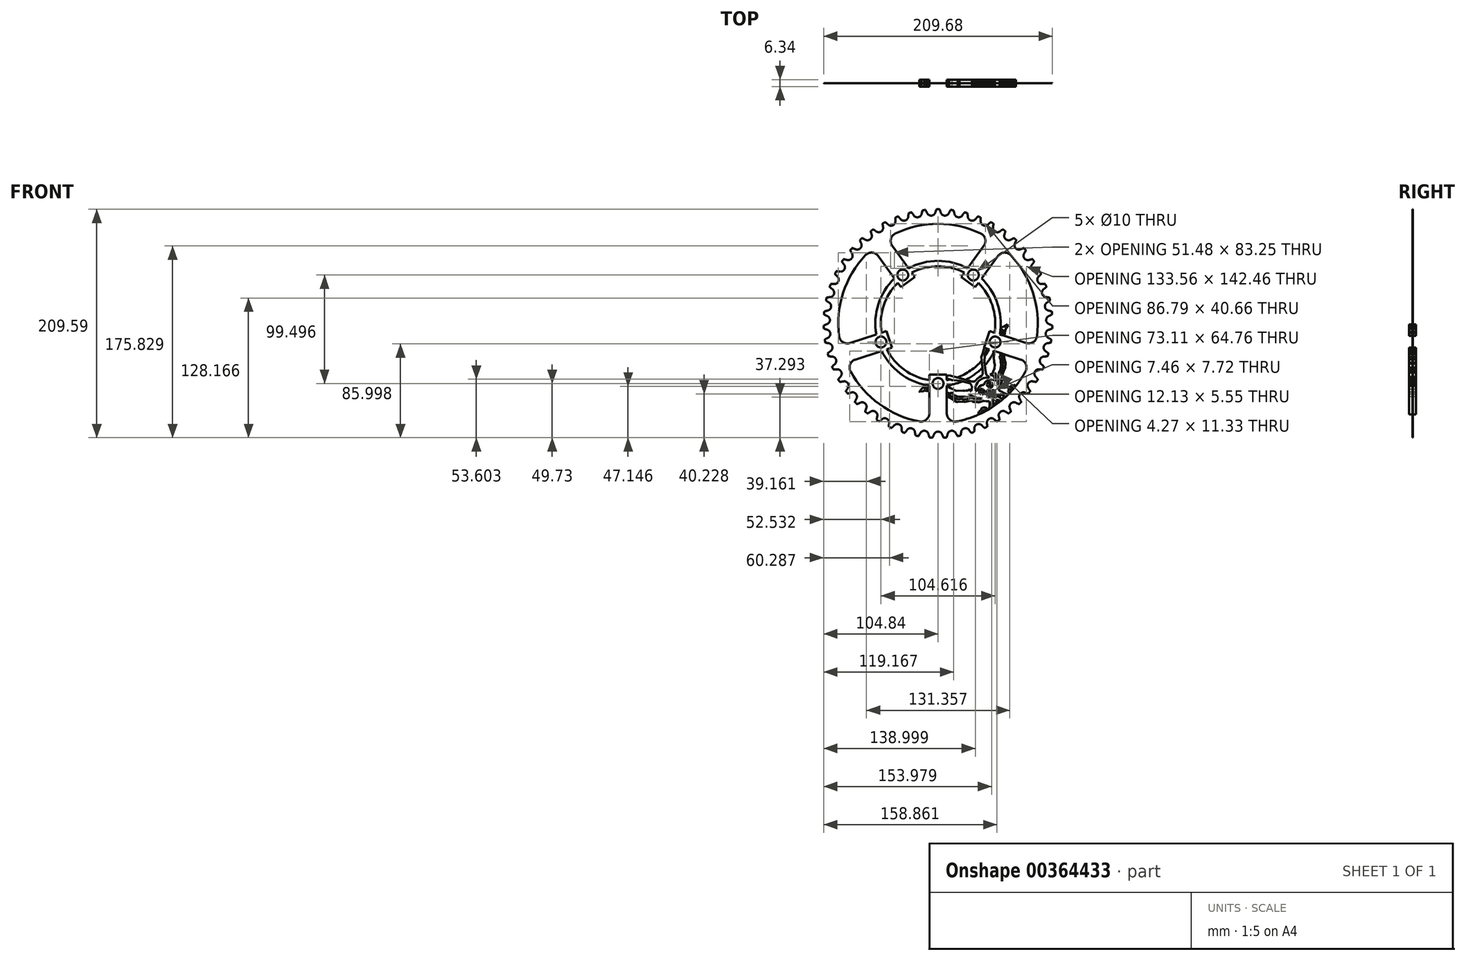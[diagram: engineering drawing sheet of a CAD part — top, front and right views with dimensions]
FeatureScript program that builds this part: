
annotation { "Feature Type Name" : "Feature", "Feature Type Description" : "" }
export const myFeature = defineFeature(function(context is Context, id is Id, definition is map)
    precondition{}
    {
        {
            var Q0;
            Q0=qCreatedBy(makeId("Front.planeOp"),FACE);
            var sketch = newSketch(context, id + "F0", { "sketchPlane" : qUnion([Q0])});
            skLineSegment(sketch, "E0", {"start": v(0, 0) * mm, "end": v(-6.35, 102.95) * mm, "construction": true});
            skLineSegment(sketch, "E1", {"start": v(0, 0) * mm, "end": v(6.35, 102.95) * mm, "construction": true});
            skArc(sketch, "E2", {"start": v(-6.1, 99) * mm, "mid": v(-3.93, 99.81) * mm, "end": v(-2.58, 101.71) * mm, "construction": true});
            skArc(sketch, "E3", {"start": v(-1.4, 104.85) * mm, "mid": v(-2, 103.3) * mm, "end": v(-2.55, 101.74) * mm});
            skLineSegment(sketch, "E4", {"start": v(-6.35, 102.95) * mm, "end": v(-2.58, 101.71) * mm, "construction": true});
            skCircle(sketch, "E5", {"center": v(0, 0) * mm, "radius": 103.19 * mm, "construction": true});
            skArc(sketch, "E6", {"start": v(1.4, 104.85) * mm, "mid": v(0, 104.86) * mm, "end": v(-1.4, 104.85) * mm});
            skLineSegment(sketch, "E7", {"start": v(0, 0) * mm, "end": v(0, 116.9) * mm, "construction": true});
            skArc(sketch, "E8", {"start": v(-6.1, 99) * mm, "mid": v(-3.9, 99.82) * mm, "end": v(-2.55, 101.74) * mm});
            skArc(sketch, "E9", {"start": v(2.58, 101.71) * mm, "mid": v(3.93, 99.81) * mm, "end": v(6.1, 99) * mm, "construction": true});
            skArc(sketch, "E10", {"start": v(2.55, 101.74) * mm, "mid": v(3.9, 99.82) * mm, "end": v(6.1, 99) * mm});
            skArc(sketch, "E11", {"start": v(2.56, 101.7) * mm, "mid": v(2, 103.29) * mm, "end": v(1.4, 104.85) * mm});
            skLineSegment(sketch, "E12", {"start": v(6.35, 102.95) * mm, "end": v(2.56, 101.7) * mm, "construction": true});
            skArc(sketch, "E13.1.0", {"start": v(-18.22, 97.5) * mm, "mid": v(-16.14, 98.58) * mm, "end": v(-15.03, 100.65) * mm});
            skArc(sketch, "E13.1.1", {"start": v(-14.27, 103.88) * mm, "mid": v(-14.68, 102.27) * mm, "end": v(-15.03, 100.65) * mm});
            skArc(sketch, "E13.1.2", {"start": v(-11.5, 104.22) * mm, "mid": v(-12.89, 104.06) * mm, "end": v(-14.27, 103.88) * mm});
            skArc(sketch, "E13.1.3", {"start": v(-9.96, 101.25) * mm, "mid": v(-10.7, 102.75) * mm, "end": v(-11.5, 104.22) * mm});
            skArc(sketch, "E13.1.4", {"start": v(-9.98, 101.28) * mm, "mid": v(-8.4, 99.54) * mm, "end": v(-6.1, 99) * mm});
            skArc(sketch, "E13.2.0", {"start": v(-30.07, 94.51) * mm, "mid": v(-28.13, 95.85) * mm, "end": v(-27.28, 98.04) * mm});
            skArc(sketch, "E13.2.1", {"start": v(-26.93, 101.34) * mm, "mid": v(-27.14, 99.7) * mm, "end": v(-27.28, 98.04) * mm});
            skArc(sketch, "E13.2.2", {"start": v(-24.22, 102.02) * mm, "mid": v(-25.58, 101.69) * mm, "end": v(-26.93, 101.34) * mm});
            skArc(sketch, "E13.2.3", {"start": v(-22.33, 99.26) * mm, "mid": v(-23.25, 100.66) * mm, "end": v(-24.22, 102.02) * mm});
            skArc(sketch, "E13.2.4", {"start": v(-22.35, 99.29) * mm, "mid": v(-20.56, 97.76) * mm, "end": v(-18.22, 97.5) * mm});
            skArc(sketch, "E13.3.0", {"start": v(-41.45, 90.1) * mm, "mid": v(-39.7, 91.67) * mm, "end": v(-39.13, 93.95) * mm});
            skArc(sketch, "E13.3.1", {"start": v(-39.18, 97.26) * mm, "mid": v(-39.18, 95.6) * mm, "end": v(-39.13, 93.95) * mm});
            skArc(sketch, "E13.3.2", {"start": v(-36.57, 98.27) * mm, "mid": v(-37.88, 97.78) * mm, "end": v(-39.18, 97.26) * mm});
            skArc(sketch, "E13.3.3", {"start": v(-34.36, 95.76) * mm, "mid": v(-35.44, 97.04) * mm, "end": v(-36.57, 98.27) * mm});
            skArc(sketch, "E13.3.4", {"start": v(-34.38, 95.79) * mm, "mid": v(-32.42, 94.49) * mm, "end": v(-30.07, 94.51) * mm});
            skArc(sketch, "E13.4.0", {"start": v(-52.21, 84.33) * mm, "mid": v(-50.66, 86.1) * mm, "end": v(-50.37, 88.43) * mm});
            skArc(sketch, "E13.4.1", {"start": v(-50.83, 91.71) * mm, "mid": v(-50.63, 90.06) * mm, "end": v(-50.37, 88.43) * mm});
            skArc(sketch, "E13.4.2", {"start": v(-48.37, 93.03) * mm, "mid": v(-49.6, 92.38) * mm, "end": v(-50.83, 91.71) * mm});
            skArc(sketch, "E13.4.3", {"start": v(-45.86, 90.81) * mm, "mid": v(-47.1, 91.94) * mm, "end": v(-48.37, 93.03) * mm});
            skArc(sketch, "E13.4.4", {"start": v(-45.89, 90.84) * mm, "mid": v(-43.78, 89.79) * mm, "end": v(-41.45, 90.1) * mm});
            skArc(sketch, "E13.5.0", {"start": v(-62.18, 77.27) * mm, "mid": v(-60.86, 79.22) * mm, "end": v(-60.86, 81.57) * mm});
            skArc(sketch, "E13.5.1", {"start": v(-61.72, 84.77) * mm, "mid": v(-61.32, 83.16) * mm, "end": v(-60.86, 81.57) * mm});
            skArc(sketch, "E13.5.2", {"start": v(-59.44, 86.38) * mm, "mid": v(-60.58, 85.58) * mm, "end": v(-61.72, 84.77) * mm});
            skArc(sketch, "E13.5.3", {"start": v(-56.68, 84.49) * mm, "mid": v(-58.04, 85.46) * mm, "end": v(-59.44, 86.38) * mm});
            skArc(sketch, "E13.5.4", {"start": v(-56.7, 84.5) * mm, "mid": v(-54.49, 83.73) * mm, "end": v(-52.21, 84.33) * mm});
            skArc(sketch, "E13.6.0", {"start": v(-71.2, 69.04) * mm, "mid": v(-70.13, 71.14) * mm, "end": v(-70.42, 73.47) * mm});
            skArc(sketch, "E13.6.1", {"start": v(-71.67, 76.54) * mm, "mid": v(-71.07, 75) * mm, "end": v(-70.42, 73.47) * mm});
            skArc(sketch, "E13.6.2", {"start": v(-69.6, 78.42) * mm, "mid": v(-70.64, 77.49) * mm, "end": v(-71.67, 76.54) * mm});
            skArc(sketch, "E13.6.3", {"start": v(-66.63, 76.88) * mm, "mid": v(-68.1, 77.68) * mm, "end": v(-69.6, 78.42) * mm});
            skArc(sketch, "E13.6.4", {"start": v(-66.66, 76.9) * mm, "mid": v(-64.36, 76.4) * mm, "end": v(-62.18, 77.27) * mm});
            skArc(sketch, "E13.7.0", {"start": v(-79.15, 59.77) * mm, "mid": v(-78.34, 61.98) * mm, "end": v(-78.92, 64.26) * mm});
            skArc(sketch, "E13.7.1", {"start": v(-80.53, 67.15) * mm, "mid": v(-79.75, 65.7) * mm, "end": v(-78.92, 64.26) * mm});
            skArc(sketch, "E13.7.2", {"start": v(-78.71, 69.28) * mm, "mid": v(-79.63, 68.22) * mm, "end": v(-80.53, 67.15) * mm});
            skArc(sketch, "E13.7.3", {"start": v(-75.57, 68.11) * mm, "mid": v(-77.13, 68.72) * mm, "end": v(-78.71, 69.28) * mm});
            skArc(sketch, "E13.7.4", {"start": v(-75.6, 68.13) * mm, "mid": v(-73.26, 67.9) * mm, "end": v(-71.2, 69.04) * mm});
            skArc(sketch, "E13.8.0", {"start": v(-85.9, 49.6) * mm, "mid": v(-85.37, 51.88) * mm, "end": v(-86.21, 54.07) * mm});
            skArc(sketch, "E13.8.1", {"start": v(-88.17, 56.75) * mm, "mid": v(-87.22, 55.4) * mm, "end": v(-86.21, 54.07) * mm});
            skArc(sketch, "E13.8.2", {"start": v(-86.63, 59.08) * mm, "mid": v(-87.4, 57.92) * mm, "end": v(-88.17, 56.75) * mm});
            skArc(sketch, "E13.8.3", {"start": v(-83.37, 58.3) * mm, "mid": v(-85, 58.72) * mm, "end": v(-86.63, 59.08) * mm});
            skArc(sketch, "E13.8.4", {"start": v(-83.4, 58.32) * mm, "mid": v(-81.05, 58.4) * mm, "end": v(-79.15, 59.77) * mm});
            skArc(sketch, "E13.9.0", {"start": v(-91.34, 38.66) * mm, "mid": v(-91.1, 41) * mm, "end": v(-92.2, 43.07) * mm});
            skArc(sketch, "E13.9.1", {"start": v(-94.48, 45.48) * mm, "mid": v(-93.36, 44.26) * mm, "end": v(-92.2, 43.07) * mm});
            skArc(sketch, "E13.9.2", {"start": v(-93.23, 47.99) * mm, "mid": v(-93.86, 46.74) * mm, "end": v(-94.48, 45.48) * mm});
            skArc(sketch, "E13.9.3", {"start": v(-89.9, 47.62) * mm, "mid": v(-91.56, 47.83) * mm, "end": v(-93.23, 47.99) * mm});
            skArc(sketch, "E13.9.4", {"start": v(-89.94, 47.63) * mm, "mid": v(-87.61, 47.99) * mm, "end": v(-85.9, 49.6) * mm});
            skArc(sketch, "E13.10.0", {"start": v(-95.4, 27.14) * mm, "mid": v(-95.44, 29.5) * mm, "end": v(-96.8, 31.41) * mm});
            skArc(sketch, "E13.10.1", {"start": v(-99.35, 33.53) * mm, "mid": v(-98.1, 32.45) * mm, "end": v(-96.8, 31.41) * mm});
            skArc(sketch, "E13.10.2", {"start": v(-98.42, 36.16) * mm, "mid": v(-98.9, 34.85) * mm, "end": v(-99.35, 33.53) * mm});
            skArc(sketch, "E13.10.3", {"start": v(-95.07, 36.21) * mm, "mid": v(-96.75, 36.22) * mm, "end": v(-98.42, 36.16) * mm});
            skArc(sketch, "E13.10.4", {"start": v(-95.1, 36.21) * mm, "mid": v(-92.85, 36.86) * mm, "end": v(-91.34, 38.66) * mm});
            skArc(sketch, "E13.11.0", {"start": v(-98, 15.21) * mm, "mid": v(-98.34, 17.54) * mm, "end": v(-99.93, 19.28) * mm});
            skArc(sketch, "E13.11.1", {"start": v(-102.72, 21.07) * mm, "mid": v(-101.34, 20.15) * mm, "end": v(-99.93, 19.28) * mm});
            skArc(sketch, "E13.11.2", {"start": v(-102.12, 23.8) * mm, "mid": v(-102.43, 22.43) * mm, "end": v(-102.72, 21.07) * mm});
            skArc(sketch, "E13.11.3", {"start": v(-98.8, 24.26) * mm, "mid": v(-100.47, 24.05) * mm, "end": v(-102.12, 23.8) * mm});
            skArc(sketch, "E13.11.4", {"start": v(-98.84, 24.25) * mm, "mid": v(-96.67, 25.17) * mm, "end": v(-95.4, 27.14) * mm});
            skArc(sketch, "E13.12.0", {"start": v(-99.13, 3.05) * mm, "mid": v(-99.75, 5.32) * mm, "end": v(-101.54, 6.85) * mm});
            skArc(sketch, "E13.12.1", {"start": v(-104.53, 8.28) * mm, "mid": v(-103.05, 7.54) * mm, "end": v(-101.54, 6.85) * mm});
            skArc(sketch, "E13.12.2", {"start": v(-104.27, 11.07) * mm, "mid": v(-104.4, 9.67) * mm, "end": v(-104.53, 8.28) * mm});
            skArc(sketch, "E13.12.3", {"start": v(-101.03, 11.93) * mm, "mid": v(-102.66, 11.53) * mm, "end": v(-104.27, 11.07) * mm});
            skArc(sketch, "E13.12.4", {"start": v(-101.07, 11.92) * mm, "mid": v(-99.03, 13.1) * mm, "end": v(-98, 15.21) * mm});
            skArc(sketch, "E13.13.0", {"start": v(-98.76, -9.15) * mm, "mid": v(-99.65, -6.98) * mm, "end": v(-101.61, -5.68) * mm});
            skArc(sketch, "E13.13.1", {"start": v(-104.75, -4.63) * mm, "mid": v(-103.2, -5.18) * mm, "end": v(-101.61, -5.68) * mm});
            skArc(sketch, "E13.13.2", {"start": v(-104.84, -1.83) * mm, "mid": v(-104.8, -3.23) * mm, "end": v(-104.75, -4.63) * mm});
            skArc(sketch, "E13.13.3", {"start": v(-101.74, -0.58) * mm, "mid": v(-103.3, -1.18) * mm, "end": v(-104.84, -1.83) * mm});
            skArc(sketch, "E13.13.4", {"start": v(-101.77, -0.59) * mm, "mid": v(-99.9, 0.83) * mm, "end": v(-99.13, 3.05) * mm});
            skArc(sketch, "E13.14.0", {"start": v(-96.88, -21.22) * mm, "mid": v(-98.04, -19.17) * mm, "end": v(-100.14, -18.12) * mm});
            skArc(sketch, "E13.14.1", {"start": v(-103.4, -17.46) * mm, "mid": v(-101.77, -17.82) * mm, "end": v(-100.14, -18.12) * mm});
            skArc(sketch, "E13.14.2", {"start": v(-103.82, -14.7) * mm, "mid": v(-103.62, -16.08) * mm, "end": v(-103.4, -17.46) * mm});
            skArc(sketch, "E13.14.3", {"start": v(-100.9, -13.07) * mm, "mid": v(-102.37, -13.86) * mm, "end": v(-103.82, -14.7) * mm});
            skArc(sketch, "E13.14.4", {"start": v(-100.92, -13.09) * mm, "mid": v(-99.24, -11.45) * mm, "end": v(-98.76, -9.15) * mm});
            skArc(sketch, "E13.15.0", {"start": v(-93.54, -32.96) * mm, "mid": v(-94.94, -31.07) * mm, "end": v(-97.16, -30.3) * mm});
            skArc(sketch, "E13.15.1", {"start": v(-100.46, -30.04) * mm, "mid": v(-98.81, -30.2) * mm, "end": v(-97.16, -30.3) * mm});
            skArc(sketch, "E13.15.2", {"start": v(-101.23, -27.35) * mm, "mid": v(-100.85, -28.7) * mm, "end": v(-100.46, -30.04) * mm});
            skArc(sketch, "E13.15.3", {"start": v(-98.52, -25.37) * mm, "mid": v(-99.9, -26.34) * mm, "end": v(-101.23, -27.35) * mm});
            skArc(sketch, "E13.15.4", {"start": v(-98.55, -25.4) * mm, "mid": v(-97.08, -23.56) * mm, "end": v(-96.88, -21.22) * mm});
            skArc(sketch, "E13.16.0", {"start": v(-88.78, -44.2) * mm, "mid": v(-90.4, -42.5) * mm, "end": v(-92.7, -42) * mm});
            skArc(sketch, "E13.16.1", {"start": v(-96, -42.15) * mm, "mid": v(-94.35, -42.1) * mm, "end": v(-92.7, -42) * mm});
            skArc(sketch, "E13.16.2", {"start": v(-97.1, -39.58) * mm, "mid": v(-96.56, -40.87) * mm, "end": v(-96, -42.15) * mm});
            skArc(sketch, "E13.16.3", {"start": v(-94.66, -37.29) * mm, "mid": v(-95.9, -38.41) * mm, "end": v(-97.1, -39.58) * mm});
            skArc(sketch, "E13.16.4", {"start": v(-94.68, -37.31) * mm, "mid": v(-93.45, -35.31) * mm, "end": v(-93.54, -32.96) * mm});
            skArc(sketch, "E13.17.0", {"start": v(-82.68, -54.78) * mm, "mid": v(-84.5, -53.3) * mm, "end": v(-86.83, -53.07) * mm});
            skArc(sketch, "E13.17.1", {"start": v(-90.1, -53.63) * mm, "mid": v(-88.46, -53.38) * mm, "end": v(-86.83, -53.07) * mm});
            skArc(sketch, "E13.17.2", {"start": v(-91.5, -51.21) * mm, "mid": v(-90.8, -52.43) * mm, "end": v(-90.1, -53.63) * mm});
            skArc(sketch, "E13.17.3", {"start": v(-89.36, -48.64) * mm, "mid": v(-90.45, -49.9) * mm, "end": v(-91.5, -51.21) * mm});
            skArc(sketch, "E13.17.4", {"start": v(-89.38, -48.66) * mm, "mid": v(-88.4, -46.53) * mm, "end": v(-88.78, -44.2) * mm});
            skArc(sketch, "E13.18.0", {"start": v(-75.32, -64.53) * mm, "mid": v(-77.3, -63.27) * mm, "end": v(-79.65, -63.34) * mm});
            skArc(sketch, "E13.18.1", {"start": v(-82.83, -64.3) * mm, "mid": v(-81.23, -63.85) * mm, "end": v(-79.65, -63.34) * mm});
            skArc(sketch, "E13.18.2", {"start": v(-84.51, -62.07) * mm, "mid": v(-83.68, -63.2) * mm, "end": v(-82.83, -64.3) * mm});
            skArc(sketch, "E13.18.3", {"start": v(-82.7, -59.25) * mm, "mid": v(-83.63, -60.64) * mm, "end": v(-84.51, -62.07) * mm});
            skArc(sketch, "E13.18.4", {"start": v(-82.72, -59.28) * mm, "mid": v(-82.01, -57.04) * mm, "end": v(-82.68, -54.78) * mm});
            skArc(sketch, "E13.19.0", {"start": v(-66.82, -73.3) * mm, "mid": v(-68.94, -72.3) * mm, "end": v(-71.27, -72.65) * mm});
            skArc(sketch, "E13.19.1", {"start": v(-74.3, -74) * mm, "mid": v(-72.77, -73.35) * mm, "end": v(-71.27, -72.65) * mm});
            skArc(sketch, "E13.19.2", {"start": v(-76.24, -71.98) * mm, "mid": v(-75.28, -73) * mm, "end": v(-74.3, -74) * mm});
            skArc(sketch, "E13.19.3", {"start": v(-74.8, -68.96) * mm, "mid": v(-75.55, -70.46) * mm, "end": v(-76.24, -71.98) * mm});
            skArc(sketch, "E13.19.4", {"start": v(-74.81, -69) * mm, "mid": v(-74.38, -66.68) * mm, "end": v(-75.32, -64.53) * mm});
            skArc(sketch, "E13.20.0", {"start": v(-57.3, -80.95) * mm, "mid": v(-59.54, -80.22) * mm, "end": v(-61.8, -80.86) * mm});
            skArc(sketch, "E13.20.1", {"start": v(-64.64, -82.56) * mm, "mid": v(-63.2, -81.73) * mm, "end": v(-61.8, -80.86) * mm});
            skArc(sketch, "E13.20.2", {"start": v(-66.82, -80.8) * mm, "mid": v(-65.74, -81.7) * mm, "end": v(-64.64, -82.56) * mm});
            skArc(sketch, "E13.20.3", {"start": v(-65.75, -77.63) * mm, "mid": v(-66.31, -79.21) * mm, "end": v(-66.82, -80.8) * mm});
            skArc(sketch, "E13.20.4", {"start": v(-65.76, -77.66) * mm, "mid": v(-65.62, -75.32) * mm, "end": v(-66.82, -73.3) * mm});
            skArc(sketch, "E13.21.0", {"start": v(-46.92, -87.38) * mm, "mid": v(-49.23, -86.92) * mm, "end": v(-51.4, -87.84) * mm});
            skArc(sketch, "E13.21.1", {"start": v(-54, -89.88) * mm, "mid": v(-52.68, -88.88) * mm, "end": v(-51.4, -87.84) * mm});
            skArc(sketch, "E13.21.2", {"start": v(-56.38, -88.4) * mm, "mid": v(-55.2, -89.15) * mm, "end": v(-54, -89.88) * mm});
            skArc(sketch, "E13.21.3", {"start": v(-55.71, -85.12) * mm, "mid": v(-56.08, -86.76) * mm, "end": v(-56.38, -88.4) * mm});
            skArc(sketch, "E13.21.4", {"start": v(-55.72, -85.16) * mm, "mid": v(-55.87, -82.81) * mm, "end": v(-57.3, -80.95) * mm});
            skArc(sketch, "E13.22.0", {"start": v(-35.83, -92.48) * mm, "mid": v(-38.17, -92.31) * mm, "end": v(-40.2, -93.49) * mm});
            skArc(sketch, "E13.22.1", {"start": v(-42.55, -95.83) * mm, "mid": v(-41.36, -94.68) * mm, "end": v(-40.2, -93.49) * mm});
            skArc(sketch, "E13.22.2", {"start": v(-45.1, -94.67) * mm, "mid": v(-43.83, -95.26) * mm, "end": v(-42.55, -95.83) * mm});
            skArc(sketch, "E13.22.3", {"start": v(-44.83, -91.33) * mm, "mid": v(-45, -93) * mm, "end": v(-45.1, -94.67) * mm});
            skArc(sketch, "E13.22.4", {"start": v(-44.84, -91.36) * mm, "mid": v(-45.27, -89.05) * mm, "end": v(-46.92, -87.38) * mm});
            skArc(sketch, "E13.23.0", {"start": v(-24.2, -96.19) * mm, "mid": v(-26.54, -96.3) * mm, "end": v(-28.42, -97.72) * mm});
            skArc(sketch, "E13.23.1", {"start": v(-30.45, -100.34) * mm, "mid": v(-29.41, -99.05) * mm, "end": v(-28.42, -97.72) * mm});
            skArc(sketch, "E13.23.2", {"start": v(-33.12, -99.49) * mm, "mid": v(-31.79, -99.92) * mm, "end": v(-30.45, -100.34) * mm});
            skArc(sketch, "E13.23.3", {"start": v(-33.27, -96.14) * mm, "mid": v(-33.22, -97.82) * mm, "end": v(-33.12, -99.49) * mm});
            skArc(sketch, "E13.23.4", {"start": v(-33.27, -96.18) * mm, "mid": v(-33.98, -93.94) * mm, "end": v(-35.83, -92.48) * mm});
            skArc(sketch, "E13.24.0", {"start": v(-12.19, -98.43) * mm, "mid": v(-14.5, -98.84) * mm, "end": v(-16.2, -100.47) * mm});
            skArc(sketch, "E13.24.1", {"start": v(-17.9, -103.32) * mm, "mid": v(-17.02, -101.91) * mm, "end": v(-16.2, -100.47) * mm});
            skArc(sketch, "E13.24.2", {"start": v(-20.64, -102.8) * mm, "mid": v(-19.27, -103.07) * mm, "end": v(-17.9, -103.32) * mm});
            skArc(sketch, "E13.24.3", {"start": v(-21.2, -99.5) * mm, "mid": v(-20.95, -101.16) * mm, "end": v(-20.64, -102.8) * mm});
            skArc(sketch, "E13.24.4", {"start": v(-21.2, -99.54) * mm, "mid": v(-22.18, -97.4) * mm, "end": v(-24.2, -96.19) * mm});
            skArc(sketch, "E13.25.0", {"start": v(0, -99.18) * mm, "mid": v(-2.25, -99.87) * mm, "end": v(-3.72, -101.7) * mm});
            skArc(sketch, "E13.25.1", {"start": v(-5.06, -104.73) * mm, "mid": v(-4.36, -103.23) * mm, "end": v(-3.72, -101.7) * mm});
            skArc(sketch, "E13.25.2", {"start": v(-7.85, -104.56) * mm, "mid": v(-6.46, -104.66) * mm, "end": v(-5.06, -104.73) * mm});
            skArc(sketch, "E13.25.3", {"start": v(-8.81, -101.35) * mm, "mid": v(-8.36, -102.97) * mm, "end": v(-7.85, -104.56) * mm});
            skArc(sketch, "E13.25.4", {"start": v(-8.8, -101.39) * mm, "mid": v(-10.04, -99.39) * mm, "end": v(-12.19, -98.43) * mm});
            skArc(sketch, "E13.26.0", {"start": v(12.19, -98.43) * mm, "mid": v(10.04, -99.39) * mm, "end": v(8.8, -101.39) * mm});
            skArc(sketch, "E13.26.1", {"start": v(7.85, -104.56) * mm, "mid": v(8.35, -102.98) * mm, "end": v(8.8, -101.39) * mm});
            skArc(sketch, "E13.26.2", {"start": v(5.06, -104.73) * mm, "mid": v(6.46, -104.66) * mm, "end": v(7.85, -104.56) * mm});
            skArc(sketch, "E13.26.3", {"start": v(3.7, -101.67) * mm, "mid": v(4.36, -103.21) * mm, "end": v(5.06, -104.73) * mm});
            skArc(sketch, "E13.26.4", {"start": v(3.72, -101.7) * mm, "mid": v(2.25, -99.87) * mm, "end": v(0, -99.18) * mm});
            skArc(sketch, "E13.27.0", {"start": v(24.2, -96.19) * mm, "mid": v(22.18, -97.4) * mm, "end": v(21.2, -99.54) * mm});
            skArc(sketch, "E13.27.1", {"start": v(20.64, -102.8) * mm, "mid": v(20.95, -101.18) * mm, "end": v(21.2, -99.54) * mm});
            skArc(sketch, "E13.27.2", {"start": v(17.9, -103.32) * mm, "mid": v(19.27, -103.07) * mm, "end": v(20.64, -102.8) * mm});
            skArc(sketch, "E13.27.3", {"start": v(16.17, -100.44) * mm, "mid": v(17, -101.9) * mm, "end": v(17.9, -103.32) * mm});
            skArc(sketch, "E13.27.4", {"start": v(16.2, -100.47) * mm, "mid": v(14.5, -98.84) * mm, "end": v(12.19, -98.43) * mm});
            skArc(sketch, "E13.28.0", {"start": v(35.83, -92.48) * mm, "mid": v(33.98, -93.94) * mm, "end": v(33.27, -96.18) * mm});
            skArc(sketch, "E13.28.1", {"start": v(33.12, -99.49) * mm, "mid": v(33.22, -97.83) * mm, "end": v(33.27, -96.18) * mm});
            skArc(sketch, "E13.28.2", {"start": v(30.45, -100.34) * mm, "mid": v(31.79, -99.92) * mm, "end": v(33.12, -99.49) * mm});
            skArc(sketch, "E13.28.3", {"start": v(28.4, -97.7) * mm, "mid": v(29.4, -99.03) * mm, "end": v(30.45, -100.34) * mm});
            skArc(sketch, "E13.28.4", {"start": v(28.42, -97.72) * mm, "mid": v(26.54, -96.3) * mm, "end": v(24.2, -96.19) * mm});
            skArc(sketch, "E13.29.0", {"start": v(46.92, -87.38) * mm, "mid": v(45.27, -89.05) * mm, "end": v(44.84, -91.36) * mm});
            skArc(sketch, "E13.29.1", {"start": v(45.1, -94.67) * mm, "mid": v(45, -93.01) * mm, "end": v(44.84, -91.36) * mm});
            skArc(sketch, "E13.29.2", {"start": v(42.55, -95.83) * mm, "mid": v(43.83, -95.26) * mm, "end": v(45.1, -94.67) * mm});
            skArc(sketch, "E13.29.3", {"start": v(40.19, -93.46) * mm, "mid": v(41.35, -94.67) * mm, "end": v(42.55, -95.83) * mm});
            skArc(sketch, "E13.29.4", {"start": v(40.2, -93.49) * mm, "mid": v(38.17, -92.31) * mm, "end": v(35.83, -92.48) * mm});
            skArc(sketch, "E13.30.0", {"start": v(57.3, -80.95) * mm, "mid": v(55.87, -82.81) * mm, "end": v(55.72, -85.16) * mm});
            skArc(sketch, "E13.30.1", {"start": v(56.38, -88.4) * mm, "mid": v(56.08, -86.78) * mm, "end": v(55.72, -85.16) * mm});
            skArc(sketch, "E13.30.2", {"start": v(54, -89.88) * mm, "mid": v(55.2, -89.15) * mm, "end": v(56.38, -88.4) * mm});
            skArc(sketch, "E13.30.3", {"start": v(51.37, -87.82) * mm, "mid": v(52.67, -88.87) * mm, "end": v(54, -89.88) * mm});
            skArc(sketch, "E13.30.4", {"start": v(51.4, -87.84) * mm, "mid": v(49.23, -86.92) * mm, "end": v(46.92, -87.38) * mm});
            skArc(sketch, "E13.31.0", {"start": v(66.82, -73.3) * mm, "mid": v(65.62, -75.32) * mm, "end": v(65.76, -77.66) * mm});
            skArc(sketch, "E13.31.1", {"start": v(66.82, -80.8) * mm, "mid": v(66.32, -79.23) * mm, "end": v(65.76, -77.66) * mm});
            skArc(sketch, "E13.31.2", {"start": v(64.64, -82.56) * mm, "mid": v(65.74, -81.7) * mm, "end": v(66.82, -80.8) * mm});
            skArc(sketch, "E13.31.3", {"start": v(61.77, -80.84) * mm, "mid": v(63.2, -81.72) * mm, "end": v(64.64, -82.56) * mm});
            skArc(sketch, "E13.31.4", {"start": v(61.8, -80.86) * mm, "mid": v(59.54, -80.22) * mm, "end": v(57.3, -80.95) * mm});
            skArc(sketch, "E13.32.0", {"start": v(75.32, -64.53) * mm, "mid": v(74.38, -66.68) * mm, "end": v(74.81, -69) * mm});
            skArc(sketch, "E13.32.1", {"start": v(76.24, -71.98) * mm, "mid": v(75.55, -70.48) * mm, "end": v(74.81, -69) * mm});
            skArc(sketch, "E13.32.2", {"start": v(74.3, -74) * mm, "mid": v(75.28, -73) * mm, "end": v(76.24, -71.98) * mm});
            skArc(sketch, "E13.32.3", {"start": v(71.23, -72.64) * mm, "mid": v(72.75, -73.34) * mm, "end": v(74.3, -74) * mm});
            skArc(sketch, "E13.32.4", {"start": v(71.27, -72.65) * mm, "mid": v(68.94, -72.3) * mm, "end": v(66.82, -73.3) * mm});
            skArc(sketch, "E13.33.0", {"start": v(82.68, -54.78) * mm, "mid": v(82.01, -57.04) * mm, "end": v(82.72, -59.28) * mm});
            skArc(sketch, "E13.33.1", {"start": v(84.51, -62.07) * mm, "mid": v(83.64, -60.66) * mm, "end": v(82.72, -59.28) * mm});
            skArc(sketch, "E13.33.2", {"start": v(82.83, -64.3) * mm, "mid": v(83.68, -63.2) * mm, "end": v(84.51, -62.07) * mm});
            skArc(sketch, "E13.33.3", {"start": v(79.62, -63.33) * mm, "mid": v(81.22, -63.84) * mm, "end": v(82.83, -64.3) * mm});
            skArc(sketch, "E13.33.4", {"start": v(79.65, -63.34) * mm, "mid": v(77.3, -63.27) * mm, "end": v(75.32, -64.53) * mm});
            skArc(sketch, "E13.34.0", {"start": v(88.78, -44.2) * mm, "mid": v(88.4, -46.53) * mm, "end": v(89.38, -48.66) * mm});
            skArc(sketch, "E13.34.1", {"start": v(91.5, -51.21) * mm, "mid": v(90.46, -49.92) * mm, "end": v(89.38, -48.66) * mm});
            skArc(sketch, "E13.34.2", {"start": v(90.1, -53.63) * mm, "mid": v(90.8, -52.43) * mm, "end": v(91.5, -51.21) * mm});
            skArc(sketch, "E13.34.3", {"start": v(86.8, -53.07) * mm, "mid": v(88.45, -53.38) * mm, "end": v(90.1, -53.63) * mm});
            skArc(sketch, "E13.34.4", {"start": v(86.83, -53.07) * mm, "mid": v(84.5, -53.3) * mm, "end": v(82.68, -54.78) * mm});
            skArc(sketch, "E13.35.0", {"start": v(93.54, -32.96) * mm, "mid": v(93.45, -35.31) * mm, "end": v(94.68, -37.31) * mm});
            skArc(sketch, "E13.35.1", {"start": v(97.1, -39.58) * mm, "mid": v(95.91, -38.42) * mm, "end": v(94.68, -37.31) * mm});
            skArc(sketch, "E13.35.2", {"start": v(96, -42.15) * mm, "mid": v(96.56, -40.87) * mm, "end": v(97.1, -39.58) * mm});
            skArc(sketch, "E13.35.3", {"start": v(92.66, -42) * mm, "mid": v(94.34, -42.1) * mm, "end": v(96, -42.15) * mm});
            skArc(sketch, "E13.35.4", {"start": v(92.7, -42) * mm, "mid": v(90.4, -42.5) * mm, "end": v(88.78, -44.2) * mm});
            skArc(sketch, "E13.36.0", {"start": v(96.88, -21.22) * mm, "mid": v(97.08, -23.56) * mm, "end": v(98.55, -25.4) * mm});
            skArc(sketch, "E13.36.1", {"start": v(101.23, -27.35) * mm, "mid": v(99.9, -26.35) * mm, "end": v(98.55, -25.4) * mm});
            skArc(sketch, "E13.36.2", {"start": v(100.46, -30.04) * mm, "mid": v(100.85, -28.7) * mm, "end": v(101.23, -27.35) * mm});
            skArc(sketch, "E13.36.3", {"start": v(97.12, -30.3) * mm, "mid": v(98.8, -30.2) * mm, "end": v(100.46, -30.04) * mm});
            skArc(sketch, "E13.36.4", {"start": v(97.16, -30.3) * mm, "mid": v(94.94, -31.07) * mm, "end": v(93.54, -32.96) * mm});
            skArc(sketch, "E13.37.0", {"start": v(98.76, -9.15) * mm, "mid": v(99.24, -11.45) * mm, "end": v(100.92, -13.09) * mm});
            skArc(sketch, "E13.37.1", {"start": v(103.82, -14.7) * mm, "mid": v(102.39, -13.87) * mm, "end": v(100.92, -13.09) * mm});
            skArc(sketch, "E13.37.2", {"start": v(103.4, -17.46) * mm, "mid": v(103.62, -16.08) * mm, "end": v(103.82, -14.7) * mm});
            skArc(sketch, "E13.37.3", {"start": v(100.1, -18.13) * mm, "mid": v(101.76, -17.82) * mm, "end": v(103.4, -17.46) * mm});
            skArc(sketch, "E13.37.4", {"start": v(100.14, -18.12) * mm, "mid": v(98.04, -19.17) * mm, "end": v(96.88, -21.22) * mm});
            skArc(sketch, "E13.38.0", {"start": v(99.13, 3.05) * mm, "mid": v(99.9, 0.83) * mm, "end": v(101.77, -0.59) * mm});
            skArc(sketch, "E13.38.1", {"start": v(104.84, -1.83) * mm, "mid": v(103.31, -1.18) * mm, "end": v(101.77, -0.59) * mm});
            skArc(sketch, "E13.38.2", {"start": v(104.75, -4.63) * mm, "mid": v(104.8, -3.23) * mm, "end": v(104.84, -1.83) * mm});
            skArc(sketch, "E13.38.3", {"start": v(101.58, -5.69) * mm, "mid": v(103.18, -5.18) * mm, "end": v(104.75, -4.63) * mm});
            skArc(sketch, "E13.38.4", {"start": v(101.61, -5.68) * mm, "mid": v(99.65, -6.98) * mm, "end": v(98.76, -9.15) * mm});
            skArc(sketch, "E13.39.0", {"start": v(98, 15.21) * mm, "mid": v(99.03, 13.1) * mm, "end": v(101.07, 11.92) * mm});
            skArc(sketch, "E13.39.1", {"start": v(104.27, 11.07) * mm, "mid": v(102.68, 11.52) * mm, "end": v(101.07, 11.92) * mm});
            skArc(sketch, "E13.39.2", {"start": v(104.53, 8.28) * mm, "mid": v(104.4, 9.67) * mm, "end": v(104.27, 11.07) * mm});
            skArc(sketch, "E13.39.3", {"start": v(101.5, 6.84) * mm, "mid": v(103.03, 7.53) * mm, "end": v(104.53, 8.28) * mm});
            skArc(sketch, "E13.39.4", {"start": v(101.54, 6.85) * mm, "mid": v(99.75, 5.32) * mm, "end": v(99.13, 3.05) * mm});
            skArc(sketch, "E13.40.0", {"start": v(95.4, 27.14) * mm, "mid": v(96.67, 25.17) * mm, "end": v(98.84, 24.25) * mm});
            skArc(sketch, "E13.40.1", {"start": v(102.12, 23.8) * mm, "mid": v(100.48, 24.05) * mm, "end": v(98.84, 24.25) * mm});
            skArc(sketch, "E13.40.2", {"start": v(102.72, 21.07) * mm, "mid": v(102.43, 22.43) * mm, "end": v(102.12, 23.8) * mm});
            skArc(sketch, "E13.40.3", {"start": v(99.9, 19.26) * mm, "mid": v(101.32, 20.14) * mm, "end": v(102.72, 21.07) * mm});
            skArc(sketch, "E13.40.4", {"start": v(99.93, 19.28) * mm, "mid": v(98.34, 17.54) * mm, "end": v(98, 15.21) * mm});
            skArc(sketch, "E13.41.0", {"start": v(91.34, 38.66) * mm, "mid": v(92.85, 36.86) * mm, "end": v(95.1, 36.21) * mm});
            skArc(sketch, "E13.41.1", {"start": v(98.42, 36.16) * mm, "mid": v(96.77, 36.22) * mm, "end": v(95.1, 36.21) * mm});
            skArc(sketch, "E13.41.2", {"start": v(99.35, 33.53) * mm, "mid": v(98.9, 34.85) * mm, "end": v(98.42, 36.16) * mm});
            skArc(sketch, "E13.41.3", {"start": v(96.77, 31.4) * mm, "mid": v(98.08, 32.44) * mm, "end": v(99.35, 33.53) * mm});
            skArc(sketch, "E13.41.4", {"start": v(96.8, 31.41) * mm, "mid": v(95.44, 29.5) * mm, "end": v(95.4, 27.14) * mm});
            skArc(sketch, "E13.42.0", {"start": v(85.9, 49.6) * mm, "mid": v(87.61, 47.99) * mm, "end": v(89.94, 47.63) * mm});
            skArc(sketch, "E13.42.1", {"start": v(93.23, 47.99) * mm, "mid": v(91.58, 47.83) * mm, "end": v(89.94, 47.63) * mm});
            skArc(sketch, "E13.42.2", {"start": v(94.48, 45.48) * mm, "mid": v(93.86, 46.74) * mm, "end": v(93.23, 47.99) * mm});
            skArc(sketch, "E13.42.3", {"start": v(92.18, 43.04) * mm, "mid": v(93.35, 44.24) * mm, "end": v(94.48, 45.48) * mm});
            skArc(sketch, "E13.42.4", {"start": v(92.2, 43.07) * mm, "mid": v(91.1, 41) * mm, "end": v(91.34, 38.66) * mm});
            skArc(sketch, "E13.43.0", {"start": v(79.15, 59.77) * mm, "mid": v(81.05, 58.4) * mm, "end": v(83.4, 58.32) * mm});
            skArc(sketch, "E13.43.1", {"start": v(86.63, 59.08) * mm, "mid": v(85, 58.73) * mm, "end": v(83.4, 58.32) * mm});
            skArc(sketch, "E13.43.2", {"start": v(88.17, 56.75) * mm, "mid": v(87.4, 57.92) * mm, "end": v(86.63, 59.08) * mm});
            skArc(sketch, "E13.43.3", {"start": v(86.2, 54.05) * mm, "mid": v(87.2, 55.38) * mm, "end": v(88.17, 56.75) * mm});
            skArc(sketch, "E13.43.4", {"start": v(86.21, 54.07) * mm, "mid": v(85.37, 51.88) * mm, "end": v(85.9, 49.6) * mm});
            skArc(sketch, "E14.2.44.0", {"start": v(71.2, 69.04) * mm, "mid": v(73.26, 67.9) * mm, "end": v(75.6, 68.13) * mm});
            skArc(sketch, "E14.4.44.0", {"start": v(78.71, 69.28) * mm, "mid": v(77.15, 68.73) * mm, "end": v(75.6, 68.13) * mm});
            skArc(sketch, "E14.8.44.0", {"start": v(80.53, 67.15) * mm, "mid": v(79.63, 68.22) * mm, "end": v(78.71, 69.28) * mm});
            skArc(sketch, "E14.12.44.0", {"start": v(78.9, 64.23) * mm, "mid": v(79.74, 65.68) * mm, "end": v(80.53, 67.15) * mm});
            skArc(sketch, "E14.16.44.0", {"start": v(78.92, 64.26) * mm, "mid": v(78.34, 61.98) * mm, "end": v(79.15, 59.77) * mm});
            skArc(sketch, "E14.2.45.0", {"start": v(62.18, 77.27) * mm, "mid": v(64.36, 76.4) * mm, "end": v(66.66, 76.9) * mm});
            skArc(sketch, "E14.4.45.0", {"start": v(69.6, 78.42) * mm, "mid": v(68.12, 77.69) * mm, "end": v(66.66, 76.9) * mm});
            skArc(sketch, "E14.8.45.0", {"start": v(71.67, 76.54) * mm, "mid": v(70.64, 77.49) * mm, "end": v(69.6, 78.42) * mm});
            skArc(sketch, "E14.12.45.0", {"start": v(70.4, 73.44) * mm, "mid": v(71.06, 74.98) * mm, "end": v(71.67, 76.54) * mm});
            skArc(sketch, "E14.16.45.0", {"start": v(70.42, 73.47) * mm, "mid": v(70.13, 71.14) * mm, "end": v(71.2, 69.04) * mm});
            skArc(sketch, "E14.2.46.0", {"start": v(52.21, 84.33) * mm, "mid": v(54.49, 83.73) * mm, "end": v(56.7, 84.5) * mm});
            skArc(sketch, "E14.4.46.0", {"start": v(59.44, 86.38) * mm, "mid": v(58.05, 85.47) * mm, "end": v(56.7, 84.5) * mm});
            skArc(sketch, "E14.8.46.0", {"start": v(61.72, 84.77) * mm, "mid": v(60.58, 85.58) * mm, "end": v(59.44, 86.38) * mm});
            skArc(sketch, "E14.12.46.0", {"start": v(60.85, 81.53) * mm, "mid": v(61.31, 83.14) * mm, "end": v(61.72, 84.77) * mm});
            skArc(sketch, "E14.16.46.0", {"start": v(60.86, 81.57) * mm, "mid": v(60.86, 79.22) * mm, "end": v(62.18, 77.27) * mm});
            skArc(sketch, "E14.2.47.0", {"start": v(41.45, 90.1) * mm, "mid": v(43.78, 89.79) * mm, "end": v(45.89, 90.84) * mm});
            skArc(sketch, "E14.4.47.0", {"start": v(48.37, 93.03) * mm, "mid": v(47.11, 91.96) * mm, "end": v(45.89, 90.84) * mm});
            skArc(sketch, "E14.8.47.0", {"start": v(50.83, 91.71) * mm, "mid": v(49.6, 92.38) * mm, "end": v(48.37, 93.03) * mm});
            skArc(sketch, "E14.12.47.0", {"start": v(50.37, 88.4) * mm, "mid": v(50.63, 90.05) * mm, "end": v(50.83, 91.71) * mm});
            skArc(sketch, "E14.16.47.0", {"start": v(50.37, 88.43) * mm, "mid": v(50.66, 86.1) * mm, "end": v(52.21, 84.33) * mm});
            skArc(sketch, "E14.2.48.0", {"start": v(30.07, 94.51) * mm, "mid": v(32.42, 94.49) * mm, "end": v(34.38, 95.79) * mm});
            skArc(sketch, "E14.4.48.0", {"start": v(36.57, 98.27) * mm, "mid": v(35.45, 97.05) * mm, "end": v(34.38, 95.79) * mm});
            skArc(sketch, "E14.8.48.0", {"start": v(39.18, 97.26) * mm, "mid": v(37.88, 97.78) * mm, "end": v(36.57, 98.27) * mm});
            skArc(sketch, "E14.12.48.0", {"start": v(39.12, 93.91) * mm, "mid": v(39.18, 95.59) * mm, "end": v(39.18, 97.26) * mm});
            skArc(sketch, "E14.16.48.0", {"start": v(39.13, 93.95) * mm, "mid": v(39.7, 91.67) * mm, "end": v(41.45, 90.1) * mm});
            skArc(sketch, "E14.2.49.0", {"start": v(18.22, 97.5) * mm, "mid": v(20.56, 97.76) * mm, "end": v(22.35, 99.29) * mm});
            skArc(sketch, "E14.4.49.0", {"start": v(24.22, 102.02) * mm, "mid": v(23.26, 100.67) * mm, "end": v(22.35, 99.29) * mm});
            skArc(sketch, "E14.8.49.0", {"start": v(26.93, 101.34) * mm, "mid": v(25.58, 101.69) * mm, "end": v(24.22, 102.02) * mm});
            skArc(sketch, "E14.12.49.0", {"start": v(27.29, 98) * mm, "mid": v(27.14, 99.68) * mm, "end": v(26.93, 101.34) * mm});
            skArc(sketch, "E14.16.49.0", {"start": v(27.28, 98.04) * mm, "mid": v(28.13, 95.85) * mm, "end": v(30.07, 94.51) * mm});
            skArc(sketch, "E14.2.50.0", {"start": v(6.1, 99) * mm, "mid": v(8.4, 99.54) * mm, "end": v(9.98, 101.28) * mm});
            skArc(sketch, "E14.4.50.0", {"start": v(11.5, 104.22) * mm, "mid": v(10.71, 102.76) * mm, "end": v(9.98, 101.28) * mm});
            skArc(sketch, "E14.8.50.0", {"start": v(14.27, 103.88) * mm, "mid": v(12.89, 104.06) * mm, "end": v(11.5, 104.22) * mm});
            skArc(sketch, "E14.12.50.0", {"start": v(15.04, 100.62) * mm, "mid": v(14.68, 102.26) * mm, "end": v(14.27, 103.88) * mm});
            skArc(sketch, "E14.16.50.0", {"start": v(15.03, 100.65) * mm, "mid": v(16.14, 98.58) * mm, "end": v(18.22, 97.5) * mm});
            skCircle(sketch, "E15", {"center": v(0, 0) * mm, "radius": 55 * mm, "construction": true});
            skCircle(sketch, "E16", {"center": v(0, -55) * mm, "radius": 5 * mm});
            skCircle(sketch, "E17", {"center": v(0, 0) * mm, "radius": 91.43 * mm});
            skLineSegment(sketch, "E18.bottom", {"start": v(-8, -47) * mm, "end": v(8, -47) * mm});
            skLineSegment(sketch, "E18.left", {"start": v(-8, -47) * mm, "end": v(-8, -82.38) * mm});
            skLineSegment(sketch, "E18.right", {"start": v(8, -47) * mm, "end": v(8, -82.38) * mm});
            skArc(sketch, "E19", {"start": v(-17, -89.84) * mm, "mid": v(-10.75, -88.22) * mm, "end": v(-8, -82.38) * mm});
            skArc(sketch, "E20", {"start": v(8, -82.38) * mm, "mid": v(10.75, -88.22) * mm, "end": v(17, -89.84) * mm});
            skArc(sketch, "E21.1.0", {"start": v(80.19, -43.92) * mm, "mid": v(80.59, -37.48) * mm, "end": v(75.88, -33.07) * mm});
            skLineSegment(sketch, "E21.1.1", {"start": v(42.23, -22.13) * mm, "end": v(75.88, -33.07) * mm});
            skLineSegment(sketch, "E21.1.2", {"start": v(42.23, -22.13) * mm, "end": v(47.17, -6.92) * mm});
            skCircle(sketch, "E21.1.3", {"center": v(52.3, -17) * mm, "radius": 5 * mm});
            skLineSegment(sketch, "E21.1.4", {"start": v(47.17, -6.92) * mm, "end": v(80.82, -17.85) * mm});
            skArc(sketch, "E21.1.5", {"start": v(80.82, -17.85) * mm, "mid": v(87.23, -17.04) * mm, "end": v(90.7, -11.6) * mm});
            skArc(sketch, "E21.2.0", {"start": v(66.55, 62.7) * mm, "mid": v(60.55, 65.06) * mm, "end": v(54.9, 61.95) * mm});
            skLineSegment(sketch, "E21.2.1", {"start": v(34.1, 33.32) * mm, "end": v(54.9, 61.95) * mm});
            skLineSegment(sketch, "E21.2.2", {"start": v(34.1, 33.32) * mm, "end": v(21.15, 42.73) * mm});
            skCircle(sketch, "E21.2.3", {"center": v(32.33, 44.5) * mm, "radius": 5 * mm});
            skLineSegment(sketch, "E21.2.4", {"start": v(21.15, 42.73) * mm, "end": v(41.95, 71.35) * mm});
            skArc(sketch, "E21.2.5", {"start": v(41.95, 71.35) * mm, "mid": v(43.16, 77.7) * mm, "end": v(39.06, 82.67) * mm});
            skArc(sketch, "E21.3.0", {"start": v(-39.06, 82.67) * mm, "mid": v(-43.16, 77.7) * mm, "end": v(-41.95, 71.35) * mm});
            skLineSegment(sketch, "E21.3.1", {"start": v(-21.15, 42.73) * mm, "end": v(-41.95, 71.35) * mm});
            skLineSegment(sketch, "E21.3.2", {"start": v(-21.15, 42.73) * mm, "end": v(-34.1, 33.32) * mm});
            skCircle(sketch, "E21.3.3", {"center": v(-32.33, 44.5) * mm, "radius": 5 * mm});
            skLineSegment(sketch, "E21.3.4", {"start": v(-34.1, 33.32) * mm, "end": v(-54.9, 61.95) * mm});
            skArc(sketch, "E21.3.5", {"start": v(-54.9, 61.95) * mm, "mid": v(-60.55, 65.06) * mm, "end": v(-66.55, 62.7) * mm});
            skArc(sketch, "E21.4.0", {"start": v(-90.7, -11.6) * mm, "mid": v(-87.23, -17.04) * mm, "end": v(-80.82, -17.85) * mm});
            skLineSegment(sketch, "E21.4.1", {"start": v(-47.17, -6.92) * mm, "end": v(-80.82, -17.85) * mm});
            skLineSegment(sketch, "E21.4.2", {"start": v(-47.17, -6.92) * mm, "end": v(-42.23, -22.13) * mm});
            skCircle(sketch, "E21.4.3", {"center": v(-52.3, -17) * mm, "radius": 5 * mm});
            skLineSegment(sketch, "E21.4.4", {"start": v(-42.23, -22.13) * mm, "end": v(-75.88, -33.07) * mm});
            skArc(sketch, "E21.4.5", {"start": v(-75.88, -33.07) * mm, "mid": v(-80.59, -37.48) * mm, "end": v(-80.19, -43.92) * mm});
            skCircle(sketch, "E22", {"center": v(0, 0) * mm, "radius": 95.24 * mm});
            skArc(sketch, "E23", {"start": v(-48.46, -20.2) * mm, "mid": v(-30.86, -42.47) * mm, "end": v(-4.23, -52.33) * mm});
            skArc(sketch, "E24", {"start": v(-53.16, -21.92) * mm, "mid": v(-33.8, -46.52) * mm, "end": v(-4.42, -57.33) * mm});
            skArc(sketch, "E25.trimOffspring", {"start": v(51.07, -12.15) * mm, "mid": v(49.93, 16.22) * mm, "end": v(34.18, 39.85) * mm});
            skArc(sketch, "E26.trimOffspring", {"start": v(55.9, -13.5) * mm, "mid": v(54.69, 17.77) * mm, "end": v(37.28, 43.78) * mm});
            skArc(sketch, "E27.trimOffspring", {"start": v(-34.18, 39.85) * mm, "mid": v(-49.93, 16.22) * mm, "end": v(-51.07, -12.15) * mm});
            skArc(sketch, "E28.trimOffspring", {"start": v(-37.28, 43.78) * mm, "mid": v(-54.69, 17.77) * mm, "end": v(-55.9, -13.5) * mm});
            skArc(sketch, "E29.trimOffspring", {"start": v(27.34, 44.82) * mm, "mid": v(0, 52.5) * mm, "end": v(-27.34, 44.82) * mm});
            skArc(sketch, "E30.trimOffspring", {"start": v(30.12, 48.98) * mm, "mid": v(0, 57.5) * mm, "end": v(-30.12, 48.98) * mm});
            skArc(sketch, "E31.MirrorCS", {"start": v(48.46, -20.2) * mm, "mid": v(30.86, -42.47) * mm, "end": v(4.23, -52.33) * mm});
            skArc(sketch, "E32.MirrorCS", {"start": v(53.16, -21.92) * mm, "mid": v(33.8, -46.52) * mm, "end": v(4.42, -57.33) * mm});
            skSolve(sketch);
        }
        {
            var Q0;
            Q0=qCreatedBy(makeId("Front.planeOp"),FACE);
            var sketch = newSketch(context, id + "F1", { "sketchPlane" : qUnion([Q0])});
            skLineSegment(sketch, "E33", {"start": v(57.82, -72.41) * mm, "end": v(57.1, -72.98) * mm});
            skLineSegment(sketch, "E34", {"start": v(57.1, -72.98) * mm, "end": v(56.82, -73.15) * mm});
            skLineSegment(sketch, "E35", {"start": v(56.82, -73.15) * mm, "end": v(55.3, -74.24) * mm});
            skLineSegment(sketch, "E36", {"start": v(55.3, -74.24) * mm, "end": v(51.03, -77.37) * mm});
            skLineSegment(sketch, "E37", {"start": v(51.03, -77.37) * mm, "end": v(47.94, -79.39) * mm});
            skLineSegment(sketch, "E38", {"start": v(47.94, -79.39) * mm, "end": v(45.18, -80.98) * mm});
            skLineSegment(sketch, "E39", {"start": v(45.18, -80.98) * mm, "end": v(43.93, -81.67) * mm});
            skLineSegment(sketch, "E40", {"start": v(43.93, -81.67) * mm, "end": v(37.46, -84.65) * mm});
            skLineSegment(sketch, "E41", {"start": v(37.46, -84.65) * mm, "end": v(37.31, -84.68) * mm});
            skLineSegment(sketch, "E42", {"start": v(37.31, -84.68) * mm, "end": v(37.22, -84.06) * mm});
            skLineSegment(sketch, "E43", {"start": v(37.22, -84.06) * mm, "end": v(37.17, -81.72) * mm});
            skLineSegment(sketch, "E44", {"start": v(37.17, -81.72) * mm, "end": v(37.2, -81.52) * mm});
            skLineSegment(sketch, "E45", {"start": v(37.2, -81.52) * mm, "end": v(37.6, -80.93) * mm});
            skLineSegment(sketch, "E46", {"start": v(37.6, -80.93) * mm, "end": v(38.14, -80.6) * mm});
            skLineSegment(sketch, "E47", {"start": v(38.14, -80.6) * mm, "end": v(38.52, -80.24) * mm});
            skLineSegment(sketch, "E48", {"start": v(38.52, -80.24) * mm, "end": v(38.64, -79.82) * mm});
            skLineSegment(sketch, "E49", {"start": v(38.64, -79.82) * mm, "end": v(39.24, -79.1) * mm});
            skLineSegment(sketch, "E50", {"start": v(39.24, -79.1) * mm, "end": v(39.65, -78.59) * mm});
            skLineSegment(sketch, "E51", {"start": v(39.65, -78.59) * mm, "end": v(39.9, -77.63) * mm});
            skLineSegment(sketch, "E52", {"start": v(39.9, -77.63) * mm, "end": v(40.2, -77.36) * mm});
            skLineSegment(sketch, "E53", {"start": v(40.2, -77.36) * mm, "end": v(41.06, -77.25) * mm});
            skLineSegment(sketch, "E54", {"start": v(41.06, -77.25) * mm, "end": v(42.05, -77.04) * mm});
            skLineSegment(sketch, "E55", {"start": v(42.05, -77.04) * mm, "end": v(42.24, -76.97) * mm});
            skLineSegment(sketch, "E56", {"start": v(42.24, -76.97) * mm, "end": v(42.84, -76.94) * mm});
            skLineSegment(sketch, "E57", {"start": v(42.84, -76.94) * mm, "end": v(43.95, -77.21) * mm});
            skLineSegment(sketch, "E58", {"start": v(43.95, -77.21) * mm, "end": v(44.46, -77.53) * mm});
            skLineSegment(sketch, "E59", {"start": v(44.46, -77.53) * mm, "end": v(44.82, -77.93) * mm});
            skLineSegment(sketch, "E60", {"start": v(44.82, -77.93) * mm, "end": v(45.54, -78.86) * mm});
            skLineSegment(sketch, "E61", {"start": v(45.54, -78.86) * mm, "end": v(46.52, -78.37) * mm});
            skLineSegment(sketch, "E62", {"start": v(46.52, -78.37) * mm, "end": v(46.74, -78.2) * mm});
            skLineSegment(sketch, "E63", {"start": v(46.74, -78.2) * mm, "end": v(46.9, -77.93) * mm});
            skLineSegment(sketch, "E64", {"start": v(46.9, -77.93) * mm, "end": v(47.35, -73.44) * mm});
            skLineSegment(sketch, "E65", {"start": v(47.35, -73.44) * mm, "end": v(47.35, -72.02) * mm});
            skLineSegment(sketch, "E66", {"start": v(47.35, -72.02) * mm, "end": v(46.95, -71.35) * mm});
            skLineSegment(sketch, "E67", {"start": v(46.95, -71.35) * mm, "end": v(46.52, -71.24) * mm});
            skLineSegment(sketch, "E68", {"start": v(46.52, -71.24) * mm, "end": v(44.69, -71.36) * mm});
            skLineSegment(sketch, "E69", {"start": v(44.69, -71.36) * mm, "end": v(44.05, -71.32) * mm});
            skLineSegment(sketch, "E70", {"start": v(44.05, -71.32) * mm, "end": v(41.97, -70.97) * mm});
            skLineSegment(sketch, "E71", {"start": v(41.97, -70.97) * mm, "end": v(41.39, -70.97) * mm});
            skLineSegment(sketch, "E72", {"start": v(41.39, -70.97) * mm, "end": v(40.6, -71.24) * mm});
            skLineSegment(sketch, "E73", {"start": v(40.6, -71.24) * mm, "end": v(38.73, -71.92) * mm});
            skLineSegment(sketch, "E74", {"start": v(38.73, -71.92) * mm, "end": v(37.54, -72.26) * mm});
            skLineSegment(sketch, "E75", {"start": v(37.54, -72.26) * mm, "end": v(36.48, -72.45) * mm});
            skLineSegment(sketch, "E76", {"start": v(36.48, -72.45) * mm, "end": v(36.26, -72.4) * mm});
            skLineSegment(sketch, "E77", {"start": v(36.26, -72.4) * mm, "end": v(35.07, -72.03) * mm});
            skLineSegment(sketch, "E78", {"start": v(35.07, -72.03) * mm, "end": v(34.7, -71.97) * mm});
            skLineSegment(sketch, "E79", {"start": v(34.7, -71.97) * mm, "end": v(32.84, -71.95) * mm});
            skLineSegment(sketch, "E80", {"start": v(32.84, -71.95) * mm, "end": v(31.85, -71.75) * mm});
            skLineSegment(sketch, "E81", {"start": v(31.85, -71.75) * mm, "end": v(31.45, -71.25) * mm});
            skLineSegment(sketch, "E82", {"start": v(31.45, -71.25) * mm, "end": v(31.35, -70.68) * mm});
            skLineSegment(sketch, "E83", {"start": v(31.35, -70.68) * mm, "end": v(30.99, -70.74) * mm});
            skLineSegment(sketch, "E84", {"start": v(30.99, -70.74) * mm, "end": v(27.61, -71.27) * mm});
            skLineSegment(sketch, "E85", {"start": v(27.61, -71.27) * mm, "end": v(24.56, -72.04) * mm});
            skLineSegment(sketch, "E86", {"start": v(24.56, -72.04) * mm, "end": v(22.22, -71.68) * mm});
            skLineSegment(sketch, "E87", {"start": v(22.22, -71.68) * mm, "end": v(18, -72.08) * mm});
            skLineSegment(sketch, "E88", {"start": v(18, -72.08) * mm, "end": v(17.08, -71.9) * mm});
            skLineSegment(sketch, "E89", {"start": v(17.08, -71.9) * mm, "end": v(11.63, -68.46) * mm});
            skLineSegment(sketch, "E90", {"start": v(11.63, -68.46) * mm, "end": v(10.84, -68.17) * mm});
            skLineSegment(sketch, "E91", {"start": v(10.84, -68.17) * mm, "end": v(8, -66.78) * mm});
            skLineSegment(sketch, "E92", {"start": v(8, -66.78) * mm, "end": v(5.1, -65.42) * mm});
            skLineSegment(sketch, "E93", {"start": v(5.1, -65.42) * mm, "end": v(3.84, -64.95) * mm});
            skLineSegment(sketch, "E94", {"start": v(3.84, -64.95) * mm, "end": v(-1.7, -63.65) * mm});
            skLineSegment(sketch, "E95", {"start": v(-1.7, -63.65) * mm, "end": v(-8.1, -62.28) * mm});
            skLineSegment(sketch, "E96", {"start": v(-8.1, -62.28) * mm, "end": v(-8.97, -62) * mm});
            skLineSegment(sketch, "E97", {"start": v(-8.97, -62) * mm, "end": v(-11.16, -61.68) * mm});
            skLineSegment(sketch, "E98", {"start": v(-11.16, -61.68) * mm, "end": v(-12.2, -61.45) * mm});
            skLineSegment(sketch, "E99", {"start": v(-12.2, -61.45) * mm, "end": v(-14.72, -62.34) * mm});
            skLineSegment(sketch, "E100", {"start": v(-14.72, -62.34) * mm, "end": v(-15.44, -62.18) * mm});
            skLineSegment(sketch, "E101", {"start": v(-15.44, -62.18) * mm, "end": v(-15.69, -62.04) * mm});
            skLineSegment(sketch, "E102", {"start": v(-15.69, -62.04) * mm, "end": v(-15.85, -62.02) * mm});
            skLineSegment(sketch, "E103", {"start": v(-15.85, -62.02) * mm, "end": v(-16.88, -62.53) * mm});
            skLineSegment(sketch, "E104", {"start": v(-16.88, -62.53) * mm, "end": v(-16.96, -62.62) * mm});
            skLineSegment(sketch, "E105", {"start": v(-16.96, -62.62) * mm, "end": v(-17, -62.58) * mm});
            skLineSegment(sketch, "E106", {"start": v(-17, -62.58) * mm, "end": v(-16.83, -62.29) * mm});
            skLineSegment(sketch, "E107", {"start": v(-16.83, -62.29) * mm, "end": v(-16.75, -62.24) * mm});
            skLineSegment(sketch, "E108", {"start": v(-16.75, -62.24) * mm, "end": v(-16.2, -61.5) * mm});
            skLineSegment(sketch, "E109", {"start": v(-16.2, -61.5) * mm, "end": v(-15.2, -60.22) * mm});
            skLineSegment(sketch, "E110", {"start": v(-15.2, -60.22) * mm, "end": v(-12.64, -57.35) * mm});
            skLineSegment(sketch, "E111", {"start": v(-12.64, -57.35) * mm, "end": v(-10.53, -56.04) * mm});
            skLineSegment(sketch, "E112", {"start": v(-10.53, -56.04) * mm, "end": v(-7.63, -53.51) * mm});
            skLineSegment(sketch, "E113", {"start": v(-7.63, -53.51) * mm, "end": v(-7.06, -53.09) * mm});
            skLineSegment(sketch, "E114", {"start": v(-7.06, -53.09) * mm, "end": v(-3.19, -50.63) * mm});
            skLineSegment(sketch, "E115", {"start": v(-3.19, -50.63) * mm, "end": v(-0.72, -49.52) * mm});
            skLineSegment(sketch, "E116", {"start": v(-0.72, -49.52) * mm, "end": v(-0.18, -49.41) * mm});
            skLineSegment(sketch, "E117", {"start": v(-0.18, -49.41) * mm, "end": v(5.14, -48.5) * mm});
            skLineSegment(sketch, "E118", {"start": v(5.14, -48.5) * mm, "end": v(6.07, -48.37) * mm});
            skLineSegment(sketch, "E119", {"start": v(6.07, -48.37) * mm, "end": v(9.2, -47.74) * mm});
            skLineSegment(sketch, "E120", {"start": v(9.2, -47.74) * mm, "end": v(10.26, -47.6) * mm});
            skLineSegment(sketch, "E121", {"start": v(10.26, -47.6) * mm, "end": v(18.53, -49.67) * mm});
            skLineSegment(sketch, "E122", {"start": v(18.53, -49.67) * mm, "end": v(19.62, -49.9) * mm});
            skLineSegment(sketch, "E123", {"start": v(19.62, -49.9) * mm, "end": v(31.04, -53.18) * mm});
            skLineSegment(sketch, "E124", {"start": v(31.04, -53.18) * mm, "end": v(31.78, -53.36) * mm});
            skLineSegment(sketch, "E125", {"start": v(31.78, -53.36) * mm, "end": v(32.93, -53.16) * mm});
            skLineSegment(sketch, "E126", {"start": v(32.93, -53.16) * mm, "end": v(33.67, -52.83) * mm});
            skLineSegment(sketch, "E127", {"start": v(33.67, -52.83) * mm, "end": v(33.87, -52.68) * mm});
            skLineSegment(sketch, "E128", {"start": v(33.87, -52.68) * mm, "end": v(34.75, -51.98) * mm});
            skLineSegment(sketch, "E129", {"start": v(34.75, -51.98) * mm, "end": v(35.91, -50.67) * mm});
            skLineSegment(sketch, "E130", {"start": v(35.91, -50.67) * mm, "end": v(36.76, -49.95) * mm});
            skLineSegment(sketch, "E131", {"start": v(36.76, -49.95) * mm, "end": v(38.15, -49.16) * mm});
            skLineSegment(sketch, "E132", {"start": v(38.15, -49.16) * mm, "end": v(39.57, -48.25) * mm});
            skLineSegment(sketch, "E133", {"start": v(39.57, -48.25) * mm, "end": v(40.04, -47.8) * mm});
            skLineSegment(sketch, "E134", {"start": v(40.04, -47.8) * mm, "end": v(40.92, -46.46) * mm});
            skLineSegment(sketch, "E135", {"start": v(40.92, -46.46) * mm, "end": v(41.04, -46.18) * mm});
            skLineSegment(sketch, "E136", {"start": v(41.04, -46.18) * mm, "end": v(41.1, -45.9) * mm});
            skLineSegment(sketch, "E137", {"start": v(41.1, -45.9) * mm, "end": v(40.89, -43.37) * mm});
            skLineSegment(sketch, "E138", {"start": v(40.89, -43.37) * mm, "end": v(39.64, -30.68) * mm});
            skLineSegment(sketch, "E139", {"start": v(39.64, -30.68) * mm, "end": v(40.87, -27.5) * mm});
            skLineSegment(sketch, "E140", {"start": v(40.87, -27.5) * mm, "end": v(41.53, -25.06) * mm});
            skLineSegment(sketch, "E141", {"start": v(41.53, -25.06) * mm, "end": v(41.79, -24.1) * mm});
            skLineSegment(sketch, "E142", {"start": v(41.79, -24.1) * mm, "end": v(42.35, -22.6) * mm});
            skLineSegment(sketch, "E143", {"start": v(42.35, -22.6) * mm, "end": v(43.14, -20.72) * mm});
            skLineSegment(sketch, "E144", {"start": v(43.14, -20.72) * mm, "end": v(44.15, -17.54) * mm});
            skLineSegment(sketch, "E145", {"start": v(44.15, -17.54) * mm, "end": v(45.03, -15.94) * mm});
            skLineSegment(sketch, "E146", {"start": v(45.03, -15.94) * mm, "end": v(45.9, -14.58) * mm});
            skLineSegment(sketch, "E147", {"start": v(45.9, -14.58) * mm, "end": v(47.26, -12.52) * mm});
            skLineSegment(sketch, "E148", {"start": v(47.26, -12.52) * mm, "end": v(49.6, -9.18) * mm});
            skLineSegment(sketch, "E149", {"start": v(49.6, -9.18) * mm, "end": v(50.18, -8.57) * mm});
            skLineSegment(sketch, "E150", {"start": v(50.18, -8.57) * mm, "end": v(52.14, -7.13) * mm});
            skLineSegment(sketch, "E151", {"start": v(52.14, -7.13) * mm, "end": v(53.5, -6.38) * mm});
            skLineSegment(sketch, "E152", {"start": v(53.5, -6.38) * mm, "end": v(55.47, -4.86) * mm});
            skLineSegment(sketch, "E153", {"start": v(55.47, -4.86) * mm, "end": v(58.26, -3.5) * mm});
            skLineSegment(sketch, "E154", {"start": v(58.26, -3.5) * mm, "end": v(60.56, -2.6) * mm});
            skLineSegment(sketch, "E155", {"start": v(60.56, -2.6) * mm, "end": v(62.2, -1.88) * mm});
            skLineSegment(sketch, "E156", {"start": v(62.2, -1.88) * mm, "end": v(63.9, -0.84) * mm});
            skLineSegment(sketch, "E157", {"start": v(63.9, -0.84) * mm, "end": v(63.92, -0.94) * mm});
            skLineSegment(sketch, "E158", {"start": v(63.92, -0.94) * mm, "end": v(63.7, -2.37) * mm});
            skLineSegment(sketch, "E159", {"start": v(63.7, -2.37) * mm, "end": v(63.66, -2.53) * mm});
            skLineSegment(sketch, "E160", {"start": v(63.66, -2.53) * mm, "end": v(64, -3.4) * mm});
            skLineSegment(sketch, "E161", {"start": v(64, -3.4) * mm, "end": v(64.02, -3.48) * mm});
            skLineSegment(sketch, "E162", {"start": v(64.02, -3.48) * mm, "end": v(63.9, -3.49) * mm});
            skLineSegment(sketch, "E163", {"start": v(63.9, -3.49) * mm, "end": v(62.78, -3.72) * mm});
            skLineSegment(sketch, "E164", {"start": v(62.78, -3.72) * mm, "end": v(62.58, -3.79) * mm});
            skLineSegment(sketch, "E165", {"start": v(62.58, -3.79) * mm, "end": v(62.17, -4.69) * mm});
            skLineSegment(sketch, "E166", {"start": v(62.17, -4.69) * mm, "end": v(61.42, -7.83) * mm});
            skLineSegment(sketch, "E167", {"start": v(61.42, -7.83) * mm, "end": v(61.33, -8.3) * mm});
            skLineSegment(sketch, "E168", {"start": v(61.33, -8.3) * mm, "end": v(60.88, -12.13) * mm});
            skLineSegment(sketch, "E169", {"start": v(60.88, -12.13) * mm, "end": v(60.6, -13.68) * mm});
            skLineSegment(sketch, "E170", {"start": v(60.6, -13.68) * mm, "end": v(59.7, -17.6) * mm});
            skLineSegment(sketch, "E171", {"start": v(59.7, -17.6) * mm, "end": v(59.6, -18.08) * mm});
            skLineSegment(sketch, "E172", {"start": v(59.6, -18.08) * mm, "end": v(59.56, -19.12) * mm});
            skLineSegment(sketch, "E173", {"start": v(59.56, -19.12) * mm, "end": v(60.7, -30.73) * mm});
            skLineSegment(sketch, "E174", {"start": v(60.7, -30.73) * mm, "end": v(60.8, -32.79) * mm});
            skLineSegment(sketch, "E175", {"start": v(60.8, -32.79) * mm, "end": v(61.87, -36.06) * mm});
            skLineSegment(sketch, "E176", {"start": v(61.87, -36.06) * mm, "end": v(61.97, -36.86) * mm});
            skLineSegment(sketch, "E177", {"start": v(61.97, -36.86) * mm, "end": v(61.57, -40.64) * mm});
            skLineSegment(sketch, "E178", {"start": v(61.57, -40.64) * mm, "end": v(61.33, -41.41) * mm});
            skLineSegment(sketch, "E179", {"start": v(61.33, -41.41) * mm, "end": v(60.23, -43.48) * mm});
            skLineSegment(sketch, "E180", {"start": v(60.23, -43.48) * mm, "end": v(59.56, -45.1) * mm});
            skLineSegment(sketch, "E181", {"start": v(59.56, -45.1) * mm, "end": v(58.27, -49.26) * mm});
            skLineSegment(sketch, "E182", {"start": v(58.27, -49.26) * mm, "end": v(58.35, -49.89) * mm});
            skLineSegment(sketch, "E183", {"start": v(58.35, -49.89) * mm, "end": v(58.52, -50.2) * mm});
            skLineSegment(sketch, "E184", {"start": v(58.52, -50.2) * mm, "end": v(58.51, -51.48) * mm});
            skLineSegment(sketch, "E185", {"start": v(58.51, -51.48) * mm, "end": v(58.34, -52) * mm});
            skLineSegment(sketch, "E186", {"start": v(58.34, -52) * mm, "end": v(58.42, -52.63) * mm});
            skLineSegment(sketch, "E187", {"start": v(58.42, -52.63) * mm, "end": v(58.4, -53.06) * mm});
            skLineSegment(sketch, "E188", {"start": v(58.4, -53.06) * mm, "end": v(57.77, -55.26) * mm});
            skLineSegment(sketch, "E189", {"start": v(57.77, -55.26) * mm, "end": v(57.61, -55.6) * mm});
            skLineSegment(sketch, "E190", {"start": v(57.61, -55.6) * mm, "end": v(56.9, -56.66) * mm});
            skLineSegment(sketch, "E191", {"start": v(56.9, -56.66) * mm, "end": v(55.95, -58.63) * mm});
            skLineSegment(sketch, "E192", {"start": v(55.95, -58.63) * mm, "end": v(55.87, -59.15) * mm});
            skLineSegment(sketch, "E193", {"start": v(55.87, -59.15) * mm, "end": v(55.93, -60.62) * mm});
            skLineSegment(sketch, "E194", {"start": v(55.93, -60.62) * mm, "end": v(56.24, -61.49) * mm});
            skLineSegment(sketch, "E195", {"start": v(56.24, -61.49) * mm, "end": v(56.27, -61.53) * mm});
            skLineSegment(sketch, "E196", {"start": v(56.27, -61.53) * mm, "end": v(56.64, -61.83) * mm});
            skLineSegment(sketch, "E197", {"start": v(56.64, -61.83) * mm, "end": v(58.03, -62.51) * mm});
            skLineSegment(sketch, "E198", {"start": v(58.03, -62.51) * mm, "end": v(60.36, -63.7) * mm});
            skLineSegment(sketch, "E199", {"start": v(60.36, -63.7) * mm, "end": v(63.5, -64.83) * mm});
            skLineSegment(sketch, "E200", {"start": v(63.5, -64.83) * mm, "end": v(63.75, -64.75) * mm});
            skLineSegment(sketch, "E201", {"start": v(63.75, -64.75) * mm, "end": v(65.07, -63.59) * mm});
            skLineSegment(sketch, "E202", {"start": v(65.07, -63.59) * mm, "end": v(65.21, -63.43) * mm});
            skLineSegment(sketch, "E203", {"start": v(65.21, -63.43) * mm, "end": v(64.94, -63.26) * mm});
            skLineSegment(sketch, "E204", {"start": v(64.94, -63.26) * mm, "end": v(64.57, -62.83) * mm});
            skLineSegment(sketch, "E205", {"start": v(64.57, -62.83) * mm, "end": v(64.32, -62.3) * mm});
            skLineSegment(sketch, "E206", {"start": v(64.32, -62.3) * mm, "end": v(64.26, -61.58) * mm});
            skLineSegment(sketch, "E207", {"start": v(64.26, -61.58) * mm, "end": v(64.5, -61.29) * mm});
            skLineSegment(sketch, "E208", {"start": v(64.5, -61.29) * mm, "end": v(64.91, -60.61) * mm});
            skLineSegment(sketch, "E209", {"start": v(64.91, -60.61) * mm, "end": v(64.9, -60.46) * mm});
            skLineSegment(sketch, "E210", {"start": v(64.9, -60.46) * mm, "end": v(64.81, -59.44) * mm});
            skLineSegment(sketch, "E211", {"start": v(64.81, -59.44) * mm, "end": v(64.83, -59.2) * mm});
            skLineSegment(sketch, "E212", {"start": v(64.83, -59.2) * mm, "end": v(65.1, -58.61) * mm});
            skLineSegment(sketch, "E213", {"start": v(65.1, -58.61) * mm, "end": v(65.4, -58.37) * mm});
            skLineSegment(sketch, "E214", {"start": v(65.4, -58.37) * mm, "end": v(66.28, -58.1) * mm});
            skLineSegment(sketch, "E215", {"start": v(66.28, -58.1) * mm, "end": v(66.63, -57.98) * mm});
            skLineSegment(sketch, "E216", {"start": v(66.63, -57.98) * mm, "end": v(66.64, -57.78) * mm});
            skLineSegment(sketch, "E217", {"start": v(66.64, -57.78) * mm, "end": v(66.7, -57.25) * mm});
            skLineSegment(sketch, "E218", {"start": v(66.7, -57.25) * mm, "end": v(67.08, -56.86) * mm});
            skLineSegment(sketch, "E219", {"start": v(67.08, -56.86) * mm, "end": v(67.19, -56.76) * mm});
            skLineSegment(sketch, "E220", {"start": v(67.19, -56.76) * mm, "end": v(67.75, -56.53) * mm});
            skLineSegment(sketch, "E221", {"start": v(67.75, -56.53) * mm, "end": v(68.14, -56.53) * mm});
            skLineSegment(sketch, "E222", {"start": v(68.14, -56.53) * mm, "end": v(68.58, -56.6) * mm});
            skLineSegment(sketch, "E223", {"start": v(68.58, -56.6) * mm, "end": v(69.37, -56.9) * mm});
            skLineSegment(sketch, "E224", {"start": v(69.37, -56.9) * mm, "end": v(69.54, -56.52) * mm});
            skLineSegment(sketch, "E225", {"start": v(69.54, -56.52) * mm, "end": v(70.13, -56.48) * mm});
            skLineSegment(sketch, "E226", {"start": v(70.13, -56.48) * mm, "end": v(70.33, -56.5) * mm});
            skLineSegment(sketch, "E227", {"start": v(70.33, -56.5) * mm, "end": v(71.32, -57.02) * mm});
            skLineSegment(sketch, "E228", {"start": v(71.32, -57.02) * mm, "end": v(72.28, -57.64) * mm});
            skLineSegment(sketch, "E229", {"start": v(72.28, -57.64) * mm, "end": v(72.6, -57.86) * mm});
            skLineSegment(sketch, "E230", {"start": v(72.6, -57.86) * mm, "end": v(72.49, -58.02) * mm});
            skLineSegment(sketch, "E231", {"start": v(72.49, -58.02) * mm, "end": v(70.01, -60.82) * mm});
            skLineSegment(sketch, "E232", {"start": v(70.01, -60.82) * mm, "end": v(66.6, -64.7) * mm});
            skLineSegment(sketch, "E233", {"start": v(66.6, -64.7) * mm, "end": v(65.73, -65.66) * mm});
            skLineSegment(sketch, "E234", {"start": v(65.73, -65.66) * mm, "end": v(62.5, -68.4) * mm});
            skLineSegment(sketch, "E235", {"start": v(62.5, -68.4) * mm, "end": v(58.67, -71.64) * mm});
            skLineSegment(sketch, "E236", {"start": v(58.67, -71.64) * mm, "end": v(57.82, -72.41) * mm});
            skLineSegment(sketch, "E237", {"start": v(35.69, -61.97) * mm, "end": v(36.07, -60.95) * mm});
            skLineSegment(sketch, "E238", {"start": v(36.07, -60.95) * mm, "end": v(37.04, -58.68) * mm});
            skLineSegment(sketch, "E239", {"start": v(37.04, -58.68) * mm, "end": v(38.06, -57.6) * mm});
            skLineSegment(sketch, "E240", {"start": v(38.06, -57.6) * mm, "end": v(39.7, -56.59) * mm});
            skLineSegment(sketch, "E241", {"start": v(39.7, -56.59) * mm, "end": v(40.66, -56.37) * mm});
            skLineSegment(sketch, "E242", {"start": v(40.66, -56.37) * mm, "end": v(41.85, -56.44) * mm});
            skLineSegment(sketch, "E243", {"start": v(41.85, -56.44) * mm, "end": v(41.9, -56.36) * mm});
            skLineSegment(sketch, "E244", {"start": v(41.9, -56.36) * mm, "end": v(42.55, -54.81) * mm});
            skLineSegment(sketch, "E245", {"start": v(42.55, -54.81) * mm, "end": v(43.12, -53.92) * mm});
            skLineSegment(sketch, "E246", {"start": v(43.12, -53.92) * mm, "end": v(43.9, -53.25) * mm});
            skLineSegment(sketch, "E247", {"start": v(43.9, -53.25) * mm, "end": v(44.54, -52.8) * mm});
            skLineSegment(sketch, "E248", {"start": v(44.54, -52.8) * mm, "end": v(45.47, -52.28) * mm});
            skLineSegment(sketch, "E249", {"start": v(45.47, -52.28) * mm, "end": v(46.99, -51.62) * mm});
            skLineSegment(sketch, "E250", {"start": v(46.99, -51.62) * mm, "end": v(48.17, -51.33) * mm});
            skLineSegment(sketch, "E251", {"start": v(48.17, -51.33) * mm, "end": v(49, -51.34) * mm});
            skLineSegment(sketch, "E252", {"start": v(49, -51.34) * mm, "end": v(50.35, -51.74) * mm});
            skLineSegment(sketch, "E253", {"start": v(50.35, -51.74) * mm, "end": v(51.1, -52.06) * mm});
            skLineSegment(sketch, "E254", {"start": v(51.1, -52.06) * mm, "end": v(52.08, -52.64) * mm});
            skLineSegment(sketch, "E255", {"start": v(52.08, -52.64) * mm, "end": v(52.38, -52.8) * mm});
            skLineSegment(sketch, "E256", {"start": v(52.38, -52.8) * mm, "end": v(52.29, -52.28) * mm});
            skLineSegment(sketch, "E257", {"start": v(52.29, -52.28) * mm, "end": v(51.39, -48.7) * mm});
            skLineSegment(sketch, "E258", {"start": v(51.39, -48.7) * mm, "end": v(50.83, -48.06) * mm});
            skLineSegment(sketch, "E259", {"start": v(50.83, -48.06) * mm, "end": v(47.95, -46.9) * mm});
            skLineSegment(sketch, "E260", {"start": v(47.95, -46.9) * mm, "end": v(47.55, -46.72) * mm});
            skLineSegment(sketch, "E261", {"start": v(47.55, -46.72) * mm, "end": v(49, -46.11) * mm});
            skLineSegment(sketch, "E262", {"start": v(49, -46.11) * mm, "end": v(50.26, -45.93) * mm});
            skLineSegment(sketch, "E263", {"start": v(50.26, -45.93) * mm, "end": v(50.28, -45.64) * mm});
            skLineSegment(sketch, "E264", {"start": v(50.28, -45.64) * mm, "end": v(50.36, -44.19) * mm});
            skLineSegment(sketch, "E265", {"start": v(50.36, -44.19) * mm, "end": v(50.65, -43.33) * mm});
            skLineSegment(sketch, "E266", {"start": v(50.65, -43.33) * mm, "end": v(51.45, -42.12) * mm});
            skLineSegment(sketch, "E267", {"start": v(51.45, -42.12) * mm, "end": v(51.8, -41.2) * mm});
            skLineSegment(sketch, "E268", {"start": v(51.8, -41.2) * mm, "end": v(52.22, -38.07) * mm});
            skLineSegment(sketch, "E269", {"start": v(52.22, -38.07) * mm, "end": v(51.49, -35.09) * mm});
            skLineSegment(sketch, "E270", {"start": v(51.49, -35.09) * mm, "end": v(50.82, -26.55) * mm});
            skLineSegment(sketch, "E271", {"start": v(50.82, -26.55) * mm, "end": v(50.6, -24.38) * mm});
            skLineSegment(sketch, "E272", {"start": v(50.6, -24.38) * mm, "end": v(50.14, -22.02) * mm});
            skLineSegment(sketch, "E273", {"start": v(50.14, -22.02) * mm, "end": v(50.14, -21.5) * mm});
            skLineSegment(sketch, "E274", {"start": v(52.65, -12) * mm, "end": v(52.82, -11.6) * mm});
            skLineSegment(sketch, "E275", {"start": v(52.82, -11.6) * mm, "end": v(53.1, -11.07) * mm});
            skLineSegment(sketch, "E276", {"start": v(53.1, -11.07) * mm, "end": v(54.92, -8.4) * mm});
            skLineSegment(sketch, "E277", {"start": v(54.92, -8.4) * mm, "end": v(55.8, -7.44) * mm});
            skLineSegment(sketch, "E278", {"start": v(55.8, -7.44) * mm, "end": v(58.59, -5.18) * mm});
            skLineSegment(sketch, "E279", {"start": v(58.59, -5.18) * mm, "end": v(58.8, -4.98) * mm});
            skLineSegment(sketch, "E280", {"start": v(58.8, -4.98) * mm, "end": v(58.77, -4.93) * mm});
            skLineSegment(sketch, "E281", {"start": v(58.77, -4.93) * mm, "end": v(58.33, -5.1) * mm});
            skLineSegment(sketch, "E282", {"start": v(58.33, -5.1) * mm, "end": v(56.25, -6) * mm});
            skLineSegment(sketch, "E283", {"start": v(56.25, -6) * mm, "end": v(52.72, -8.4) * mm});
            skLineSegment(sketch, "E284", {"start": v(52.72, -8.4) * mm, "end": v(52.05, -9) * mm});
            skLineSegment(sketch, "E285", {"start": v(52.05, -9) * mm, "end": v(49.49, -12.87) * mm});
            skLineSegment(sketch, "E286", {"start": v(47.03, -16.59) * mm, "end": v(46.6, -17.32) * mm});
            skLineSegment(sketch, "E287", {"start": v(46.6, -17.32) * mm, "end": v(42.87, -28.6) * mm});
            skLineSegment(sketch, "E288", {"start": v(42.87, -28.6) * mm, "end": v(42.74, -29.15) * mm});
            skLineSegment(sketch, "E289", {"start": v(42.74, -29.15) * mm, "end": v(42.43, -34.98) * mm});
            skLineSegment(sketch, "E290", {"start": v(42.43, -34.98) * mm, "end": v(43.64, -43.22) * mm});
            skLineSegment(sketch, "E291", {"start": v(43.64, -43.22) * mm, "end": v(43.8, -44.15) * mm});
            skLineSegment(sketch, "E292", {"start": v(43.8, -44.15) * mm, "end": v(43.88, -45.68) * mm});
            skLineSegment(sketch, "E293", {"start": v(43.88, -45.68) * mm, "end": v(44, -46.38) * mm});
            skLineSegment(sketch, "E294", {"start": v(44, -46.38) * mm, "end": v(44.97, -48.17) * mm});
            skLineSegment(sketch, "E295", {"start": v(44.97, -48.17) * mm, "end": v(45.7, -48.54) * mm});
            skLineSegment(sketch, "E296", {"start": v(45.7, -48.54) * mm, "end": v(46.13, -48.57) * mm});
            skLineSegment(sketch, "E297", {"start": v(46.13, -48.57) * mm, "end": v(46.75, -48.78) * mm});
            skLineSegment(sketch, "E298", {"start": v(46.75, -48.78) * mm, "end": v(46.84, -49.59) * mm});
            skLineSegment(sketch, "E299", {"start": v(46.84, -49.59) * mm, "end": v(46.12, -49.62) * mm});
            skLineSegment(sketch, "E300", {"start": v(46.12, -49.62) * mm, "end": v(44.13, -49.55) * mm});
            skLineSegment(sketch, "E301", {"start": v(44.13, -49.55) * mm, "end": v(43.85, -49.57) * mm});
            skLineSegment(sketch, "E302", {"start": v(43.85, -49.57) * mm, "end": v(41.74, -50.1) * mm});
            skLineSegment(sketch, "E303", {"start": v(41.74, -50.1) * mm, "end": v(40.38, -50.67) * mm});
            skLineSegment(sketch, "E304", {"start": v(40.38, -50.67) * mm, "end": v(38.26, -51.85) * mm});
            skLineSegment(sketch, "E305", {"start": v(38.26, -51.85) * mm, "end": v(37.94, -52.1) * mm});
            skLineSegment(sketch, "E306", {"start": v(37.94, -52.1) * mm, "end": v(37.24, -52.86) * mm});
            skLineSegment(sketch, "E307", {"start": v(37.24, -52.86) * mm, "end": v(36.27, -54.07) * mm});
            skLineSegment(sketch, "E308", {"start": v(36.27, -54.07) * mm, "end": v(35.24, -55.8) * mm});
            skLineSegment(sketch, "E309", {"start": v(35.24, -55.8) * mm, "end": v(34.94, -56.44) * mm});
            skLineSegment(sketch, "E310", {"start": v(34.94, -56.44) * mm, "end": v(34.39, -58) * mm});
            skLineSegment(sketch, "E311", {"start": v(34.39, -58) * mm, "end": v(34.28, -58.8) * mm});
            skLineSegment(sketch, "E312", {"start": v(34.28, -58.8) * mm, "end": v(34.51, -61.42) * mm});
            skLineSegment(sketch, "E313", {"start": v(34.51, -61.42) * mm, "end": v(34.55, -61.73) * mm});
            skLineSegment(sketch, "E314", {"start": v(34.55, -61.73) * mm, "end": v(35.69, -61.97) * mm});
            skLineSegment(sketch, "E315", {"start": v(-13.15, -59.87) * mm, "end": v(-13.12, -59.91) * mm});
            skLineSegment(sketch, "E316", {"start": v(-13.12, -59.91) * mm, "end": v(-12.87, -59.8) * mm});
            skLineSegment(sketch, "E317", {"start": v(-12.87, -59.8) * mm, "end": v(-8.54, -57.57) * mm});
            skLineSegment(sketch, "E318", {"start": v(-8.54, -57.57) * mm, "end": v(-7.57, -57.25) * mm});
            skLineSegment(sketch, "E319", {"start": v(-7.57, -57.25) * mm, "end": v(-6.32, -57.04) * mm});
            skLineSegment(sketch, "E320", {"start": v(-6.32, -57.04) * mm, "end": v(-6, -56.95) * mm});
            skLineSegment(sketch, "E321", {"start": v(-6, -56.95) * mm, "end": v(-5.02, -56.37) * mm});
            skLineSegment(sketch, "E322", {"start": v(-5.02, -56.37) * mm, "end": v(-4.84, -56.26) * mm});
            skLineSegment(sketch, "E323", {"start": v(4.87, -56.15) * mm, "end": v(6.18, -56.67) * mm});
            skLineSegment(sketch, "E324", {"start": v(6.18, -56.67) * mm, "end": v(6.52, -56.79) * mm});
            skLineSegment(sketch, "E325", {"start": v(6.52, -56.79) * mm, "end": v(9.7, -58.4) * mm});
            skLineSegment(sketch, "E326", {"start": v(9.7, -58.4) * mm, "end": v(11.43, -59.1) * mm});
            skLineSegment(sketch, "E327", {"start": v(11.43, -59.1) * mm, "end": v(12.83, -59.75) * mm});
            skLineSegment(sketch, "E328", {"start": v(12.83, -59.75) * mm, "end": v(13.88, -60.27) * mm});
            skLineSegment(sketch, "E329", {"start": v(13.88, -60.27) * mm, "end": v(15.9, -61.42) * mm});
            skLineSegment(sketch, "E330", {"start": v(15.9, -61.42) * mm, "end": v(16.72, -61.64) * mm});
            skLineSegment(sketch, "E331", {"start": v(16.72, -61.64) * mm, "end": v(23.14, -61.55) * mm});
            skLineSegment(sketch, "E332", {"start": v(23.14, -61.55) * mm, "end": v(23.92, -61.63) * mm});
            skLineSegment(sketch, "E333", {"start": v(23.92, -61.63) * mm, "end": v(25.65, -61.56) * mm});
            skLineSegment(sketch, "E334", {"start": v(25.65, -61.56) * mm, "end": v(27.48, -61.39) * mm});
            skLineSegment(sketch, "E335", {"start": v(27.48, -61.39) * mm, "end": v(27.92, -61.17) * mm});
            skLineSegment(sketch, "E336", {"start": v(27.92, -61.17) * mm, "end": v(28.5, -60.52) * mm});
            skLineSegment(sketch, "E337", {"start": v(28.5, -60.52) * mm, "end": v(29, -59.97) * mm});
            skLineSegment(sketch, "E338", {"start": v(29, -59.97) * mm, "end": v(29.28, -60.44) * mm});
            skLineSegment(sketch, "E339", {"start": v(29.28, -60.44) * mm, "end": v(29.35, -61.23) * mm});
            skLineSegment(sketch, "E340", {"start": v(29.35, -61.23) * mm, "end": v(29.6, -61.95) * mm});
            skLineSegment(sketch, "E341", {"start": v(29.6, -61.95) * mm, "end": v(30.07, -61.98) * mm});
            skLineSegment(sketch, "E342", {"start": v(30.07, -61.98) * mm, "end": v(30.66, -60.93) * mm});
            skLineSegment(sketch, "E343", {"start": v(30.66, -60.93) * mm, "end": v(30.72, -60.71) * mm});
            skLineSegment(sketch, "E344", {"start": v(30.72, -60.71) * mm, "end": v(31.18, -57.79) * mm});
            skLineSegment(sketch, "E345", {"start": v(31.18, -57.79) * mm, "end": v(31.17, -57.57) * mm});
            skLineSegment(sketch, "E346", {"start": v(31.17, -57.57) * mm, "end": v(30.6, -56.6) * mm});
            skLineSegment(sketch, "E347", {"start": v(30.6, -56.6) * mm, "end": v(30.52, -56.5) * mm});
            skLineSegment(sketch, "E348", {"start": v(30.52, -56.5) * mm, "end": v(29.82, -55.4) * mm});
            skLineSegment(sketch, "E349", {"start": v(29.82, -55.4) * mm, "end": v(29.23, -54.76) * mm});
            skLineSegment(sketch, "E350", {"start": v(29.23, -54.76) * mm, "end": v(20.24, -52.7) * mm});
            skLineSegment(sketch, "E351", {"start": v(20.24, -52.7) * mm, "end": v(19.24, -52.44) * mm});
            skLineSegment(sketch, "E352", {"start": v(19.24, -52.44) * mm, "end": v(17.59, -52.33) * mm});
            skLineSegment(sketch, "E353", {"start": v(17.59, -52.33) * mm, "end": v(13.44, -51.84) * mm});
            skLineSegment(sketch, "E354", {"start": v(13.44, -51.84) * mm, "end": v(13.11, -51.8) * mm});
            skLineSegment(sketch, "E355", {"start": v(13.11, -51.8) * mm, "end": v(7.32, -50.01) * mm});
            skLineSegment(sketch, "E356", {"start": v(7.32, -50.01) * mm, "end": v(6.48, -50.12) * mm});
            skLineSegment(sketch, "E357", {"start": v(6.48, -50.12) * mm, "end": v(3.67, -50.72) * mm});
            skLineSegment(sketch, "E358", {"start": v(3.67, -50.72) * mm, "end": v(2.74, -50.82) * mm});
            skLineSegment(sketch, "E359", {"start": v(-4.88, -53.92) * mm, "end": v(-4.9, -53.94) * mm});
            skLineSegment(sketch, "E360", {"start": v(-4.9, -53.94) * mm, "end": v(-7.2, -55.67) * mm});
            skLineSegment(sketch, "E361", {"start": v(-7.2, -55.67) * mm, "end": v(-12.82, -59.56) * mm});
            skLineSegment(sketch, "E362", {"start": v(-12.82, -59.56) * mm, "end": v(-13.15, -59.87) * mm});
            skLineSegment(sketch, "E363", {"start": v(57.09, -31.17) * mm, "end": v(57.08, -31.56) * mm});
            skLineSegment(sketch, "E364", {"start": v(57.08, -31.56) * mm, "end": v(57.88, -38.14) * mm});
            skLineSegment(sketch, "E365", {"start": v(57.88, -38.14) * mm, "end": v(57.88, -38.92) * mm});
            skLineSegment(sketch, "E366", {"start": v(57.88, -38.92) * mm, "end": v(57.1, -42.3) * mm});
            skLineSegment(sketch, "E367", {"start": v(57.1, -42.3) * mm, "end": v(56.73, -43.1) * mm});
            skLineSegment(sketch, "E368", {"start": v(56.73, -43.1) * mm, "end": v(56.12, -43.92) * mm});
            skLineSegment(sketch, "E369", {"start": v(56.12, -43.92) * mm, "end": v(55.9, -44.43) * mm});
            skLineSegment(sketch, "E370", {"start": v(55.9, -44.43) * mm, "end": v(55.78, -45.95) * mm});
            skLineSegment(sketch, "E371", {"start": v(55.78, -45.95) * mm, "end": v(55.9, -46.5) * mm});
            skLineSegment(sketch, "E372", {"start": v(55.9, -46.5) * mm, "end": v(56.58, -47.3) * mm});
            skLineSegment(sketch, "E373", {"start": v(56.58, -47.3) * mm, "end": v(57, -46.7) * mm});
            skLineSegment(sketch, "E374", {"start": v(57, -46.7) * mm, "end": v(57.59, -44.83) * mm});
            skLineSegment(sketch, "E375", {"start": v(57.59, -44.83) * mm, "end": v(58.33, -43.27) * mm});
            skLineSegment(sketch, "E376", {"start": v(58.33, -43.27) * mm, "end": v(58.75, -42.34) * mm});
            skLineSegment(sketch, "E377", {"start": v(58.75, -42.34) * mm, "end": v(59.37, -40.62) * mm});
            skLineSegment(sketch, "E378", {"start": v(59.37, -40.62) * mm, "end": v(59.45, -40.27) * mm});
            skLineSegment(sketch, "E379", {"start": v(59.45, -40.27) * mm, "end": v(59.84, -37.5) * mm});
            skLineSegment(sketch, "E380", {"start": v(59.84, -37.5) * mm, "end": v(59.73, -36.29) * mm});
            skLineSegment(sketch, "E381", {"start": v(59.73, -36.29) * mm, "end": v(58.85, -31.3) * mm});
            skLineSegment(sketch, "E382", {"start": v(58.85, -31.3) * mm, "end": v(58.65, -27.96) * mm});
            skLineSegment(sketch, "E383", {"start": v(58.65, -27.96) * mm, "end": v(57.8, -20.2) * mm});
            skLineSegment(sketch, "E384", {"start": v(57.8, -20.2) * mm, "end": v(57.78, -19.38) * mm});
            skLineSegment(sketch, "E385", {"start": v(57.78, -19.38) * mm, "end": v(59.59, -8.12) * mm});
            skLineSegment(sketch, "E386", {"start": v(59.59, -8.12) * mm, "end": v(59.72, -7.5) * mm});
            skLineSegment(sketch, "E387", {"start": v(59.72, -7.5) * mm, "end": v(60.1, -6.02) * mm});
            skLineSegment(sketch, "E388", {"start": v(60.1, -6.02) * mm, "end": v(60.12, -5.63) * mm});
            skLineSegment(sketch, "E389", {"start": v(60.12, -5.63) * mm, "end": v(60.01, -5.79) * mm});
            skLineSegment(sketch, "E390", {"start": v(60.01, -5.79) * mm, "end": v(59.14, -8) * mm});
            skLineSegment(sketch, "E391", {"start": v(59.14, -8) * mm, "end": v(58.73, -9.18) * mm});
            skLineSegment(sketch, "E392", {"start": v(58.73, -9.18) * mm, "end": v(58.48, -9.74) * mm});
            skLineSegment(sketch, "E393", {"start": v(58.48, -9.74) * mm, "end": v(58.06, -11.13) * mm});
            skLineSegment(sketch, "E394", {"start": v(58.06, -11.13) * mm, "end": v(57.83, -12.04) * mm});
            skLineSegment(sketch, "E395", {"start": v(57.83, -12.04) * mm, "end": v(56.72, -14.64) * mm});
            skLineSegment(sketch, "E396", {"start": v(56.34, -19.95) * mm, "end": v(56.34, -20.29) * mm});
            skLineSegment(sketch, "E397", {"start": v(56.34, -20.29) * mm, "end": v(56.25, -21.58) * mm});
            skLineSegment(sketch, "E398", {"start": v(56.25, -21.58) * mm, "end": v(56.37, -24.08) * mm});
            skLineSegment(sketch, "E399", {"start": v(56.37, -24.08) * mm, "end": v(56.5, -24.9) * mm});
            skLineSegment(sketch, "E400", {"start": v(56.5, -24.9) * mm, "end": v(57.02, -27.7) * mm});
            skLineSegment(sketch, "E401", {"start": v(57.02, -27.7) * mm, "end": v(57.07, -28.28) * mm});
            skLineSegment(sketch, "E402", {"start": v(57.07, -28.28) * mm, "end": v(57, -29.77) * mm});
            skLineSegment(sketch, "E403", {"start": v(57, -29.77) * mm, "end": v(56.66, -30.3) * mm});
            skLineSegment(sketch, "E404", {"start": v(56.66, -30.3) * mm, "end": v(55.86, -30.93) * mm});
            skLineSegment(sketch, "E405", {"start": v(55.86, -30.93) * mm, "end": v(57.09, -31.17) * mm});
            skLineSegment(sketch, "E406", {"start": v(29.23, -68.98) * mm, "end": v(29.08, -68.83) * mm});
            skLineSegment(sketch, "E407", {"start": v(29.08, -68.83) * mm, "end": v(27.93, -67.8) * mm});
            skLineSegment(sketch, "E408", {"start": v(27.93, -67.8) * mm, "end": v(27.32, -67.5) * mm});
            skLineSegment(sketch, "E409", {"start": v(27.32, -67.5) * mm, "end": v(24.97, -67.2) * mm});
            skLineSegment(sketch, "E410", {"start": v(24.97, -67.2) * mm, "end": v(24.16, -67.16) * mm});
            skLineSegment(sketch, "E411", {"start": v(24.16, -67.16) * mm, "end": v(23.83, -67.11) * mm});
            skLineSegment(sketch, "E412", {"start": v(23.83, -67.11) * mm, "end": v(19.12, -67.32) * mm});
            skLineSegment(sketch, "E413", {"start": v(19.12, -67.32) * mm, "end": v(18.37, -67.2) * mm});
            skLineSegment(sketch, "E414", {"start": v(18.37, -67.2) * mm, "end": v(17.4, -67) * mm});
            skLineSegment(sketch, "E415", {"start": v(17.4, -67) * mm, "end": v(14.07, -65.37) * mm});
            skLineSegment(sketch, "E416", {"start": v(14.07, -65.37) * mm, "end": v(13.55, -64.99) * mm});
            skLineSegment(sketch, "E417", {"start": v(13.55, -64.99) * mm, "end": v(12.76, -62.87) * mm});
            skLineSegment(sketch, "E418", {"start": v(12.76, -62.87) * mm, "end": v(12.68, -62.63) * mm});
            skLineSegment(sketch, "E419", {"start": v(12.68, -62.63) * mm, "end": v(12.03, -64.56) * mm});
            skLineSegment(sketch, "E420", {"start": v(12.03, -64.56) * mm, "end": v(11.88, -64.54) * mm});
            skLineSegment(sketch, "E421", {"start": v(11.88, -64.54) * mm, "end": v(10.64, -64.15) * mm});
            skLineSegment(sketch, "E422", {"start": v(10.64, -64.15) * mm, "end": v(8.5, -63.26) * mm});
            skLineSegment(sketch, "E423", {"start": v(8.5, -63.26) * mm, "end": v(6.72, -62.57) * mm});
            skLineSegment(sketch, "E424", {"start": v(6.72, -62.57) * mm, "end": v(3.41, -61.65) * mm});
            skLineSegment(sketch, "E425", {"start": v(3.41, -61.65) * mm, "end": v(1.26, -61.02) * mm});
            skLineSegment(sketch, "E426", {"start": v(1.26, -61.02) * mm, "end": v(-3.78, -59.17) * mm});
            skLineSegment(sketch, "E427", {"start": v(-3.78, -59.17) * mm, "end": v(-4.71, -59.05) * mm});
            skLineSegment(sketch, "E428", {"start": v(-4.71, -59.05) * mm, "end": v(-6.38, -59.68) * mm});
            skLineSegment(sketch, "E429", {"start": v(-6.38, -59.68) * mm, "end": v(-7.34, -59.77) * mm});
            skLineSegment(sketch, "E430", {"start": v(-7.34, -59.77) * mm, "end": v(-10.5, -59.65) * mm});
            skLineSegment(sketch, "E431", {"start": v(-10.5, -59.65) * mm, "end": v(-10.95, -59.73) * mm});
            skLineSegment(sketch, "E432", {"start": v(-10.95, -59.73) * mm, "end": v(-9.47, -60.08) * mm});
            skLineSegment(sketch, "E433", {"start": v(-9.47, -60.08) * mm, "end": v(-4.7, -60.78) * mm});
            skLineSegment(sketch, "E434", {"start": v(-4.7, -60.78) * mm, "end": v(1.18, -62.5) * mm});
            skLineSegment(sketch, "E435", {"start": v(1.18, -62.5) * mm, "end": v(4.74, -63.68) * mm});
            skLineSegment(sketch, "E436", {"start": v(4.74, -63.68) * mm, "end": v(6.37, -64.17) * mm});
            skLineSegment(sketch, "E437", {"start": v(6.37, -64.17) * mm, "end": v(8.59, -64.93) * mm});
            skLineSegment(sketch, "E438", {"start": v(8.59, -64.93) * mm, "end": v(10.65, -65.94) * mm});
            skLineSegment(sketch, "E439", {"start": v(10.65, -65.94) * mm, "end": v(11.73, -66.45) * mm});
            skLineSegment(sketch, "E440", {"start": v(11.73, -66.45) * mm, "end": v(15, -68.1) * mm});
            skLineSegment(sketch, "E441", {"start": v(15, -68.1) * mm, "end": v(18.58, -69.79) * mm});
            skLineSegment(sketch, "E442", {"start": v(18.58, -69.79) * mm, "end": v(21.32, -69.15) * mm});
            skLineSegment(sketch, "E443", {"start": v(21.32, -69.15) * mm, "end": v(23.04, -69.6) * mm});
            skLineSegment(sketch, "E444", {"start": v(23.04, -69.6) * mm, "end": v(24.38, -69.77) * mm});
            skLineSegment(sketch, "E445", {"start": v(24.38, -69.77) * mm, "end": v(28.77, -69.02) * mm});
            skLineSegment(sketch, "E446", {"start": v(28.77, -69.02) * mm, "end": v(29.23, -68.98) * mm});
            skLineSegment(sketch, "E447", {"start": v(49.2, -63) * mm, "end": v(48.73, -63.06) * mm});
            skLineSegment(sketch, "E448", {"start": v(48.73, -63.06) * mm, "end": v(48.1, -63.26) * mm});
            skLineSegment(sketch, "E449", {"start": v(48.1, -63.26) * mm, "end": v(47.52, -63.81) * mm});
            skLineSegment(sketch, "E450", {"start": v(47.52, -63.81) * mm, "end": v(47.07, -64.5) * mm});
            skLineSegment(sketch, "E451", {"start": v(47.07, -64.5) * mm, "end": v(46.77, -65.28) * mm});
            skLineSegment(sketch, "E452", {"start": v(46.77, -65.28) * mm, "end": v(46.72, -65.38) * mm});
            skLineSegment(sketch, "E453", {"start": v(46.72, -65.38) * mm, "end": v(46.2, -65.22) * mm});
            skLineSegment(sketch, "E454", {"start": v(46.2, -65.22) * mm, "end": v(45.4, -66.31) * mm});
            skLineSegment(sketch, "E455", {"start": v(45.4, -66.31) * mm, "end": v(45.42, -66.72) * mm});
            skLineSegment(sketch, "E456", {"start": v(45.42, -66.72) * mm, "end": v(46.43, -68.09) * mm});
            skLineSegment(sketch, "E457", {"start": v(46.43, -68.09) * mm, "end": v(46.7, -68.36) * mm});
            skLineSegment(sketch, "E458", {"start": v(46.7, -68.36) * mm, "end": v(46.8, -68.23) * mm});
            skLineSegment(sketch, "E459", {"start": v(46.8, -68.23) * mm, "end": v(47.74, -66.97) * mm});
            skLineSegment(sketch, "E460", {"start": v(47.74, -66.97) * mm, "end": v(47.89, -66.74) * mm});
            skLineSegment(sketch, "E461", {"start": v(47.89, -66.74) * mm, "end": v(48.14, -66.28) * mm});
            skLineSegment(sketch, "E462", {"start": v(48.14, -66.28) * mm, "end": v(48.62, -66.54) * mm});
            skLineSegment(sketch, "E463", {"start": v(48.62, -66.54) * mm, "end": v(49.09, -66.49) * mm});
            skLineSegment(sketch, "E464", {"start": v(49.09, -66.49) * mm, "end": v(49.57, -65.97) * mm});
            skLineSegment(sketch, "E465", {"start": v(49.57, -65.97) * mm, "end": v(50.47, -64.74) * mm});
            skLineSegment(sketch, "E466", {"start": v(50.47, -64.74) * mm, "end": v(50.65, -64.32) * mm});
            skLineSegment(sketch, "E467", {"start": v(50.65, -64.32) * mm, "end": v(50.78, -63.69) * mm});
            skLineSegment(sketch, "E468", {"start": v(50.78, -63.69) * mm, "end": v(51.41, -63.86) * mm});
            skLineSegment(sketch, "E469", {"start": v(51.41, -63.86) * mm, "end": v(51.7, -63.7) * mm});
            skLineSegment(sketch, "E470", {"start": v(51.7, -63.7) * mm, "end": v(52.38, -63) * mm});
            skLineSegment(sketch, "E471", {"start": v(52.38, -63) * mm, "end": v(52.87, -62.5) * mm});
            skLineSegment(sketch, "E472", {"start": v(52.87, -62.5) * mm, "end": v(51.53, -61.54) * mm});
            skLineSegment(sketch, "E473", {"start": v(51.53, -61.54) * mm, "end": v(50.28, -60.64) * mm});
            skLineSegment(sketch, "E474", {"start": v(50.28, -60.64) * mm, "end": v(49.58, -61.52) * mm});
            skLineSegment(sketch, "E475", {"start": v(49.58, -61.52) * mm, "end": v(48.87, -62.43) * mm});
            skLineSegment(sketch, "E476", {"start": v(48.87, -62.43) * mm, "end": v(49.2, -63) * mm});
            skLineSegment(sketch, "E477", {"start": v(28.1, -65.24) * mm, "end": v(29.02, -66.19) * mm});
            skLineSegment(sketch, "E478", {"start": v(29.02, -66.19) * mm, "end": v(30.23, -67.13) * mm});
            skLineSegment(sketch, "E479", {"start": v(30.23, -67.13) * mm, "end": v(30.48, -67.37) * mm});
            skLineSegment(sketch, "E480", {"start": v(30.48, -67.37) * mm, "end": v(30.85, -67.92) * mm});
            skLineSegment(sketch, "E481", {"start": v(30.85, -67.92) * mm, "end": v(31.2, -68.17) * mm});
            skLineSegment(sketch, "E482", {"start": v(31.2, -68.17) * mm, "end": v(32.42, -68.55) * mm});
            skLineSegment(sketch, "E483", {"start": v(32.42, -68.55) * mm, "end": v(32.58, -68.63) * mm});
            skLineSegment(sketch, "E484", {"start": v(32.58, -68.63) * mm, "end": v(33.4, -69.46) * mm});
            skLineSegment(sketch, "E485", {"start": v(33.4, -69.46) * mm, "end": v(33.89, -69.9) * mm});
            skLineSegment(sketch, "E486", {"start": v(33.89, -69.9) * mm, "end": v(34.22, -69.99) * mm});
            skLineSegment(sketch, "E487", {"start": v(34.22, -69.99) * mm, "end": v(36.13, -69.93) * mm});
            skLineSegment(sketch, "E488", {"start": v(36.13, -69.93) * mm, "end": v(36.45, -69.96) * mm});
            skLineSegment(sketch, "E489", {"start": v(36.45, -69.96) * mm, "end": v(37.36, -70.21) * mm});
            skLineSegment(sketch, "E490", {"start": v(37.36, -70.21) * mm, "end": v(37.82, -70.18) * mm});
            skLineSegment(sketch, "E491", {"start": v(37.82, -70.18) * mm, "end": v(39.08, -69.92) * mm});
            skLineSegment(sketch, "E492", {"start": v(39.08, -69.92) * mm, "end": v(40.07, -69.74) * mm});
            skLineSegment(sketch, "E493", {"start": v(40.07, -69.74) * mm, "end": v(40.22, -69.64) * mm});
            skLineSegment(sketch, "E494", {"start": v(40.22, -69.64) * mm, "end": v(39.99, -69.48) * mm});
            skLineSegment(sketch, "E495", {"start": v(39.99, -69.48) * mm, "end": v(38.35, -68.5) * mm});
            skLineSegment(sketch, "E496", {"start": v(38.35, -68.5) * mm, "end": v(37.69, -68.25) * mm});
            skLineSegment(sketch, "E497", {"start": v(37.69, -68.25) * mm, "end": v(33.43, -67.44) * mm});
            skLineSegment(sketch, "E498", {"start": v(33.43, -67.44) * mm, "end": v(33.1, -67.33) * mm});
            skLineSegment(sketch, "E499", {"start": v(33.1, -67.33) * mm, "end": v(30.7, -66.22) * mm});
            skLineSegment(sketch, "E500", {"start": v(30.7, -66.22) * mm, "end": v(30.43, -66.06) * mm});
            skLineSegment(sketch, "E501", {"start": v(30.43, -66.06) * mm, "end": v(28.8, -64.88) * mm});
            skLineSegment(sketch, "E502", {"start": v(28.8, -64.88) * mm, "end": v(28.48, -64.66) * mm});
            skLineSegment(sketch, "E503", {"start": v(28.48, -64.66) * mm, "end": v(28.1, -65.24) * mm});
            skLineSegment(sketch, "E504", {"start": v(56.02, -53.95) * mm, "end": v(55.72, -53.32) * mm});
            skLineSegment(sketch, "E505", {"start": v(55.72, -53.32) * mm, "end": v(55.72, -52.92) * mm});
            skLineSegment(sketch, "E506", {"start": v(55.72, -52.92) * mm, "end": v(56.16, -51.67) * mm});
            skLineSegment(sketch, "E507", {"start": v(56.16, -51.67) * mm, "end": v(56.12, -51.37) * mm});
            skLineSegment(sketch, "E508", {"start": v(56.12, -51.37) * mm, "end": v(55.86, -50.53) * mm});
            skLineSegment(sketch, "E509", {"start": v(55.86, -50.53) * mm, "end": v(55.43, -49.6) * mm});
            skLineSegment(sketch, "E510", {"start": v(55.43, -49.6) * mm, "end": v(55.18, -49.25) * mm});
            skLineSegment(sketch, "E511", {"start": v(55.18, -49.25) * mm, "end": v(54.55, -48) * mm});
            skLineSegment(sketch, "E512", {"start": v(54.55, -48) * mm, "end": v(54.07, -47.39) * mm});
            skLineSegment(sketch, "E513", {"start": v(54.07, -47.39) * mm, "end": v(53.28, -46.46) * mm});
            skLineSegment(sketch, "E514", {"start": v(53.28, -46.46) * mm, "end": v(53.01, -46.09) * mm});
            skLineSegment(sketch, "E515", {"start": v(53.01, -46.09) * mm, "end": v(52.85, -45.93) * mm});
            skLineSegment(sketch, "E516", {"start": v(52.85, -45.93) * mm, "end": v(51.88, -45.46) * mm});
            skLineSegment(sketch, "E517", {"start": v(51.88, -45.46) * mm, "end": v(52, -45.85) * mm});
            skLineSegment(sketch, "E518", {"start": v(52, -45.85) * mm, "end": v(52.62, -47.66) * mm});
            skLineSegment(sketch, "E519", {"start": v(52.62, -47.66) * mm, "end": v(53.53, -50.78) * mm});
            skLineSegment(sketch, "E520", {"start": v(53.53, -50.78) * mm, "end": v(54.17, -54.52) * mm});
            skLineSegment(sketch, "E521", {"start": v(54.17, -54.52) * mm, "end": v(54.27, -54.89) * mm});
            skLineSegment(sketch, "E522", {"start": v(54.27, -54.89) * mm, "end": v(54.9, -56.58) * mm});
            skLineSegment(sketch, "E523", {"start": v(54.9, -56.58) * mm, "end": v(55, -56.8) * mm});
            skLineSegment(sketch, "E524", {"start": v(55, -56.8) * mm, "end": v(56.02, -53.95) * mm});
            skLineSegment(sketch, "E525", {"start": v(56.77, -64.5) * mm, "end": v(56.77, -64.86) * mm});
            skLineSegment(sketch, "E526", {"start": v(56.77, -64.86) * mm, "end": v(56.81, -66.13) * mm});
            skLineSegment(sketch, "E527", {"start": v(56.81, -66.13) * mm, "end": v(56.73, -66.91) * mm});
            skLineSegment(sketch, "E528", {"start": v(56.73, -66.91) * mm, "end": v(56.44, -68.1) * mm});
            skLineSegment(sketch, "E529", {"start": v(56.44, -68.1) * mm, "end": v(56.37, -68.45) * mm});
            skLineSegment(sketch, "E530", {"start": v(56.37, -68.45) * mm, "end": v(56.46, -68.47) * mm});
            skLineSegment(sketch, "E531", {"start": v(56.46, -68.47) * mm, "end": v(58.88, -68.63) * mm});
            skLineSegment(sketch, "E532", {"start": v(58.88, -68.63) * mm, "end": v(59.18, -68.53) * mm});
            skLineSegment(sketch, "E533", {"start": v(59.18, -68.53) * mm, "end": v(61.07, -66.98) * mm});
            skLineSegment(sketch, "E534", {"start": v(61.07, -66.98) * mm, "end": v(61.22, -66.84) * mm});
            skLineSegment(sketch, "E535", {"start": v(61.22, -66.84) * mm, "end": v(61.16, -66.78) * mm});
            skLineSegment(sketch, "E536", {"start": v(61.16, -66.78) * mm, "end": v(56.77, -64.5) * mm});
            skLineSegment(sketch, "E537", {"start": v(44.45, -56.2) * mm, "end": v(45.16, -57.17) * mm});
            skLineSegment(sketch, "E538", {"start": v(45.16, -57.17) * mm, "end": v(46.1, -58.02) * mm});
            skLineSegment(sketch, "E539", {"start": v(46.1, -58.02) * mm, "end": v(46.82, -58.43) * mm});
            skLineSegment(sketch, "E540", {"start": v(46.82, -58.43) * mm, "end": v(46.25, -57.34) * mm});
            skLineSegment(sketch, "E541", {"start": v(46.25, -57.34) * mm, "end": v(46.67, -57.25) * mm});
            skLineSegment(sketch, "E542", {"start": v(46.67, -57.25) * mm, "end": v(46.9, -57.16) * mm});
            skLineSegment(sketch, "E543", {"start": v(46.9, -57.16) * mm, "end": v(47.3, -56.8) * mm});
            skLineSegment(sketch, "E544", {"start": v(47.3, -56.8) * mm, "end": v(47.41, -56.52) * mm});
            skLineSegment(sketch, "E545", {"start": v(47.41, -56.52) * mm, "end": v(47.36, -55.88) * mm});
            skLineSegment(sketch, "E546", {"start": v(47.36, -55.88) * mm, "end": v(47.14, -55.48) * mm});
            skLineSegment(sketch, "E547", {"start": v(47.14, -55.48) * mm, "end": v(46.6, -55.04) * mm});
            skLineSegment(sketch, "E548", {"start": v(46.6, -55.04) * mm, "end": v(47.55, -54.1) * mm});
            skLineSegment(sketch, "E549", {"start": v(47.55, -54.1) * mm, "end": v(47.85, -53.55) * mm});
            skLineSegment(sketch, "E550", {"start": v(47.85, -53.55) * mm, "end": v(47.85, -53.43) * mm});
            skLineSegment(sketch, "E551", {"start": v(47.85, -53.43) * mm, "end": v(47.54, -53) * mm});
            skLineSegment(sketch, "E552", {"start": v(47.54, -53) * mm, "end": v(46.47, -53.77) * mm});
            skLineSegment(sketch, "E553", {"start": v(46.47, -53.77) * mm, "end": v(45.3, -54.8) * mm});
            skLineSegment(sketch, "E554", {"start": v(45.3, -54.8) * mm, "end": v(44.45, -56.2) * mm});
            skLineSegment(sketch, "E555", {"start": v(40.06, -59.38) * mm, "end": v(39.78, -59.56) * mm});
            skLineSegment(sketch, "E556", {"start": v(39.78, -59.56) * mm, "end": v(38.58, -60.47) * mm});
            skLineSegment(sketch, "E557", {"start": v(38.58, -60.47) * mm, "end": v(38.14, -60.91) * mm});
            skLineSegment(sketch, "E558", {"start": v(38.14, -60.91) * mm, "end": v(37.32, -61.78) * mm});
            skLineSegment(sketch, "E559", {"start": v(37.32, -61.78) * mm, "end": v(37.01, -62.7) * mm});
            skLineSegment(sketch, "E560", {"start": v(37.01, -62.7) * mm, "end": v(37.7, -63.64) * mm});
            skLineSegment(sketch, "E561", {"start": v(37.7, -63.64) * mm, "end": v(38.7, -64.49) * mm});
            skLineSegment(sketch, "E562", {"start": v(38.7, -64.49) * mm, "end": v(39.31, -64.85) * mm});
            skLineSegment(sketch, "E563", {"start": v(39.31, -64.85) * mm, "end": v(38.75, -63.75) * mm});
            skLineSegment(sketch, "E564", {"start": v(38.75, -63.75) * mm, "end": v(39.45, -63.57) * mm});
            skLineSegment(sketch, "E565", {"start": v(39.45, -63.57) * mm, "end": v(39.8, -63.18) * mm});
            skLineSegment(sketch, "E566", {"start": v(39.8, -63.18) * mm, "end": v(39.9, -62.65) * mm});
            skLineSegment(sketch, "E567", {"start": v(39.9, -62.65) * mm, "end": v(39.77, -62.22) * mm});
            skLineSegment(sketch, "E568", {"start": v(39.77, -62.22) * mm, "end": v(39.13, -61.4) * mm});
            skLineSegment(sketch, "E569", {"start": v(39.13, -61.4) * mm, "end": v(39.33, -61.2) * mm});
            skLineSegment(sketch, "E570", {"start": v(39.33, -61.2) * mm, "end": v(40.11, -60.44) * mm});
            skLineSegment(sketch, "E571", {"start": v(40.11, -60.44) * mm, "end": v(40.24, -59.85) * mm});
            skLineSegment(sketch, "E572", {"start": v(40.24, -59.85) * mm, "end": v(40.06, -59.38) * mm});
            skLineSegment(sketch, "E573", {"start": v(48.01, -61.22) * mm, "end": v(47.48, -60.7) * mm});
            skLineSegment(sketch, "E574", {"start": v(47.48, -60.7) * mm, "end": v(47, -60.46) * mm});
            skLineSegment(sketch, "E575", {"start": v(47, -60.46) * mm, "end": v(46.4, -60.33) * mm});
            skLineSegment(sketch, "E576", {"start": v(46.4, -60.33) * mm, "end": v(45.88, -60.47) * mm});
            skLineSegment(sketch, "E577", {"start": v(45.88, -60.47) * mm, "end": v(45.28, -61.05) * mm});
            skLineSegment(sketch, "E578", {"start": v(45.28, -61.05) * mm, "end": v(44.72, -61.68) * mm});
            skLineSegment(sketch, "E579", {"start": v(44.72, -61.68) * mm, "end": v(44.4, -62.51) * mm});
            skLineSegment(sketch, "E580", {"start": v(44.4, -62.51) * mm, "end": v(44.58, -63.38) * mm});
            skLineSegment(sketch, "E581", {"start": v(44.58, -63.38) * mm, "end": v(44.68, -63.48) * mm});
            skLineSegment(sketch, "E582", {"start": v(44.68, -63.48) * mm, "end": v(45.24, -63.67) * mm});
            skLineSegment(sketch, "E583", {"start": v(45.24, -63.67) * mm, "end": v(45.89, -63.36) * mm});
            skLineSegment(sketch, "E584", {"start": v(45.89, -63.36) * mm, "end": v(46.43, -63.06) * mm});
            skLineSegment(sketch, "E585", {"start": v(46.43, -63.06) * mm, "end": v(47.15, -62.66) * mm});
            skLineSegment(sketch, "E586", {"start": v(47.15, -62.66) * mm, "end": v(48.01, -61.22) * mm});
            skLineSegment(sketch, "E587", {"start": v(56.87, -70.72) * mm, "end": v(56.58, -70.63) * mm});
            skLineSegment(sketch, "E588", {"start": v(56.58, -70.63) * mm, "end": v(54.8, -70.18) * mm});
            skLineSegment(sketch, "E589", {"start": v(54.8, -70.18) * mm, "end": v(54.5, -70.14) * mm});
            skLineSegment(sketch, "E590", {"start": v(54.5, -70.14) * mm, "end": v(53.84, -70.2) * mm});
            skLineSegment(sketch, "E591", {"start": v(53.84, -70.2) * mm, "end": v(53.3, -70.49) * mm});
            skLineSegment(sketch, "E592", {"start": v(53.3, -70.49) * mm, "end": v(53.25, -70.58) * mm});
            skLineSegment(sketch, "E593", {"start": v(53.25, -70.58) * mm, "end": v(53.25, -71.25) * mm});
            skLineSegment(sketch, "E594", {"start": v(53.25, -71.25) * mm, "end": v(53.77, -73.4) * mm});
            skLineSegment(sketch, "E595", {"start": v(53.77, -73.4) * mm, "end": v(53.8, -73.44) * mm});
            skLineSegment(sketch, "E596", {"start": v(53.8, -73.44) * mm, "end": v(54.18, -73.04) * mm});
            skLineSegment(sketch, "E597", {"start": v(54.18, -73.04) * mm, "end": v(54.95, -72.35) * mm});
            skLineSegment(sketch, "E598", {"start": v(54.95, -72.35) * mm, "end": v(56, -71.79) * mm});
            skLineSegment(sketch, "E599", {"start": v(56, -71.79) * mm, "end": v(56.15, -71.69) * mm});
            skLineSegment(sketch, "E600", {"start": v(56.15, -71.69) * mm, "end": v(56.87, -70.72) * mm});
            skLineSegment(sketch, "E601", {"start": v(49.27, -72.56) * mm, "end": v(49.37, -74.3) * mm});
            skLineSegment(sketch, "E602", {"start": v(49.37, -74.3) * mm, "end": v(49.59, -76.06) * mm});
            skLineSegment(sketch, "E603", {"start": v(49.59, -76.06) * mm, "end": v(51.22, -74.78) * mm});
            skLineSegment(sketch, "E604", {"start": v(51.22, -74.78) * mm, "end": v(51.33, -74.51) * mm});
            skLineSegment(sketch, "E605", {"start": v(51.33, -74.51) * mm, "end": v(51.5, -72.79) * mm});
            skLineSegment(sketch, "E606", {"start": v(51.5, -72.79) * mm, "end": v(51.5, -72.55) * mm});
            skLineSegment(sketch, "E607", {"start": v(51.5, -72.55) * mm, "end": v(49.27, -72.56) * mm});
            skLineSegment(sketch, "E608", {"start": v(48.9, -54.27) * mm, "end": v(48.85, -54.29) * mm});
            skLineSegment(sketch, "E609", {"start": v(48.85, -54.29) * mm, "end": v(48.84, -54.56) * mm});
            skLineSegment(sketch, "E610", {"start": v(48.84, -54.56) * mm, "end": v(48.87, -55.37) * mm});
            skLineSegment(sketch, "E611", {"start": v(48.87, -55.37) * mm, "end": v(48.6, -57.19) * mm});
            skLineSegment(sketch, "E612", {"start": v(48.6, -57.19) * mm, "end": v(48.06, -58.15) * mm});
            skLineSegment(sketch, "E613", {"start": v(48.06, -58.15) * mm, "end": v(47.87, -58.82) * mm});
            skLineSegment(sketch, "E614", {"start": v(47.87, -58.82) * mm, "end": v(48.52, -58.87) * mm});
            skLineSegment(sketch, "E615", {"start": v(48.52, -58.87) * mm, "end": v(48.7, -58.81) * mm});
            skLineSegment(sketch, "E616", {"start": v(48.7, -58.81) * mm, "end": v(49.56, -58.25) * mm});
            skLineSegment(sketch, "E617", {"start": v(49.56, -58.25) * mm, "end": v(49.69, -58.07) * mm});
            skLineSegment(sketch, "E618", {"start": v(49.69, -58.07) * mm, "end": v(49.93, -56.85) * mm});
            skLineSegment(sketch, "E619", {"start": v(49.93, -56.85) * mm, "end": v(49.9, -56.3) * mm});
            skLineSegment(sketch, "E620", {"start": v(49.9, -56.3) * mm, "end": v(49.7, -55.6) * mm});
            skLineSegment(sketch, "E621", {"start": v(49.7, -55.6) * mm, "end": v(48.9, -54.27) * mm});
            skLineSegment(sketch, "E622", {"start": v(41.77, -60.6) * mm, "end": v(41.69, -60.6) * mm});
            skLineSegment(sketch, "E623", {"start": v(41.69, -60.6) * mm, "end": v(41.71, -60.77) * mm});
            skLineSegment(sketch, "E624", {"start": v(41.71, -60.77) * mm, "end": v(41.56, -62.88) * mm});
            skLineSegment(sketch, "E625", {"start": v(41.56, -62.88) * mm, "end": v(41.45, -63.34) * mm});
            skLineSegment(sketch, "E626", {"start": v(41.45, -63.34) * mm, "end": v(41.15, -63.9) * mm});
            skLineSegment(sketch, "E627", {"start": v(41.15, -63.9) * mm, "end": v(40.91, -64.07) * mm});
            skLineSegment(sketch, "E628", {"start": v(40.91, -64.07) * mm, "end": v(40.52, -64.16) * mm});
            skLineSegment(sketch, "E629", {"start": v(40.52, -64.16) * mm, "end": v(40.36, -64.95) * mm});
            skLineSegment(sketch, "E630", {"start": v(40.36, -64.95) * mm, "end": v(41.45, -64.95) * mm});
            skLineSegment(sketch, "E631", {"start": v(41.45, -64.95) * mm, "end": v(41.54, -64.92) * mm});
            skLineSegment(sketch, "E632", {"start": v(41.54, -64.92) * mm, "end": v(42.47, -64.02) * mm});
            skLineSegment(sketch, "E633", {"start": v(42.47, -64.02) * mm, "end": v(42.7, -63.17) * mm});
            skLineSegment(sketch, "E634", {"start": v(42.7, -63.17) * mm, "end": v(42.48, -62.2) * mm});
            skLineSegment(sketch, "E635", {"start": v(42.48, -62.2) * mm, "end": v(42.38, -61.96) * mm});
            skLineSegment(sketch, "E636", {"start": v(42.38, -61.96) * mm, "end": v(41.77, -60.6) * mm});
            skLineSegment(sketch, "E637", {"start": v(68.4, -60.3) * mm, "end": v(67.37, -59.5) * mm});
            skLineSegment(sketch, "E638", {"start": v(67.37, -59.5) * mm, "end": v(67.23, -59.45) * mm});
            skLineSegment(sketch, "E639", {"start": v(67.23, -59.45) * mm, "end": v(66.6, -59.38) * mm});
            skLineSegment(sketch, "E640", {"start": v(66.6, -59.38) * mm, "end": v(66.27, -60.21) * mm});
            skLineSegment(sketch, "E641", {"start": v(66.27, -60.21) * mm, "end": v(66.32, -60.72) * mm});
            skLineSegment(sketch, "E642", {"start": v(66.32, -60.72) * mm, "end": v(66.88, -61.5) * mm});
            skLineSegment(sketch, "E643", {"start": v(66.88, -61.5) * mm, "end": v(67.01, -61.64) * mm});
            skLineSegment(sketch, "E644", {"start": v(67.01, -61.64) * mm, "end": v(68.4, -60.3) * mm});
            skLineSegment(sketch, "E645", {"start": v(69.96, -58.8) * mm, "end": v(69.87, -58.72) * mm});
            skLineSegment(sketch, "E646", {"start": v(69.87, -58.72) * mm, "end": v(68.86, -58.04) * mm});
            skLineSegment(sketch, "E647", {"start": v(68.86, -58.04) * mm, "end": v(68.3, -57.95) * mm});
            skLineSegment(sketch, "E648", {"start": v(68.3, -57.95) * mm, "end": v(68.08, -58.3) * mm});
            skLineSegment(sketch, "E649", {"start": v(68.08, -58.3) * mm, "end": v(68.06, -58.37) * mm});
            skLineSegment(sketch, "E650", {"start": v(68.06, -58.37) * mm, "end": v(68.08, -58.7) * mm});
            skLineSegment(sketch, "E651", {"start": v(68.08, -58.7) * mm, "end": v(68.35, -59.14) * mm});
            skLineSegment(sketch, "E652", {"start": v(68.35, -59.14) * mm, "end": v(68.9, -59.84) * mm});
            skLineSegment(sketch, "E653", {"start": v(68.9, -59.84) * mm, "end": v(69.96, -58.8) * mm});
            skLineSegment(sketch, "E654", {"start": v(51.2, -69.74) * mm, "end": v(48.9, -71.04) * mm});
            skLineSegment(sketch, "E655", {"start": v(48.9, -71.04) * mm, "end": v(50.12, -71.2) * mm});
            skLineSegment(sketch, "E656", {"start": v(50.12, -71.2) * mm, "end": v(51.37, -71.07) * mm});
            skLineSegment(sketch, "E657", {"start": v(51.37, -71.07) * mm, "end": v(51.2, -69.74) * mm});
            skLineSegment(sketch, "E658", {"start": v(42.65, -80.3) * mm, "end": v(42, -79.46) * mm});
            skLineSegment(sketch, "E659", {"start": v(42, -79.46) * mm, "end": v(41.33, -78.97) * mm});
            skLineSegment(sketch, "E660", {"start": v(41.33, -78.97) * mm, "end": v(41.24, -80.03) * mm});
            skLineSegment(sketch, "E661", {"start": v(41.24, -80.03) * mm, "end": v(41.49, -81.05) * mm});
            skLineSegment(sketch, "E662", {"start": v(41.49, -81.05) * mm, "end": v(42.65, -80.3) * mm});
            skLineSegment(sketch, "E663", {"start": v(43.28, -79.82) * mm, "end": v(44.89, -79.08) * mm});
            skLineSegment(sketch, "E664", {"start": v(44.89, -79.08) * mm, "end": v(43.84, -78.43) * mm});
            skLineSegment(sketch, "E665", {"start": v(43.84, -78.43) * mm, "end": v(43.6, -78.46) * mm});
            skLineSegment(sketch, "E666", {"start": v(43.6, -78.46) * mm, "end": v(43.04, -78.9) * mm});
            skLineSegment(sketch, "E667", {"start": v(43.04, -78.9) * mm, "end": v(43.28, -79.82) * mm});
            skLineSegment(sketch, "E668", {"start": v(54.4, -67.86) * mm, "end": v(54.45, -67.8) * mm});
            skLineSegment(sketch, "E669", {"start": v(54.45, -67.8) * mm, "end": v(55.01, -66.09) * mm});
            skLineSegment(sketch, "E670", {"start": v(55.01, -66.09) * mm, "end": v(55.16, -65.3) * mm});
            skLineSegment(sketch, "E671", {"start": v(55.16, -65.3) * mm, "end": v(53.77, -66.74) * mm});
            skLineSegment(sketch, "E672", {"start": v(53.77, -66.74) * mm, "end": v(54.4, -67.86) * mm});
            skLineSegment(sketch, "E673", {"start": v(39.81, -81.03) * mm, "end": v(39.98, -81.66) * mm});
            skLineSegment(sketch, "E674", {"start": v(39.98, -81.66) * mm, "end": v(40.7, -81.37) * mm});
            skLineSegment(sketch, "E675", {"start": v(40.7, -81.37) * mm, "end": v(40.28, -80.94) * mm});
            skLineSegment(sketch, "E676", {"start": v(40.28, -80.94) * mm, "end": v(39.81, -81.03) * mm});
            skLineSegment(sketch, "E677.0", {"start": v(0, 0) * mm, "end": v(-6.35, 102.95) * mm});
            skLineSegment(sketch, "E677.1", {"start": v(0, 0) * mm, "end": v(6.35, 102.95) * mm});
            skArc(sketch, "E677.2", {"start": v(-6.1, 99) * mm, "mid": v(-3.93, 99.81) * mm, "end": v(-2.58, 101.71) * mm});
            skArc(sketch, "E677.3", {"start": v(-1.4, 104.85) * mm, "mid": v(-2, 103.3) * mm, "end": v(-2.55, 101.74) * mm});
            skLineSegment(sketch, "E677.4", {"start": v(-6.35, 102.95) * mm, "end": v(-2.58, 101.71) * mm});
            skCircle(sketch, "E677.5", {"center": v(0, 0) * mm, "radius": 103.19 * mm});
            skArc(sketch, "E677.6", {"start": v(1.4, 104.85) * mm, "mid": v(0, 104.86) * mm, "end": v(-1.4, 104.85) * mm});
            skLineSegment(sketch, "E677.7", {"start": v(0, 0) * mm, "end": v(0, 116.9) * mm});
            skArc(sketch, "E677.8", {"start": v(-6.1, 99) * mm, "mid": v(-3.9, 99.82) * mm, "end": v(-2.55, 101.74) * mm});
            skArc(sketch, "E677.9", {"start": v(2.58, 101.71) * mm, "mid": v(3.93, 99.81) * mm, "end": v(6.1, 99) * mm});
            skArc(sketch, "E677.10", {"start": v(2.55, 101.74) * mm, "mid": v(3.9, 99.82) * mm, "end": v(6.1, 99) * mm});
            skArc(sketch, "E677.11", {"start": v(2.56, 101.7) * mm, "mid": v(2, 103.29) * mm, "end": v(1.4, 104.85) * mm});
            skLineSegment(sketch, "E677.12", {"start": v(6.35, 102.95) * mm, "end": v(2.56, 101.7) * mm});
            skArc(sketch, "E677.13", {"start": v(-18.22, 97.5) * mm, "mid": v(-16.14, 98.58) * mm, "end": v(-15.03, 100.65) * mm});
            skArc(sketch, "E677.14", {"start": v(-14.27, 103.88) * mm, "mid": v(-14.68, 102.27) * mm, "end": v(-15.03, 100.65) * mm});
            skArc(sketch, "E677.15", {"start": v(-11.5, 104.22) * mm, "mid": v(-12.89, 104.06) * mm, "end": v(-14.27, 103.88) * mm});
            skArc(sketch, "E677.16", {"start": v(-9.96, 101.25) * mm, "mid": v(-10.7, 102.75) * mm, "end": v(-11.5, 104.22) * mm});
            skArc(sketch, "E677.17", {"start": v(-9.98, 101.28) * mm, "mid": v(-8.4, 99.54) * mm, "end": v(-6.1, 99) * mm});
            skArc(sketch, "E677.18", {"start": v(-30.07, 94.51) * mm, "mid": v(-28.13, 95.85) * mm, "end": v(-27.28, 98.04) * mm});
            skArc(sketch, "E677.19", {"start": v(-26.93, 101.34) * mm, "mid": v(-27.14, 99.7) * mm, "end": v(-27.28, 98.04) * mm});
            skArc(sketch, "E677.20", {"start": v(-24.22, 102.02) * mm, "mid": v(-25.58, 101.69) * mm, "end": v(-26.93, 101.34) * mm});
            skArc(sketch, "E677.21", {"start": v(-22.33, 99.26) * mm, "mid": v(-23.25, 100.66) * mm, "end": v(-24.22, 102.02) * mm});
            skArc(sketch, "E677.22", {"start": v(-22.35, 99.29) * mm, "mid": v(-20.56, 97.76) * mm, "end": v(-18.22, 97.5) * mm});
            skArc(sketch, "E677.23", {"start": v(-41.45, 90.1) * mm, "mid": v(-39.7, 91.67) * mm, "end": v(-39.13, 93.95) * mm});
            skArc(sketch, "E677.24", {"start": v(-39.18, 97.26) * mm, "mid": v(-39.18, 95.6) * mm, "end": v(-39.13, 93.95) * mm});
            skArc(sketch, "E677.25", {"start": v(-36.57, 98.27) * mm, "mid": v(-37.88, 97.78) * mm, "end": v(-39.18, 97.26) * mm});
            skArc(sketch, "E677.26", {"start": v(-34.36, 95.76) * mm, "mid": v(-35.44, 97.04) * mm, "end": v(-36.57, 98.27) * mm});
            skArc(sketch, "E677.27", {"start": v(-34.38, 95.79) * mm, "mid": v(-32.42, 94.49) * mm, "end": v(-30.07, 94.51) * mm});
            skArc(sketch, "E677.28", {"start": v(-52.21, 84.33) * mm, "mid": v(-50.66, 86.1) * mm, "end": v(-50.37, 88.43) * mm});
            skArc(sketch, "E677.29", {"start": v(-50.83, 91.71) * mm, "mid": v(-50.63, 90.06) * mm, "end": v(-50.37, 88.43) * mm});
            skArc(sketch, "E677.30", {"start": v(-48.37, 93.03) * mm, "mid": v(-49.6, 92.38) * mm, "end": v(-50.83, 91.71) * mm});
            skArc(sketch, "E677.31", {"start": v(-45.86, 90.81) * mm, "mid": v(-47.1, 91.94) * mm, "end": v(-48.37, 93.03) * mm});
            skArc(sketch, "E677.32", {"start": v(-45.89, 90.84) * mm, "mid": v(-43.78, 89.79) * mm, "end": v(-41.45, 90.1) * mm});
            skArc(sketch, "E677.33", {"start": v(-62.18, 77.27) * mm, "mid": v(-60.86, 79.22) * mm, "end": v(-60.86, 81.57) * mm});
            skArc(sketch, "E677.34", {"start": v(-61.72, 84.77) * mm, "mid": v(-61.32, 83.16) * mm, "end": v(-60.86, 81.57) * mm});
            skArc(sketch, "E677.35", {"start": v(-59.44, 86.38) * mm, "mid": v(-60.58, 85.58) * mm, "end": v(-61.72, 84.77) * mm});
            skArc(sketch, "E677.36", {"start": v(-56.68, 84.49) * mm, "mid": v(-58.04, 85.46) * mm, "end": v(-59.44, 86.38) * mm});
            skArc(sketch, "E677.37", {"start": v(-56.7, 84.5) * mm, "mid": v(-54.49, 83.73) * mm, "end": v(-52.21, 84.33) * mm});
            skArc(sketch, "E677.38", {"start": v(-71.2, 69.04) * mm, "mid": v(-70.13, 71.14) * mm, "end": v(-70.42, 73.47) * mm});
            skArc(sketch, "E677.39", {"start": v(-71.67, 76.54) * mm, "mid": v(-71.07, 75) * mm, "end": v(-70.42, 73.47) * mm});
            skArc(sketch, "E677.40", {"start": v(-69.6, 78.42) * mm, "mid": v(-70.64, 77.49) * mm, "end": v(-71.67, 76.54) * mm});
            skArc(sketch, "E677.41", {"start": v(-66.63, 76.88) * mm, "mid": v(-68.1, 77.68) * mm, "end": v(-69.6, 78.42) * mm});
            skArc(sketch, "E677.42", {"start": v(-66.66, 76.9) * mm, "mid": v(-64.36, 76.4) * mm, "end": v(-62.18, 77.27) * mm});
            skArc(sketch, "E677.43", {"start": v(-79.15, 59.77) * mm, "mid": v(-78.34, 61.98) * mm, "end": v(-78.92, 64.26) * mm});
            skArc(sketch, "E677.44", {"start": v(-80.53, 67.15) * mm, "mid": v(-79.75, 65.7) * mm, "end": v(-78.92, 64.26) * mm});
            skArc(sketch, "E677.45", {"start": v(-78.71, 69.28) * mm, "mid": v(-79.63, 68.22) * mm, "end": v(-80.53, 67.15) * mm});
            skArc(sketch, "E677.46", {"start": v(-75.57, 68.11) * mm, "mid": v(-77.13, 68.72) * mm, "end": v(-78.71, 69.28) * mm});
            skArc(sketch, "E677.47", {"start": v(-75.6, 68.13) * mm, "mid": v(-73.26, 67.9) * mm, "end": v(-71.2, 69.04) * mm});
            skArc(sketch, "E677.48", {"start": v(-85.9, 49.6) * mm, "mid": v(-85.37, 51.88) * mm, "end": v(-86.21, 54.07) * mm});
            skArc(sketch, "E677.49", {"start": v(-88.17, 56.75) * mm, "mid": v(-87.22, 55.4) * mm, "end": v(-86.21, 54.07) * mm});
            skArc(sketch, "E677.50", {"start": v(-86.63, 59.08) * mm, "mid": v(-87.4, 57.92) * mm, "end": v(-88.17, 56.75) * mm});
            skArc(sketch, "E677.51", {"start": v(-83.37, 58.3) * mm, "mid": v(-85, 58.72) * mm, "end": v(-86.63, 59.08) * mm});
            skArc(sketch, "E677.52", {"start": v(-83.4, 58.32) * mm, "mid": v(-81.05, 58.4) * mm, "end": v(-79.15, 59.77) * mm});
            skArc(sketch, "E677.53", {"start": v(-91.34, 38.66) * mm, "mid": v(-91.1, 41) * mm, "end": v(-92.2, 43.07) * mm});
            skArc(sketch, "E677.54", {"start": v(-94.48, 45.48) * mm, "mid": v(-93.36, 44.26) * mm, "end": v(-92.2, 43.07) * mm});
            skArc(sketch, "E677.55", {"start": v(-93.23, 47.99) * mm, "mid": v(-93.86, 46.74) * mm, "end": v(-94.48, 45.48) * mm});
            skArc(sketch, "E677.56", {"start": v(-89.9, 47.62) * mm, "mid": v(-91.56, 47.83) * mm, "end": v(-93.23, 47.99) * mm});
            skArc(sketch, "E677.57", {"start": v(-89.94, 47.63) * mm, "mid": v(-87.61, 47.99) * mm, "end": v(-85.9, 49.6) * mm});
            skArc(sketch, "E677.58", {"start": v(-95.4, 27.14) * mm, "mid": v(-95.44, 29.5) * mm, "end": v(-96.8, 31.41) * mm});
            skArc(sketch, "E677.59", {"start": v(-99.35, 33.53) * mm, "mid": v(-98.1, 32.45) * mm, "end": v(-96.8, 31.41) * mm});
            skArc(sketch, "E677.60", {"start": v(-98.42, 36.16) * mm, "mid": v(-98.9, 34.85) * mm, "end": v(-99.35, 33.53) * mm});
            skArc(sketch, "E677.61", {"start": v(-95.07, 36.21) * mm, "mid": v(-96.75, 36.22) * mm, "end": v(-98.42, 36.16) * mm});
            skArc(sketch, "E677.62", {"start": v(-95.1, 36.21) * mm, "mid": v(-92.85, 36.86) * mm, "end": v(-91.34, 38.66) * mm});
            skArc(sketch, "E677.63", {"start": v(-98, 15.21) * mm, "mid": v(-98.34, 17.54) * mm, "end": v(-99.93, 19.28) * mm});
            skArc(sketch, "E677.64", {"start": v(-102.72, 21.07) * mm, "mid": v(-101.34, 20.15) * mm, "end": v(-99.93, 19.28) * mm});
            skArc(sketch, "E677.65", {"start": v(-102.12, 23.8) * mm, "mid": v(-102.43, 22.43) * mm, "end": v(-102.72, 21.07) * mm});
            skArc(sketch, "E677.66", {"start": v(-98.8, 24.26) * mm, "mid": v(-100.47, 24.05) * mm, "end": v(-102.12, 23.8) * mm});
            skArc(sketch, "E677.67", {"start": v(-98.84, 24.25) * mm, "mid": v(-96.67, 25.17) * mm, "end": v(-95.4, 27.14) * mm});
            skArc(sketch, "E677.68", {"start": v(-99.13, 3.05) * mm, "mid": v(-99.75, 5.32) * mm, "end": v(-101.54, 6.85) * mm});
            skArc(sketch, "E677.69", {"start": v(-104.53, 8.28) * mm, "mid": v(-103.05, 7.54) * mm, "end": v(-101.54, 6.85) * mm});
            skArc(sketch, "E677.70", {"start": v(-104.27, 11.07) * mm, "mid": v(-104.4, 9.67) * mm, "end": v(-104.53, 8.28) * mm});
            skArc(sketch, "E677.71", {"start": v(-101.03, 11.93) * mm, "mid": v(-102.66, 11.53) * mm, "end": v(-104.27, 11.07) * mm});
            skArc(sketch, "E677.72", {"start": v(-101.07, 11.92) * mm, "mid": v(-99.03, 13.1) * mm, "end": v(-98, 15.21) * mm});
            skArc(sketch, "E677.73", {"start": v(-98.76, -9.15) * mm, "mid": v(-99.65, -6.98) * mm, "end": v(-101.61, -5.68) * mm});
            skArc(sketch, "E677.74", {"start": v(-104.75, -4.63) * mm, "mid": v(-103.2, -5.18) * mm, "end": v(-101.61, -5.68) * mm});
            skArc(sketch, "E677.75", {"start": v(-104.84, -1.83) * mm, "mid": v(-104.8, -3.23) * mm, "end": v(-104.75, -4.63) * mm});
            skArc(sketch, "E677.76", {"start": v(-101.74, -0.58) * mm, "mid": v(-103.3, -1.18) * mm, "end": v(-104.84, -1.83) * mm});
            skArc(sketch, "E677.77", {"start": v(-101.77, -0.59) * mm, "mid": v(-99.9, 0.83) * mm, "end": v(-99.13, 3.05) * mm});
            skArc(sketch, "E677.78", {"start": v(-96.88, -21.22) * mm, "mid": v(-98.04, -19.17) * mm, "end": v(-100.14, -18.12) * mm});
            skArc(sketch, "E677.79", {"start": v(-103.4, -17.46) * mm, "mid": v(-101.77, -17.82) * mm, "end": v(-100.14, -18.12) * mm});
            skArc(sketch, "E677.80", {"start": v(-103.82, -14.7) * mm, "mid": v(-103.62, -16.08) * mm, "end": v(-103.4, -17.46) * mm});
            skArc(sketch, "E677.81", {"start": v(-100.9, -13.07) * mm, "mid": v(-102.37, -13.86) * mm, "end": v(-103.82, -14.7) * mm});
            skArc(sketch, "E677.82", {"start": v(-100.92, -13.09) * mm, "mid": v(-99.24, -11.45) * mm, "end": v(-98.76, -9.15) * mm});
            skArc(sketch, "E677.83", {"start": v(-93.54, -32.96) * mm, "mid": v(-94.94, -31.07) * mm, "end": v(-97.16, -30.3) * mm});
            skArc(sketch, "E677.84", {"start": v(-100.46, -30.04) * mm, "mid": v(-98.81, -30.2) * mm, "end": v(-97.16, -30.3) * mm});
            skArc(sketch, "E677.85", {"start": v(-101.23, -27.35) * mm, "mid": v(-100.85, -28.7) * mm, "end": v(-100.46, -30.04) * mm});
            skArc(sketch, "E677.86", {"start": v(-98.52, -25.37) * mm, "mid": v(-99.9, -26.34) * mm, "end": v(-101.23, -27.35) * mm});
            skArc(sketch, "E677.87", {"start": v(-98.55, -25.4) * mm, "mid": v(-97.08, -23.56) * mm, "end": v(-96.88, -21.22) * mm});
            skArc(sketch, "E677.88", {"start": v(-88.78, -44.2) * mm, "mid": v(-90.4, -42.5) * mm, "end": v(-92.7, -42) * mm});
            skArc(sketch, "E677.89", {"start": v(-96, -42.15) * mm, "mid": v(-94.35, -42.1) * mm, "end": v(-92.7, -42) * mm});
            skArc(sketch, "E677.90", {"start": v(-97.1, -39.58) * mm, "mid": v(-96.56, -40.87) * mm, "end": v(-96, -42.15) * mm});
            skArc(sketch, "E677.91", {"start": v(-94.66, -37.29) * mm, "mid": v(-95.9, -38.41) * mm, "end": v(-97.1, -39.58) * mm});
            skArc(sketch, "E677.92", {"start": v(-94.68, -37.31) * mm, "mid": v(-93.45, -35.31) * mm, "end": v(-93.54, -32.96) * mm});
            skArc(sketch, "E677.93", {"start": v(-82.68, -54.78) * mm, "mid": v(-84.5, -53.3) * mm, "end": v(-86.83, -53.07) * mm});
            skArc(sketch, "E677.94", {"start": v(-90.1, -53.63) * mm, "mid": v(-88.46, -53.38) * mm, "end": v(-86.83, -53.07) * mm});
            skArc(sketch, "E677.95", {"start": v(-91.5, -51.21) * mm, "mid": v(-90.8, -52.43) * mm, "end": v(-90.1, -53.63) * mm});
            skArc(sketch, "E677.96", {"start": v(-89.36, -48.64) * mm, "mid": v(-90.45, -49.9) * mm, "end": v(-91.5, -51.21) * mm});
            skArc(sketch, "E677.97", {"start": v(-89.38, -48.66) * mm, "mid": v(-88.4, -46.53) * mm, "end": v(-88.78, -44.2) * mm});
            skArc(sketch, "E677.98", {"start": v(-75.32, -64.53) * mm, "mid": v(-77.3, -63.27) * mm, "end": v(-79.65, -63.34) * mm});
            skArc(sketch, "E677.99", {"start": v(-82.83, -64.3) * mm, "mid": v(-81.23, -63.85) * mm, "end": v(-79.65, -63.34) * mm});
            skArc(sketch, "E677.100", {"start": v(-84.51, -62.07) * mm, "mid": v(-83.68, -63.2) * mm, "end": v(-82.83, -64.3) * mm});
            skArc(sketch, "E677.101", {"start": v(-82.7, -59.25) * mm, "mid": v(-83.63, -60.64) * mm, "end": v(-84.51, -62.07) * mm});
            skArc(sketch, "E677.102", {"start": v(-82.72, -59.28) * mm, "mid": v(-82.01, -57.04) * mm, "end": v(-82.68, -54.78) * mm});
            skArc(sketch, "E677.103", {"start": v(-66.82, -73.3) * mm, "mid": v(-68.94, -72.3) * mm, "end": v(-71.27, -72.65) * mm});
            skArc(sketch, "E677.104", {"start": v(-74.3, -74) * mm, "mid": v(-72.77, -73.35) * mm, "end": v(-71.27, -72.65) * mm});
            skArc(sketch, "E677.105", {"start": v(-76.24, -71.98) * mm, "mid": v(-75.28, -73) * mm, "end": v(-74.3, -74) * mm});
            skArc(sketch, "E677.106", {"start": v(-74.8, -68.96) * mm, "mid": v(-75.55, -70.46) * mm, "end": v(-76.24, -71.98) * mm});
            skArc(sketch, "E677.107", {"start": v(-74.81, -69) * mm, "mid": v(-74.38, -66.68) * mm, "end": v(-75.32, -64.53) * mm});
            skArc(sketch, "E677.108", {"start": v(-57.3, -80.95) * mm, "mid": v(-59.54, -80.22) * mm, "end": v(-61.8, -80.86) * mm});
            skArc(sketch, "E677.109", {"start": v(-64.64, -82.56) * mm, "mid": v(-63.2, -81.73) * mm, "end": v(-61.8, -80.86) * mm});
            skArc(sketch, "E677.110", {"start": v(-66.82, -80.8) * mm, "mid": v(-65.74, -81.7) * mm, "end": v(-64.64, -82.56) * mm});
            skArc(sketch, "E677.111", {"start": v(-65.75, -77.63) * mm, "mid": v(-66.31, -79.21) * mm, "end": v(-66.82, -80.8) * mm});
            skArc(sketch, "E677.112", {"start": v(-65.76, -77.66) * mm, "mid": v(-65.62, -75.32) * mm, "end": v(-66.82, -73.3) * mm});
            skArc(sketch, "E677.113", {"start": v(-46.92, -87.38) * mm, "mid": v(-49.23, -86.92) * mm, "end": v(-51.4, -87.84) * mm});
            skArc(sketch, "E677.114", {"start": v(-54, -89.88) * mm, "mid": v(-52.68, -88.88) * mm, "end": v(-51.4, -87.84) * mm});
            skArc(sketch, "E677.115", {"start": v(-56.38, -88.4) * mm, "mid": v(-55.2, -89.15) * mm, "end": v(-54, -89.88) * mm});
            skArc(sketch, "E677.116", {"start": v(-55.71, -85.12) * mm, "mid": v(-56.08, -86.76) * mm, "end": v(-56.38, -88.4) * mm});
            skArc(sketch, "E677.117", {"start": v(-55.72, -85.16) * mm, "mid": v(-55.87, -82.81) * mm, "end": v(-57.3, -80.95) * mm});
            skArc(sketch, "E677.118", {"start": v(-35.83, -92.48) * mm, "mid": v(-38.17, -92.31) * mm, "end": v(-40.2, -93.49) * mm});
            skArc(sketch, "E677.119", {"start": v(-42.55, -95.83) * mm, "mid": v(-41.36, -94.68) * mm, "end": v(-40.2, -93.49) * mm});
            skArc(sketch, "E677.120", {"start": v(-45.1, -94.67) * mm, "mid": v(-43.83, -95.26) * mm, "end": v(-42.55, -95.83) * mm});
            skArc(sketch, "E677.121", {"start": v(-44.83, -91.33) * mm, "mid": v(-45, -93) * mm, "end": v(-45.1, -94.67) * mm});
            skArc(sketch, "E677.122", {"start": v(-44.84, -91.36) * mm, "mid": v(-45.27, -89.05) * mm, "end": v(-46.92, -87.38) * mm});
            skArc(sketch, "E677.123", {"start": v(-24.2, -96.19) * mm, "mid": v(-26.54, -96.3) * mm, "end": v(-28.42, -97.72) * mm});
            skArc(sketch, "E677.124", {"start": v(-30.45, -100.34) * mm, "mid": v(-29.41, -99.05) * mm, "end": v(-28.42, -97.72) * mm});
            skArc(sketch, "E677.125", {"start": v(-33.12, -99.49) * mm, "mid": v(-31.79, -99.92) * mm, "end": v(-30.45, -100.34) * mm});
            skArc(sketch, "E677.126", {"start": v(-33.27, -96.14) * mm, "mid": v(-33.22, -97.82) * mm, "end": v(-33.12, -99.49) * mm});
            skArc(sketch, "E677.127", {"start": v(-33.27, -96.18) * mm, "mid": v(-33.98, -93.94) * mm, "end": v(-35.83, -92.48) * mm});
            skArc(sketch, "E677.128", {"start": v(-12.19, -98.43) * mm, "mid": v(-14.5, -98.84) * mm, "end": v(-16.2, -100.47) * mm});
            skArc(sketch, "E677.129", {"start": v(-17.9, -103.32) * mm, "mid": v(-17.02, -101.91) * mm, "end": v(-16.2, -100.47) * mm});
            skArc(sketch, "E677.130", {"start": v(-20.64, -102.8) * mm, "mid": v(-19.27, -103.07) * mm, "end": v(-17.9, -103.32) * mm});
            skArc(sketch, "E677.131", {"start": v(-21.2, -99.5) * mm, "mid": v(-20.95, -101.16) * mm, "end": v(-20.64, -102.8) * mm});
            skArc(sketch, "E677.132", {"start": v(-21.2, -99.54) * mm, "mid": v(-22.18, -97.4) * mm, "end": v(-24.2, -96.19) * mm});
            skArc(sketch, "E677.133", {"start": v(0, -99.18) * mm, "mid": v(-2.25, -99.87) * mm, "end": v(-3.72, -101.7) * mm});
            skArc(sketch, "E677.134", {"start": v(-5.06, -104.73) * mm, "mid": v(-4.36, -103.23) * mm, "end": v(-3.72, -101.7) * mm});
            skArc(sketch, "E677.135", {"start": v(-7.85, -104.56) * mm, "mid": v(-6.46, -104.66) * mm, "end": v(-5.06, -104.73) * mm});
            skArc(sketch, "E677.136", {"start": v(-8.81, -101.35) * mm, "mid": v(-8.36, -102.97) * mm, "end": v(-7.85, -104.56) * mm});
            skArc(sketch, "E677.137", {"start": v(-8.8, -101.39) * mm, "mid": v(-10.04, -99.39) * mm, "end": v(-12.19, -98.43) * mm});
            skArc(sketch, "E677.138", {"start": v(12.19, -98.43) * mm, "mid": v(10.04, -99.39) * mm, "end": v(8.8, -101.39) * mm});
            skArc(sketch, "E677.139", {"start": v(7.85, -104.56) * mm, "mid": v(8.35, -102.98) * mm, "end": v(8.8, -101.39) * mm});
            skArc(sketch, "E677.140", {"start": v(5.06, -104.73) * mm, "mid": v(6.46, -104.66) * mm, "end": v(7.85, -104.56) * mm});
            skArc(sketch, "E677.141", {"start": v(3.7, -101.67) * mm, "mid": v(4.36, -103.21) * mm, "end": v(5.06, -104.73) * mm});
            skArc(sketch, "E677.142", {"start": v(3.72, -101.7) * mm, "mid": v(2.25, -99.87) * mm, "end": v(0, -99.18) * mm});
            skArc(sketch, "E677.143", {"start": v(24.2, -96.19) * mm, "mid": v(22.18, -97.4) * mm, "end": v(21.2, -99.54) * mm});
            skArc(sketch, "E677.144", {"start": v(20.64, -102.8) * mm, "mid": v(20.95, -101.18) * mm, "end": v(21.2, -99.54) * mm});
            skArc(sketch, "E677.145", {"start": v(17.9, -103.32) * mm, "mid": v(19.27, -103.07) * mm, "end": v(20.64, -102.8) * mm});
            skArc(sketch, "E677.146", {"start": v(16.17, -100.44) * mm, "mid": v(17, -101.9) * mm, "end": v(17.9, -103.32) * mm});
            skArc(sketch, "E677.147", {"start": v(16.2, -100.47) * mm, "mid": v(14.5, -98.84) * mm, "end": v(12.19, -98.43) * mm});
            skArc(sketch, "E677.148", {"start": v(35.83, -92.48) * mm, "mid": v(33.98, -93.94) * mm, "end": v(33.27, -96.18) * mm});
            skArc(sketch, "E677.149", {"start": v(33.12, -99.49) * mm, "mid": v(33.22, -97.83) * mm, "end": v(33.27, -96.18) * mm});
            skArc(sketch, "E677.150", {"start": v(30.45, -100.34) * mm, "mid": v(31.79, -99.92) * mm, "end": v(33.12, -99.49) * mm});
            skArc(sketch, "E677.151", {"start": v(28.4, -97.7) * mm, "mid": v(29.4, -99.03) * mm, "end": v(30.45, -100.34) * mm});
            skArc(sketch, "E677.152", {"start": v(28.42, -97.72) * mm, "mid": v(26.54, -96.3) * mm, "end": v(24.2, -96.19) * mm});
            skArc(sketch, "E677.153", {"start": v(46.92, -87.38) * mm, "mid": v(45.27, -89.05) * mm, "end": v(44.84, -91.36) * mm});
            skArc(sketch, "E677.154", {"start": v(45.1, -94.67) * mm, "mid": v(45, -93.01) * mm, "end": v(44.84, -91.36) * mm});
            skArc(sketch, "E677.155", {"start": v(42.55, -95.83) * mm, "mid": v(43.83, -95.26) * mm, "end": v(45.1, -94.67) * mm});
            skArc(sketch, "E677.156", {"start": v(40.19, -93.46) * mm, "mid": v(41.35, -94.67) * mm, "end": v(42.55, -95.83) * mm});
            skArc(sketch, "E677.157", {"start": v(40.2, -93.49) * mm, "mid": v(38.17, -92.31) * mm, "end": v(35.83, -92.48) * mm});
            skArc(sketch, "E677.158", {"start": v(57.3, -80.95) * mm, "mid": v(55.87, -82.81) * mm, "end": v(55.72, -85.16) * mm});
            skArc(sketch, "E677.159", {"start": v(56.38, -88.4) * mm, "mid": v(56.08, -86.78) * mm, "end": v(55.72, -85.16) * mm});
            skArc(sketch, "E677.160", {"start": v(54, -89.88) * mm, "mid": v(55.2, -89.15) * mm, "end": v(56.38, -88.4) * mm});
            skArc(sketch, "E677.161", {"start": v(51.37, -87.82) * mm, "mid": v(52.67, -88.87) * mm, "end": v(54, -89.88) * mm});
            skArc(sketch, "E677.162", {"start": v(51.4, -87.84) * mm, "mid": v(49.23, -86.92) * mm, "end": v(46.92, -87.38) * mm});
            skArc(sketch, "E677.163", {"start": v(66.82, -73.3) * mm, "mid": v(65.62, -75.32) * mm, "end": v(65.76, -77.66) * mm});
            skArc(sketch, "E677.164", {"start": v(66.82, -80.8) * mm, "mid": v(66.32, -79.23) * mm, "end": v(65.76, -77.66) * mm});
            skArc(sketch, "E677.165", {"start": v(64.64, -82.56) * mm, "mid": v(65.74, -81.7) * mm, "end": v(66.82, -80.8) * mm});
            skArc(sketch, "E677.166", {"start": v(61.77, -80.84) * mm, "mid": v(63.2, -81.72) * mm, "end": v(64.64, -82.56) * mm});
            skArc(sketch, "E677.167", {"start": v(61.8, -80.86) * mm, "mid": v(59.54, -80.22) * mm, "end": v(57.3, -80.95) * mm});
            skArc(sketch, "E677.168", {"start": v(75.32, -64.53) * mm, "mid": v(74.38, -66.68) * mm, "end": v(74.81, -69) * mm});
            skArc(sketch, "E677.169", {"start": v(76.24, -71.98) * mm, "mid": v(75.55, -70.48) * mm, "end": v(74.81, -69) * mm});
            skArc(sketch, "E677.170", {"start": v(74.3, -74) * mm, "mid": v(75.28, -73) * mm, "end": v(76.24, -71.98) * mm});
            skArc(sketch, "E677.171", {"start": v(71.23, -72.64) * mm, "mid": v(72.75, -73.34) * mm, "end": v(74.3, -74) * mm});
            skArc(sketch, "E677.172", {"start": v(71.27, -72.65) * mm, "mid": v(68.94, -72.3) * mm, "end": v(66.82, -73.3) * mm});
            skArc(sketch, "E677.173", {"start": v(82.68, -54.78) * mm, "mid": v(82.01, -57.04) * mm, "end": v(82.72, -59.28) * mm});
            skArc(sketch, "E677.174", {"start": v(84.51, -62.07) * mm, "mid": v(83.64, -60.66) * mm, "end": v(82.72, -59.28) * mm});
            skArc(sketch, "E677.175", {"start": v(82.83, -64.3) * mm, "mid": v(83.68, -63.2) * mm, "end": v(84.51, -62.07) * mm});
            skArc(sketch, "E677.176", {"start": v(79.62, -63.33) * mm, "mid": v(81.22, -63.84) * mm, "end": v(82.83, -64.3) * mm});
            skArc(sketch, "E677.177", {"start": v(79.65, -63.34) * mm, "mid": v(77.3, -63.27) * mm, "end": v(75.32, -64.53) * mm});
            skArc(sketch, "E677.178", {"start": v(88.78, -44.2) * mm, "mid": v(88.4, -46.53) * mm, "end": v(89.38, -48.66) * mm});
            skArc(sketch, "E677.179", {"start": v(91.5, -51.21) * mm, "mid": v(90.46, -49.92) * mm, "end": v(89.38, -48.66) * mm});
            skArc(sketch, "E677.180", {"start": v(90.1, -53.63) * mm, "mid": v(90.8, -52.43) * mm, "end": v(91.5, -51.21) * mm});
            skArc(sketch, "E677.181", {"start": v(86.8, -53.07) * mm, "mid": v(88.45, -53.38) * mm, "end": v(90.1, -53.63) * mm});
            skArc(sketch, "E677.182", {"start": v(86.83, -53.07) * mm, "mid": v(84.5, -53.3) * mm, "end": v(82.68, -54.78) * mm});
            skArc(sketch, "E677.183", {"start": v(93.54, -32.96) * mm, "mid": v(93.45, -35.31) * mm, "end": v(94.68, -37.31) * mm});
            skArc(sketch, "E677.184", {"start": v(97.1, -39.58) * mm, "mid": v(95.91, -38.42) * mm, "end": v(94.68, -37.31) * mm});
            skArc(sketch, "E677.185", {"start": v(96, -42.15) * mm, "mid": v(96.56, -40.87) * mm, "end": v(97.1, -39.58) * mm});
            skArc(sketch, "E677.186", {"start": v(92.66, -42) * mm, "mid": v(94.34, -42.1) * mm, "end": v(96, -42.15) * mm});
            skArc(sketch, "E677.187", {"start": v(92.7, -42) * mm, "mid": v(90.4, -42.5) * mm, "end": v(88.78, -44.2) * mm});
            skArc(sketch, "E677.188", {"start": v(96.88, -21.22) * mm, "mid": v(97.08, -23.56) * mm, "end": v(98.55, -25.4) * mm});
            skArc(sketch, "E677.189", {"start": v(101.23, -27.35) * mm, "mid": v(99.9, -26.35) * mm, "end": v(98.55, -25.4) * mm});
            skArc(sketch, "E677.190", {"start": v(100.46, -30.04) * mm, "mid": v(100.85, -28.7) * mm, "end": v(101.23, -27.35) * mm});
            skArc(sketch, "E677.191", {"start": v(97.12, -30.3) * mm, "mid": v(98.8, -30.2) * mm, "end": v(100.46, -30.04) * mm});
            skArc(sketch, "E677.192", {"start": v(97.16, -30.3) * mm, "mid": v(94.94, -31.07) * mm, "end": v(93.54, -32.96) * mm});
            skArc(sketch, "E677.193", {"start": v(98.76, -9.15) * mm, "mid": v(99.24, -11.45) * mm, "end": v(100.92, -13.09) * mm});
            skArc(sketch, "E677.194", {"start": v(103.82, -14.7) * mm, "mid": v(102.39, -13.87) * mm, "end": v(100.92, -13.09) * mm});
            skArc(sketch, "E677.195", {"start": v(103.4, -17.46) * mm, "mid": v(103.62, -16.08) * mm, "end": v(103.82, -14.7) * mm});
            skArc(sketch, "E677.196", {"start": v(100.1, -18.13) * mm, "mid": v(101.76, -17.82) * mm, "end": v(103.4, -17.46) * mm});
            skArc(sketch, "E677.197", {"start": v(100.14, -18.12) * mm, "mid": v(98.04, -19.17) * mm, "end": v(96.88, -21.22) * mm});
            skArc(sketch, "E677.198", {"start": v(99.13, 3.05) * mm, "mid": v(99.9, 0.83) * mm, "end": v(101.77, -0.59) * mm});
            skArc(sketch, "E677.199", {"start": v(104.84, -1.83) * mm, "mid": v(103.31, -1.18) * mm, "end": v(101.77, -0.59) * mm});
            skArc(sketch, "E677.200", {"start": v(104.75, -4.63) * mm, "mid": v(104.8, -3.23) * mm, "end": v(104.84, -1.83) * mm});
            skArc(sketch, "E677.201", {"start": v(101.58, -5.69) * mm, "mid": v(103.18, -5.18) * mm, "end": v(104.75, -4.63) * mm});
            skArc(sketch, "E677.202", {"start": v(101.61, -5.68) * mm, "mid": v(99.65, -6.98) * mm, "end": v(98.76, -9.15) * mm});
            skArc(sketch, "E677.203", {"start": v(98, 15.21) * mm, "mid": v(99.03, 13.1) * mm, "end": v(101.07, 11.92) * mm});
            skArc(sketch, "E677.204", {"start": v(104.27, 11.07) * mm, "mid": v(102.68, 11.52) * mm, "end": v(101.07, 11.92) * mm});
            skArc(sketch, "E677.205", {"start": v(104.53, 8.28) * mm, "mid": v(104.4, 9.67) * mm, "end": v(104.27, 11.07) * mm});
            skArc(sketch, "E677.206", {"start": v(101.5, 6.84) * mm, "mid": v(103.03, 7.53) * mm, "end": v(104.53, 8.28) * mm});
            skArc(sketch, "E677.207", {"start": v(101.54, 6.85) * mm, "mid": v(99.75, 5.32) * mm, "end": v(99.13, 3.05) * mm});
            skArc(sketch, "E677.208", {"start": v(95.4, 27.14) * mm, "mid": v(96.67, 25.17) * mm, "end": v(98.84, 24.25) * mm});
            skArc(sketch, "E677.209", {"start": v(102.12, 23.8) * mm, "mid": v(100.48, 24.05) * mm, "end": v(98.84, 24.25) * mm});
            skArc(sketch, "E677.210", {"start": v(102.72, 21.07) * mm, "mid": v(102.43, 22.43) * mm, "end": v(102.12, 23.8) * mm});
            skArc(sketch, "E677.211", {"start": v(99.9, 19.26) * mm, "mid": v(101.32, 20.14) * mm, "end": v(102.72, 21.07) * mm});
            skArc(sketch, "E677.212", {"start": v(99.93, 19.28) * mm, "mid": v(98.34, 17.54) * mm, "end": v(98, 15.21) * mm});
            skArc(sketch, "E677.213", {"start": v(91.34, 38.66) * mm, "mid": v(92.85, 36.86) * mm, "end": v(95.1, 36.21) * mm});
            skArc(sketch, "E677.214", {"start": v(98.42, 36.16) * mm, "mid": v(96.77, 36.22) * mm, "end": v(95.1, 36.21) * mm});
            skArc(sketch, "E677.215", {"start": v(99.35, 33.53) * mm, "mid": v(98.9, 34.85) * mm, "end": v(98.42, 36.16) * mm});
            skArc(sketch, "E677.216", {"start": v(96.77, 31.4) * mm, "mid": v(98.08, 32.44) * mm, "end": v(99.35, 33.53) * mm});
            skArc(sketch, "E677.217", {"start": v(96.8, 31.41) * mm, "mid": v(95.44, 29.5) * mm, "end": v(95.4, 27.14) * mm});
            skArc(sketch, "E677.218", {"start": v(85.9, 49.6) * mm, "mid": v(87.61, 47.99) * mm, "end": v(89.94, 47.63) * mm});
            skArc(sketch, "E677.219", {"start": v(93.23, 47.99) * mm, "mid": v(91.58, 47.83) * mm, "end": v(89.94, 47.63) * mm});
            skArc(sketch, "E677.220", {"start": v(94.48, 45.48) * mm, "mid": v(93.86, 46.74) * mm, "end": v(93.23, 47.99) * mm});
            skArc(sketch, "E677.221", {"start": v(92.18, 43.04) * mm, "mid": v(93.35, 44.24) * mm, "end": v(94.48, 45.48) * mm});
            skArc(sketch, "E677.222", {"start": v(92.2, 43.07) * mm, "mid": v(91.1, 41) * mm, "end": v(91.34, 38.66) * mm});
            skArc(sketch, "E677.223", {"start": v(79.15, 59.77) * mm, "mid": v(81.05, 58.4) * mm, "end": v(83.4, 58.32) * mm});
            skArc(sketch, "E677.224", {"start": v(86.63, 59.08) * mm, "mid": v(85, 58.73) * mm, "end": v(83.4, 58.32) * mm});
            skArc(sketch, "E677.225", {"start": v(88.17, 56.75) * mm, "mid": v(87.4, 57.92) * mm, "end": v(86.63, 59.08) * mm});
            skArc(sketch, "E677.226", {"start": v(86.2, 54.05) * mm, "mid": v(87.2, 55.38) * mm, "end": v(88.17, 56.75) * mm});
            skArc(sketch, "E677.227", {"start": v(86.21, 54.07) * mm, "mid": v(85.37, 51.88) * mm, "end": v(85.9, 49.6) * mm});
            skPoint(sketch, "E677.228", {"position": v(0, 0) * mm});
            skArc(sketch, "E677.229", {"start": v(71.2, 69.04) * mm, "mid": v(73.26, 67.9) * mm, "end": v(75.6, 68.13) * mm});
            skArc(sketch, "E677.230", {"start": v(78.71, 69.28) * mm, "mid": v(77.15, 68.73) * mm, "end": v(75.6, 68.13) * mm});
            skArc(sketch, "E677.231", {"start": v(80.53, 67.15) * mm, "mid": v(79.63, 68.22) * mm, "end": v(78.71, 69.28) * mm});
            skArc(sketch, "E677.232", {"start": v(78.9, 64.23) * mm, "mid": v(79.74, 65.68) * mm, "end": v(80.53, 67.15) * mm});
            skArc(sketch, "E677.233", {"start": v(78.92, 64.26) * mm, "mid": v(78.34, 61.98) * mm, "end": v(79.15, 59.77) * mm});
            skArc(sketch, "E677.234", {"start": v(62.18, 77.27) * mm, "mid": v(64.36, 76.4) * mm, "end": v(66.66, 76.9) * mm});
            skArc(sketch, "E677.235", {"start": v(69.6, 78.42) * mm, "mid": v(68.12, 77.69) * mm, "end": v(66.66, 76.9) * mm});
            skArc(sketch, "E677.236", {"start": v(71.67, 76.54) * mm, "mid": v(70.64, 77.49) * mm, "end": v(69.6, 78.42) * mm});
            skArc(sketch, "E677.237", {"start": v(70.4, 73.44) * mm, "mid": v(71.06, 74.98) * mm, "end": v(71.67, 76.54) * mm});
            skArc(sketch, "E677.238", {"start": v(70.42, 73.47) * mm, "mid": v(70.13, 71.14) * mm, "end": v(71.2, 69.04) * mm});
            skArc(sketch, "E677.239", {"start": v(52.21, 84.33) * mm, "mid": v(54.49, 83.73) * mm, "end": v(56.7, 84.5) * mm});
            skArc(sketch, "E677.240", {"start": v(59.44, 86.38) * mm, "mid": v(58.05, 85.47) * mm, "end": v(56.7, 84.5) * mm});
            skArc(sketch, "E677.241", {"start": v(61.72, 84.77) * mm, "mid": v(60.58, 85.58) * mm, "end": v(59.44, 86.38) * mm});
            skArc(sketch, "E677.242", {"start": v(60.85, 81.53) * mm, "mid": v(61.31, 83.14) * mm, "end": v(61.72, 84.77) * mm});
            skArc(sketch, "E677.243", {"start": v(60.86, 81.57) * mm, "mid": v(60.86, 79.22) * mm, "end": v(62.18, 77.27) * mm});
            skArc(sketch, "E677.244", {"start": v(41.45, 90.1) * mm, "mid": v(43.78, 89.79) * mm, "end": v(45.89, 90.84) * mm});
            skArc(sketch, "E677.245", {"start": v(48.37, 93.03) * mm, "mid": v(47.11, 91.96) * mm, "end": v(45.89, 90.84) * mm});
            skArc(sketch, "E677.246", {"start": v(50.83, 91.71) * mm, "mid": v(49.6, 92.38) * mm, "end": v(48.37, 93.03) * mm});
            skArc(sketch, "E677.247", {"start": v(50.37, 88.4) * mm, "mid": v(50.63, 90.05) * mm, "end": v(50.83, 91.71) * mm});
            skArc(sketch, "E677.248", {"start": v(50.37, 88.43) * mm, "mid": v(50.66, 86.1) * mm, "end": v(52.21, 84.33) * mm});
            skArc(sketch, "E677.249", {"start": v(30.07, 94.51) * mm, "mid": v(32.42, 94.49) * mm, "end": v(34.38, 95.79) * mm});
            skArc(sketch, "E677.250", {"start": v(36.57, 98.27) * mm, "mid": v(35.45, 97.05) * mm, "end": v(34.38, 95.79) * mm});
            skArc(sketch, "E677.251", {"start": v(39.18, 97.26) * mm, "mid": v(37.88, 97.78) * mm, "end": v(36.57, 98.27) * mm});
            skArc(sketch, "E677.252", {"start": v(39.12, 93.91) * mm, "mid": v(39.18, 95.59) * mm, "end": v(39.18, 97.26) * mm});
            skArc(sketch, "E677.253", {"start": v(39.13, 93.95) * mm, "mid": v(39.7, 91.67) * mm, "end": v(41.45, 90.1) * mm});
            skArc(sketch, "E677.254", {"start": v(18.22, 97.5) * mm, "mid": v(20.56, 97.76) * mm, "end": v(22.35, 99.29) * mm});
            skArc(sketch, "E677.255", {"start": v(24.22, 102.02) * mm, "mid": v(23.26, 100.67) * mm, "end": v(22.35, 99.29) * mm});
            skArc(sketch, "E677.256", {"start": v(26.93, 101.34) * mm, "mid": v(25.58, 101.69) * mm, "end": v(24.22, 102.02) * mm});
            skArc(sketch, "E677.257", {"start": v(27.29, 98) * mm, "mid": v(27.14, 99.68) * mm, "end": v(26.93, 101.34) * mm});
            skArc(sketch, "E677.258", {"start": v(27.28, 98.04) * mm, "mid": v(28.13, 95.85) * mm, "end": v(30.07, 94.51) * mm});
            skArc(sketch, "E677.259", {"start": v(6.1, 99) * mm, "mid": v(8.4, 99.54) * mm, "end": v(9.98, 101.28) * mm});
            skArc(sketch, "E677.260", {"start": v(11.5, 104.22) * mm, "mid": v(10.71, 102.76) * mm, "end": v(9.98, 101.28) * mm});
            skArc(sketch, "E677.261", {"start": v(14.27, 103.88) * mm, "mid": v(12.89, 104.06) * mm, "end": v(11.5, 104.22) * mm});
            skArc(sketch, "E677.262", {"start": v(15.04, 100.62) * mm, "mid": v(14.68, 102.26) * mm, "end": v(14.27, 103.88) * mm});
            skArc(sketch, "E677.263", {"start": v(15.03, 100.65) * mm, "mid": v(16.14, 98.58) * mm, "end": v(18.22, 97.5) * mm});
            skCircle(sketch, "E677.264", {"center": v(0, 0) * mm, "radius": 55 * mm});
            skCircle(sketch, "E677.265", {"center": v(0, -55) * mm, "radius": 5 * mm});
            skCircle(sketch, "E677.266", {"center": v(0, 0) * mm, "radius": 91.43 * mm});
            skLineSegment(sketch, "E677.267", {"start": v(-8, -47) * mm, "end": v(8, -47) * mm});
            skLineSegment(sketch, "E677.268", {"start": v(-8, -47) * mm, "end": v(-8, -82.38) * mm});
            skLineSegment(sketch, "E677.269", {"start": v(8, -47) * mm, "end": v(8, -82.38) * mm});
            skArc(sketch, "E677.270", {"start": v(-17, -89.84) * mm, "mid": v(-10.75, -88.22) * mm, "end": v(-8, -82.38) * mm});
            skArc(sketch, "E677.271", {"start": v(8, -82.38) * mm, "mid": v(10.75, -88.22) * mm, "end": v(17, -89.84) * mm});
            skArc(sketch, "E677.272", {"start": v(80.19, -43.92) * mm, "mid": v(80.59, -37.48) * mm, "end": v(75.88, -33.07) * mm});
            skLineSegment(sketch, "E677.273", {"start": v(42.23, -22.13) * mm, "end": v(75.88, -33.07) * mm});
            skLineSegment(sketch, "E677.274", {"start": v(42.23, -22.13) * mm, "end": v(47.17, -6.92) * mm});
            skCircle(sketch, "E677.275", {"center": v(52.3, -17) * mm, "radius": 5 * mm});
            skLineSegment(sketch, "E677.276", {"start": v(47.17, -6.92) * mm, "end": v(80.82, -17.85) * mm});
            skArc(sketch, "E677.277", {"start": v(80.82, -17.85) * mm, "mid": v(87.23, -17.04) * mm, "end": v(90.7, -11.6) * mm});
            skArc(sketch, "E677.278", {"start": v(66.55, 62.7) * mm, "mid": v(60.55, 65.06) * mm, "end": v(54.9, 61.95) * mm});
            skLineSegment(sketch, "E677.279", {"start": v(34.1, 33.32) * mm, "end": v(54.9, 61.95) * mm});
            skLineSegment(sketch, "E677.280", {"start": v(34.1, 33.32) * mm, "end": v(21.15, 42.73) * mm});
            skCircle(sketch, "E677.281", {"center": v(32.33, 44.5) * mm, "radius": 5 * mm});
            skLineSegment(sketch, "E677.282", {"start": v(21.15, 42.73) * mm, "end": v(41.95, 71.35) * mm});
            skArc(sketch, "E677.283", {"start": v(41.95, 71.35) * mm, "mid": v(43.16, 77.7) * mm, "end": v(39.06, 82.67) * mm});
            skArc(sketch, "E677.284", {"start": v(-39.06, 82.67) * mm, "mid": v(-43.16, 77.7) * mm, "end": v(-41.95, 71.35) * mm});
            skLineSegment(sketch, "E677.285", {"start": v(-21.15, 42.73) * mm, "end": v(-41.95, 71.35) * mm});
            skLineSegment(sketch, "E677.286", {"start": v(-21.15, 42.73) * mm, "end": v(-34.1, 33.32) * mm});
            skCircle(sketch, "E677.287", {"center": v(-32.33, 44.5) * mm, "radius": 5 * mm});
            skLineSegment(sketch, "E677.288", {"start": v(-34.1, 33.32) * mm, "end": v(-54.9, 61.95) * mm});
            skArc(sketch, "E677.289", {"start": v(-54.9, 61.95) * mm, "mid": v(-60.55, 65.06) * mm, "end": v(-66.55, 62.7) * mm});
            skArc(sketch, "E677.290", {"start": v(-90.7, -11.6) * mm, "mid": v(-87.23, -17.04) * mm, "end": v(-80.82, -17.85) * mm});
            skLineSegment(sketch, "E677.291", {"start": v(-47.17, -6.92) * mm, "end": v(-80.82, -17.85) * mm});
            skLineSegment(sketch, "E677.292", {"start": v(-47.17, -6.92) * mm, "end": v(-42.23, -22.13) * mm});
            skCircle(sketch, "E677.293", {"center": v(-52.3, -17) * mm, "radius": 5 * mm});
            skLineSegment(sketch, "E677.294", {"start": v(-42.23, -22.13) * mm, "end": v(-75.88, -33.07) * mm});
            skArc(sketch, "E677.295", {"start": v(-75.88, -33.07) * mm, "mid": v(-80.59, -37.48) * mm, "end": v(-80.19, -43.92) * mm});
            skPoint(sketch, "E677.296", {"position": v(0, 0) * mm});
            skCircle(sketch, "E677.297", {"center": v(0, 0) * mm, "radius": 95.24 * mm});
            skArc(sketch, "E677.298", {"start": v(-48.46, -20.2) * mm, "mid": v(-30.86, -42.47) * mm, "end": v(-4.23, -52.33) * mm});
            skArc(sketch, "E677.299", {"start": v(-53.16, -21.92) * mm, "mid": v(-33.8, -46.52) * mm, "end": v(-4.42, -57.33) * mm});
            skArc(sketch, "E677.300", {"start": v(51.07, -12.15) * mm, "mid": v(49.93, 16.22) * mm, "end": v(34.18, 39.85) * mm});
            skArc(sketch, "E677.301", {"start": v(55.9, -13.5) * mm, "mid": v(54.69, 17.77) * mm, "end": v(37.28, 43.78) * mm});
            skArc(sketch, "E677.302", {"start": v(-34.18, 39.85) * mm, "mid": v(-49.93, 16.22) * mm, "end": v(-51.07, -12.15) * mm});
            skArc(sketch, "E677.303", {"start": v(-37.28, 43.78) * mm, "mid": v(-54.69, 17.77) * mm, "end": v(-55.9, -13.5) * mm});
            skArc(sketch, "E677.304", {"start": v(27.34, 44.82) * mm, "mid": v(0, 52.5) * mm, "end": v(-27.34, 44.82) * mm});
            skArc(sketch, "E677.305", {"start": v(30.12, 48.98) * mm, "mid": v(0, 57.5) * mm, "end": v(-30.12, 48.98) * mm});
            skLineSegment(sketch, "E678.trimOffspring", {"start": v(47.4, -16.01) * mm, "end": v(47.03, -16.59) * mm});
            skSolve(sketch);
        }
        {
            var Q0;
            {var subQ5=sQuery(id+"F0.wireOp",EDGE,"E21.3.0");Q0=makeQuery(id+"F0.imprint","IMPRINT",FACE,{"disambiguationData":[TD([[makeQuery(id+"F0.imprint","IMPRINT",EDGE,{"derivedFrom":subQ5}),-1.0]])]});}
            var Q1;
            {var subQ5=sQuery(id+"F0.wireOp",EDGE,"E21.2.0");Q1=makeQuery(id+"F0.imprint","IMPRINT",FACE,{"disambiguationData":[TD([[makeQuery(id+"F0.imprint","IMPRINT",EDGE,{"derivedFrom":subQ5}),-1.0]])]});}
            var Q2;
            {var subQ1=sQuery(id+"F0.wireOp",EDGE,"E21.1.0");Q2=makeQuery(id+"F0.imprint","IMPRINT",FACE,{"disambiguationData":[TD([[makeQuery(id+"F0.imprint","IMPRINT",EDGE,{"derivedFrom":subQ1}),-1.0]])]});}
            var Q3;
            {var subQ0=sQuery(id+"F0.wireOp",EDGE,"E18.bottom");Q3=makeQuery(id+"F0.imprint","IMPRINT",FACE,{"disambiguationData":[TD([[makeQuery(id+"F0.imprint","IMPRINT",EDGE,{"derivedFrom":subQ0}),-1.0]])]});}
            var Q4;
            {var subQ0=sQuery(id+"F0.wireOp",EDGE,"E23");var subQ1=sQuery(id+"F0.wireOp",EDGE,"E18.left");var subQ2=makeQuery(id+"F0.imprint","INTERSECT",VERTEX,{"derivedFrom":[subQ1,subQ0]});Q4=makeQuery(id+"F0.imprint","IMPRINT",FACE,{"disambiguationData":[TD([[makeQuery(id+"F0.imprint","IMPRINT",EDGE,{"disambiguationData":[TD([[subQ2,-1.0]])],"derivedFrom":subQ1}),-1.0]])]});}
            var Q5;
            {var subQ0=sQuery(id+"F0.wireOp",EDGE,"E27.trimOffspring");var subQ1=sQuery(id+"F0.wireOp",EDGE,"E21.3.4");var subQ2=makeQuery(id+"F0.imprint","INTERSECT",VERTEX,{"derivedFrom":[subQ1,subQ0]});Q5=makeQuery(id+"F0.imprint","IMPRINT",FACE,{"disambiguationData":[TD([[makeQuery(id+"F0.imprint","IMPRINT",EDGE,{"disambiguationData":[TD([[subQ2,-1.0]])],"derivedFrom":subQ1}),1.0]])]});}
            var Q6;
            {var subQ0=sQuery(id+"F0.wireOp",EDGE,"E29.trimOffspring");var subQ1=sQuery(id+"F0.wireOp",EDGE,"E21.2.4");var subQ2=makeQuery(id+"F0.imprint","INTERSECT",VERTEX,{"derivedFrom":[subQ1,subQ0]});Q6=makeQuery(id+"F0.imprint","IMPRINT",FACE,{"disambiguationData":[TD([[makeQuery(id+"F0.imprint","IMPRINT",EDGE,{"disambiguationData":[TD([[subQ2,-1.0]])],"derivedFrom":subQ1}),1.0]])]});}
            var Q7;
            {var subQ0=sQuery(id+"F0.wireOp",EDGE,"E25.trimOffspring");var subQ1=sQuery(id+"F0.wireOp",EDGE,"E21.1.4");var subQ2=makeQuery(id+"F0.imprint","INTERSECT",VERTEX,{"derivedFrom":[subQ1,subQ0]});Q7=makeQuery(id+"F0.imprint","IMPRINT",FACE,{"disambiguationData":[TD([[makeQuery(id+"F0.imprint","IMPRINT",EDGE,{"disambiguationData":[TD([[subQ2,-1.0]])],"derivedFrom":subQ1}),1.0]])]});}
            var Q8;
            Q8=makeQuery(id+"F0.imprint","IMPRINT",FACE,{"disambiguationData":[TD([[makeQuery(id+"F0.imprint","IMPRINT",EDGE,{"derivedFrom":sQuery(id+"F0.wireOp",EDGE,"E22")}),1.0]])]});
            var Q9;
            {var subQ6=sQuery(id+"F0.wireOp",EDGE,"E21.2.2");Q9=makeQuery(id+"F0.imprint","IMPRINT",FACE,{"disambiguationData":[TD([[makeQuery(id+"F0.imprint","IMPRINT",EDGE,{"derivedFrom":subQ6}),-1.0]])]});}
            var Q10;
            {var subQ6=sQuery(id+"F0.wireOp",EDGE,"E21.3.2");Q10=makeQuery(id+"F0.imprint","IMPRINT",FACE,{"disambiguationData":[TD([[makeQuery(id+"F0.imprint","IMPRINT",EDGE,{"derivedFrom":subQ6}),-1.0]])]});}
            var Q11;
            {var subQ6=sQuery(id+"F0.wireOp",EDGE,"E21.4.2");Q11=makeQuery(id+"F0.imprint","IMPRINT",FACE,{"disambiguationData":[TD([[makeQuery(id+"F0.imprint","IMPRINT",EDGE,{"derivedFrom":subQ6}),-1.0]])]});}
            var Q12;
            {var subQ0=sQuery(id+"F0.wireOp",EDGE,"E25.trimOffspring");var subQ1=sQuery(id+"F0.wireOp",EDGE,"E21.2.1");var subQ2=makeQuery(id+"F0.imprint","INTERSECT",VERTEX,{"derivedFrom":[subQ1,subQ0]});Q12=makeQuery(id+"F0.imprint","IMPRINT",FACE,{"disambiguationData":[TD([[makeQuery(id+"F0.imprint","IMPRINT",EDGE,{"disambiguationData":[TD([[subQ2,-1.0]])],"derivedFrom":subQ1}),1.0]])]});}
            var Q13;
            {var subQ0=sQuery(id+"F0.wireOp",EDGE,"E29.trimOffspring");var subQ1=sQuery(id+"F0.wireOp",EDGE,"E21.2.3");var subQ2=makeQuery(id+"F0.imprint","INTERSECT",VERTEX,{"derivedFrom":[subQ1,subQ0]});Q13=makeQuery(id+"F0.imprint","IMPRINT",FACE,{"disambiguationData":[TD([[makeQuery(id+"F0.imprint","IMPRINT",EDGE,{"disambiguationData":[TD([[subQ2,1.0]])],"derivedFrom":subQ1}),-1.0]])]});}
            var Q14;
            {var subQ0=sQuery(id+"F0.wireOp",EDGE,"E27.trimOffspring");var subQ1=sQuery(id+"F0.wireOp",EDGE,"E21.3.3");var subQ2=makeQuery(id+"F0.imprint","INTERSECT",VERTEX,{"derivedFrom":[subQ1,subQ0]});Q14=makeQuery(id+"F0.imprint","IMPRINT",FACE,{"disambiguationData":[TD([[makeQuery(id+"F0.imprint","IMPRINT",EDGE,{"disambiguationData":[TD([[subQ2,1.0]])],"derivedFrom":subQ1}),-1.0]])]});}
            var Q15;
            {var subQ0=sQuery(id+"F0.wireOp",EDGE,"E29.trimOffspring");var subQ1=sQuery(id+"F0.wireOp",EDGE,"E21.3.1");var subQ2=makeQuery(id+"F0.imprint","INTERSECT",VERTEX,{"derivedFrom":[subQ1,subQ0]});Q15=makeQuery(id+"F0.imprint","IMPRINT",FACE,{"disambiguationData":[TD([[makeQuery(id+"F0.imprint","IMPRINT",EDGE,{"disambiguationData":[TD([[subQ2,-1.0]])],"derivedFrom":subQ1}),1.0]])]});}
            var Q16;
            {var subQ0=sQuery(id+"F0.wireOp",EDGE,"E27.trimOffspring");var subQ1=sQuery(id+"F0.wireOp",EDGE,"E21.4.1");var subQ2=makeQuery(id+"F0.imprint","INTERSECT",VERTEX,{"derivedFrom":[subQ1,subQ0]});Q16=makeQuery(id+"F0.imprint","IMPRINT",FACE,{"disambiguationData":[TD([[makeQuery(id+"F0.imprint","IMPRINT",EDGE,{"disambiguationData":[TD([[subQ2,-1.0]])],"derivedFrom":subQ1}),1.0]])]});}
            var Q17;
            {var subQ0=sQuery(id+"F0.wireOp",EDGE,"E23");var subQ1=sQuery(id+"F0.wireOp",EDGE,"E21.4.3");var subQ2=makeQuery(id+"F0.imprint","INTERSECT",VERTEX,{"derivedFrom":[subQ1,subQ0]});Q17=makeQuery(id+"F0.imprint","IMPRINT",FACE,{"disambiguationData":[TD([[makeQuery(id+"F0.imprint","IMPRINT",EDGE,{"disambiguationData":[TD([[subQ2,1.0]])],"derivedFrom":subQ1}),-1.0]])]});}
            var Q18;
            {var subQ0=sQuery(id+"F0.wireOp",EDGE,"E23");var subQ1=sQuery(id+"F0.wireOp",EDGE,"E16");var subQ2=makeQuery(id+"F0.imprint","INTERSECT",VERTEX,{"derivedFrom":[subQ1,subQ0]});Q18=makeQuery(id+"F0.imprint","IMPRINT",FACE,{"disambiguationData":[TD([[makeQuery(id+"F0.imprint","IMPRINT",EDGE,{"disambiguationData":[TD([[subQ2,-1.0]])],"derivedFrom":subQ1}),-1.0]])]});}
            var Q19;
            {var subQ1=sQuery(id+"F0.wireOp",EDGE,"E21.4.0");Q19=makeQuery(id+"F0.imprint","IMPRINT",FACE,{"disambiguationData":[TD([[makeQuery(id+"F0.imprint","IMPRINT",EDGE,{"derivedFrom":subQ1}),-1.0]])]});}
            var Q20;
            Q20=makeQuery(id+"F0.imprint","IMPRINT",FACE,{"disambiguationData":[TD([[makeQuery(id+"F0.imprint","IMPRINT",EDGE,{"derivedFrom":sQuery(id+"F0.wireOp",EDGE,"E3")}),1.0]])]});
            var Q21;
            {var subQ0=sQuery(id+"F0.wireOp",EDGE,"E25.trimOffspring");var subQ1=sQuery(id+"F0.wireOp",EDGE,"E21.1.3");var subQ2=makeQuery(id+"F0.imprint","INTERSECT",VERTEX,{"derivedFrom":[subQ1,subQ0]});Q21=makeQuery(id+"F0.imprint","IMPRINT",FACE,{"disambiguationData":[TD([[makeQuery(id+"F0.imprint","IMPRINT",EDGE,{"disambiguationData":[TD([[subQ2,1.0]])],"derivedFrom":subQ1}),-1.0]])]});}
            var Q22;
            {var subQ4=sQuery(id+"F0.wireOp",EDGE,"E19");Q22=makeQuery(id+"F0.imprint","IMPRINT",FACE,{"disambiguationData":[TD([[makeQuery(id+"F0.imprint","IMPRINT",EDGE,{"derivedFrom":subQ4}),-1.0]])]});}
            var Q23;
            {var subQ6=sQuery(id+"F0.wireOp",EDGE,"E21.1.2");Q23=makeQuery(id+"F0.imprint","IMPRINT",FACE,{"disambiguationData":[TD([[makeQuery(id+"F0.imprint","IMPRINT",EDGE,{"derivedFrom":subQ6}),-1.0]])]});}
            var Q24;
            {var subQ0=sQuery(id+"F0.wireOp",EDGE,"E31.MirrorCS");var subQ1=sQuery(id+"F0.wireOp",EDGE,"E21.1.1");var subQ2=makeQuery(id+"F0.imprint","INTERSECT",VERTEX,{"derivedFrom":[subQ1,subQ0]});Q24=makeQuery(id+"F0.imprint","IMPRINT",FACE,{"disambiguationData":[TD([[makeQuery(id+"F0.imprint","IMPRINT",EDGE,{"disambiguationData":[TD([[subQ2,-1.0]])],"derivedFrom":subQ1}),1.0]])]});}
            var Q25;
            {var subQ0=sQuery(id+"F0.wireOp",EDGE,"E31.MirrorCS");var subQ1=sQuery(id+"F0.wireOp",EDGE,"E18.right");var subQ2=makeQuery(id+"F0.imprint","INTERSECT",VERTEX,{"derivedFrom":[subQ1,subQ0]});Q25=makeQuery(id+"F0.imprint","IMPRINT",FACE,{"disambiguationData":[TD([[makeQuery(id+"F0.imprint","IMPRINT",EDGE,{"disambiguationData":[TD([[subQ2,-1.0]])],"derivedFrom":subQ1}),1.0]])]});}
            var Q26;
            {var subQ0=sQuery(id+"F0.wireOp",EDGE,"E31.MirrorCS");var subQ1=sQuery(id+"F0.wireOp",EDGE,"E16");var subQ2=makeQuery(id+"F0.imprint","INTERSECT",VERTEX,{"derivedFrom":[subQ1,subQ0]});Q26=makeQuery(id+"F0.imprint","IMPRINT",FACE,{"disambiguationData":[TD([[makeQuery(id+"F0.imprint","IMPRINT",EDGE,{"disambiguationData":[TD([[subQ2,1.0]])],"derivedFrom":subQ1}),-1.0]])]});}
            extrude(context, id + "F2", {"entities" : qUnion([Q0, Q1, Q2, Q3, Q4, Q5, Q6, Q7, Q8, Q9, Q10, Q11, Q12, Q13, Q14, Q15, Q16, Q17, Q18, Q19, Q20, Q21, Q22, Q23, Q24, Q25, Q26]), "endBound" : BoundingType.SYMMETRIC, "depth" : 1 / 101.6 * mm});
        }
        {
            var Q0;
            {var subQ35=sQuery(id+"F1.wireOp",EDGE,"E44");Q0=makeQuery(id+"F1.imprint","IMPRINT",FACE,{"disambiguationData":[TD([[makeQuery(id+"F1.imprint","IMPRINT",EDGE,{"derivedFrom":subQ35}),-1.0]])]});}
            var Q1;
            {var subQ6=sQuery(id+"F1.wireOp",EDGE,"E120");Q1=makeQuery(id+"F1.imprint","IMPRINT",FACE,{"disambiguationData":[TD([[makeQuery(id+"F1.imprint","IMPRINT",EDGE,{"derivedFrom":subQ6}),-1.0]])]});}
            var Q2;
            {var subQ16=sQuery(id+"F1.wireOp",EDGE,"E96");Q2=makeQuery(id+"F1.imprint","IMPRINT",FACE,{"disambiguationData":[TD([[makeQuery(id+"F1.imprint","IMPRINT",EDGE,{"derivedFrom":subQ16}),-1.0]])]});}
            var Q3;
            {var subQ10=sQuery(id+"F1.wireOp",EDGE,"E139");Q3=makeQuery(id+"F1.imprint","IMPRINT",FACE,{"disambiguationData":[TD([[makeQuery(id+"F1.imprint","IMPRINT",EDGE,{"derivedFrom":subQ10}),-1.0]])]});}
            var Q4;
            {var subQ16=sQuery(id+"F1.wireOp",EDGE,"E154");Q4=makeQuery(id+"F1.imprint","IMPRINT",FACE,{"disambiguationData":[TD([[makeQuery(id+"F1.imprint","IMPRINT",EDGE,{"derivedFrom":subQ16}),-1.0]])]});}
            var Q5;
            {var subQ0=sQuery(id+"F1.wireOp",EDGE,"E677.276");var subQ1=sQuery(id+"F1.wireOp",EDGE,"E150");var subQ2=makeQuery(id+"F1.imprint","INTERSECT",VERTEX,{"derivedFrom":[subQ1,subQ0]});Q5=makeQuery(id+"F1.imprint","IMPRINT",FACE,{"disambiguationData":[TD([[makeQuery(id+"F1.imprint","IMPRINT",EDGE,{"disambiguationData":[TD([[subQ2,-1.0]])],"derivedFrom":subQ1}),-1.0]])]});}
            extrude(context, id + "F3", {"entities" : qUnion([Q0, Q1, Q2, Q3, Q4, Q5]), "operationType" : NewBodyOperationType.ADD, "endBound" : BoundingType.SYMMETRIC, "depth" : 6.35 * mm});
        }
    });
